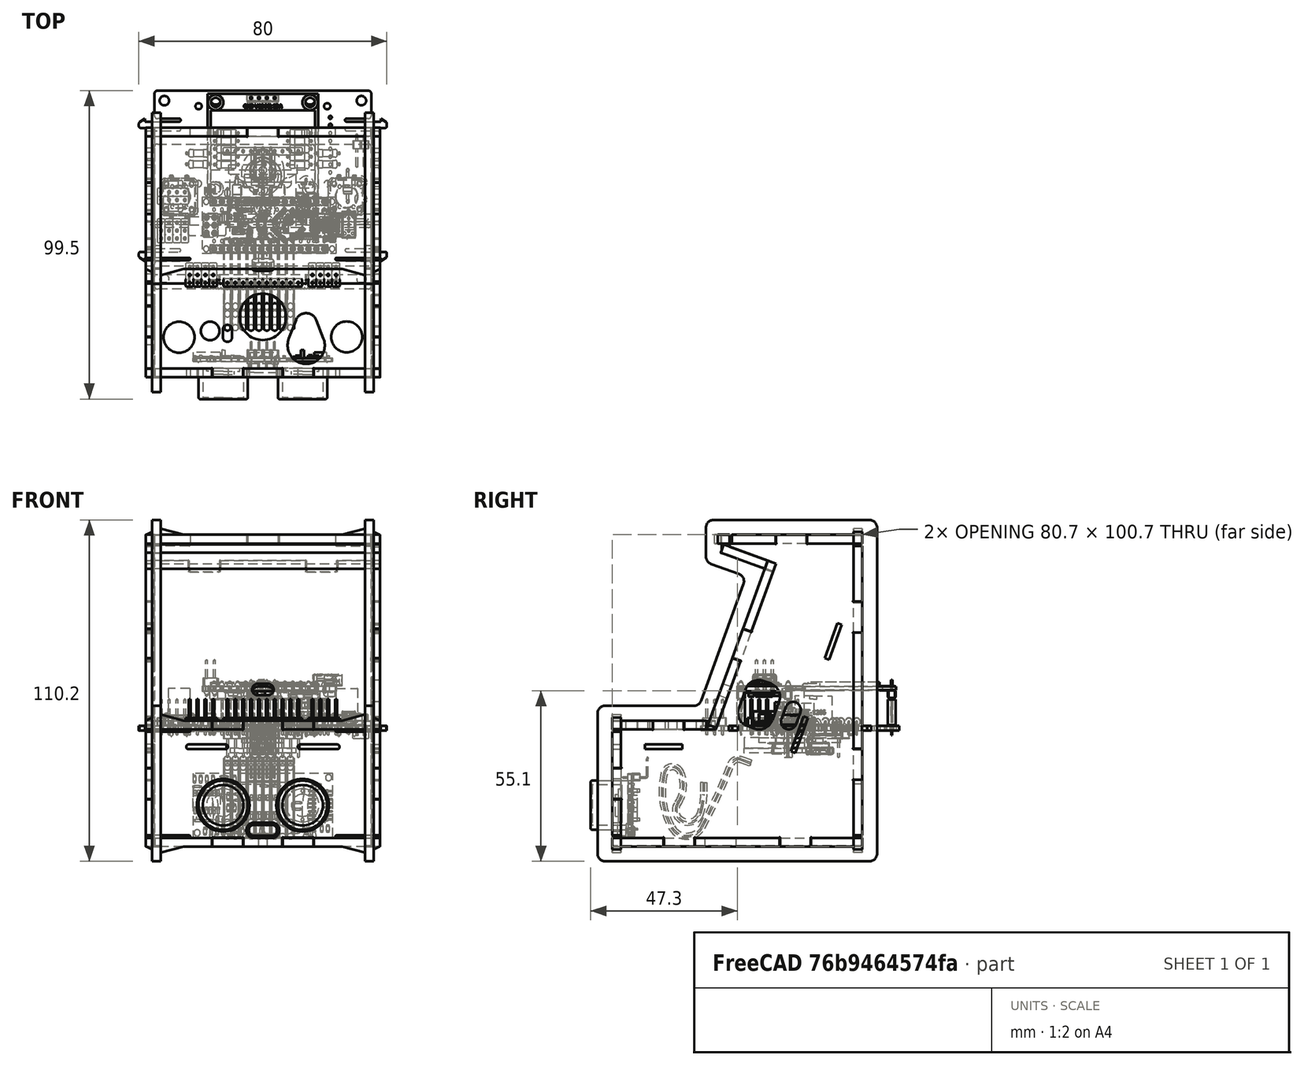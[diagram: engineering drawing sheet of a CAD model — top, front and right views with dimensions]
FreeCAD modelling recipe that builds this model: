
FCSTD DOCUMENT  (FreeCAD 1.0R39319 (Git))
Label: TheThing_v81_multiJoin_parts_assy_LS2
License: CERN Open Hardware Licence permissive
LicenseURL: https://cern-ohl.web.cern.ch/
objects: Part::Feature×104, Sketcher::SketchObject×25, Part::Part2DObjectPython×14, PartDesign::Body×13, App::Part×12, PartDesign::Plane×11, PartDesign::AdditivePipe×9, PartDesign::FeatureBase×9, PartDesign::SubShapeBinder×8, App::DocumentObjectGroup×5, PartDesign::Pad×5, App::VRMLObject×2, TechDraw::DrawSVGTemplate×1, PartDesign::Line×1, PartDesign::PolarPattern×1, PartDesign::Groove×1, PartDesign::Chamfer×1, PartDesign::SubtractivePipe×1, TechDraw::DrawViewImage×1, TechDraw::DrawPage×1
note: 272 computed .brp shape members not serialized (recipe doc carries the construction recipe); baked Part::Feature solids carry a one-line shape summary decoded from their .brp

FEATURE [Part::Feature] Pad001_tab
  shape: bbox 2.8 x 80.6 x 100.6 mm, 98 faces (baked)
FEATURE [Part::Feature] Pad002_tab
  shape: bbox 2.8 x 80.6 x 100.6 mm, 86 faces (baked)
FEATURE [Part::Feature] Pocket_tab
  shape: bbox 75.6 x 2.8 x 104.6 mm, 110 faces (baked)
FEATURE [Part::Feature] Pocket016_tab
  shape: bbox 75.6 x 22.4 x 55.27 mm, 82 faces (baked)
FEATURE [Part::Feature] Pad018_tab
  shape: bbox 75.6 x 33.14 x 2.8 mm, 64 faces (baked)
FEATURE [Part::Feature] Pocket017_tab
  shape: bbox 75.6 x 2.8 x 44.6 mm, 118 faces (baked)
FEATURE [Part::Feature] Pocket021_tab
  shape: bbox 75.6 x 77.8 x 2.8 mm, 54 faces (baked)
FEATURE [Part::Feature] Fillet_tab
  shape: bbox 75.6 x 47.6 x 2.8 mm, 54 faces (baked)
FEATURE [Part::Feature] Pad016_tab
  shape: bbox 75.6 x 17.8 x 8.761 mm, 22 faces (baked)
FEATURE [Part::Feature] Body_right_clip_tab
  shape: bbox 2.8 x 90.2 x 110.2 mm, 46 faces (baked)
FEATURE [Part::Feature] Body_left_clip_tab
  Placement = pos=(-68.8,0,0) rot=(0,0,1;0rad)
  shape: bbox 2.8 x 90.2 x 110.2 mm, 46 faces (baked)
FEATURE [Part::Feature] Part__Feature001  label="switch_slide"
  shape: bbox 10.8 x 10.21 x 13.32 mm, 46 faces (baked)
FEATURE [Part::Feature] Part__Feature002  label="Stopper_bat"
  shape: bbox 2.8 x 15.6 x 14 mm, 30 faces (baked)
FEATURE [App::VRMLObject] TheThing_v8_main
  Placement = pos=(0,5.3,13.8) rot=(1,0,0;1.22173rad)
FEATURE [App::VRMLObject] TheThing_v8_addon
  Placement = pos=(0,-45.3,-5.2) rot=(0,0,1;0rad)
FEATURE [Part::Feature] Part__Feature004  label="User Library-9V Duracell Battery"
  shape: bbox 25.33 x 0.8457 x 15.74 mm, 1 faces, 0 solids (baked)
FEATURE [Part::Feature] Part__Feature005  label="User Library-9V Duracell Battery001"
  shape: bbox 24.78 x 2e-07 x 15.38 mm, 1 faces, 0 solids (baked)
FEATURE [Part::Feature] Part__Feature006  label="User Library-9V Duracell Battery002"
  shape: bbox 26 x 42.82 x 16.6 mm, 188 faces, 0 solids (baked)
FEATURE [Part::Feature] Part__Feature007  label="User Library-9V Duracell Battery003"
  shape: bbox 8.776 x 3 x 7.6 mm, 28 faces, 0 solids (baked)
FEATURE [Part::Feature] Part__Feature008  label="User Library-9V Duracell Battery004"
  shape: bbox 6.35 x 1.5 x 6.35 mm, 2 faces, 0 solids (baked)
FEATURE [Part::Feature] Part__Feature009  label="User Library-9V Duracell Battery005"
  shape: bbox 8 x 3.2 x 8 mm, 10 faces, 0 solids (baked)
FEATURE [App::Part] User_Library_9V_Duracell_Battery  label="9V Duracell Battery006"
  Group = -> [Part__Feature004,Part__Feature005,Part__Feature006,Part__Feature007,Part__Feature008,Part__Feature009]
  Origin = -> Origin
  Placement = pos=(0,0.6,-26) rot=(0,0,1;0rad)
FEATURE [Part::Feature] Part__Feature951  label="_68005_cp005_cp"
  shape: bbox 13.59 x 26.29 x 1.575 mm, 25 faces (baked)
FEATURE [Part::Feature] Part__Feature954  label="_68005_cp005_cp003"
  shape: bbox 7.925 x 7.925 x 3.557 mm, 30 faces (baked)
FEATURE [Part::Feature] Part__Feature955  label="_68005_cp005_cp004"
  shape: bbox 9.35 x 9.35 x 4.186 mm, 132 faces (baked)
FEATURE [App::Part] _68005_cp005_cp  label="9V_conn"
  Group = -> [Part__Feature951,Part__Feature954,Part__Feature955]
  Origin = -> Origin041
  Placement = pos=(-2.41e-14,30,-26) rot=(0.57735,-0.57735,-0.57735;4.18879rad)
FEATURE [App::DocumentObjectGroup] Group  label="Acrylic_Parts"
  Group = -> [Pad001_tab,Pad002_tab,Pocket_tab,Pocket016_tab,Pad018_tab,Pocket017_tab,Pocket021_tab,Fillet_tab,Pad016_tab,Body_right_clip_tab,Body_left_clip_tab]
FEATURE [Part::Feature] Part__Feature956  label="PinSocket_1x10_P2.54mm_Vertical"
  Placement = pos=(-11.4,-16.0152,-10.4002) rot=(-0.633687,0.633687,0.443713;2.30637rad)
  shape: bbox 25.4 x 11.37 x 5.294 mm, 270 faces (baked)
FEATURE [Part::Feature] Part__Feature957  label="PinSocket_1x10_P2.54mm_Vertical001"
  Placement = pos=(-11.4,-31.1152,-17.0002) rot=(0,0,-1;4.71239rad)
  shape: bbox 25.4 x 2.54 x 11.6 mm, 270 faces (baked)
FEATURE [PartDesign::Plane] DatumPlane
  AttachmentOffset = pos=(0,-16.7,0) rot=(1,0,0;1.5708rad)
  Length = 82.3105
  MapMode = 2
  Placement = pos=(11.43,0,-16.7) rot=(0.707107,0.707107,0;3.14159rad)
  ResizeMode = 0
  Width = 61.8694
FEATURE [Sketcher::SketchObject] Sketch001
  ArcFitTolerance = 1e-06
  FullyConstrained = true
  MakeInternals = false
  MapMode = 5
  Placement = pos=(11.43,0,-16.7) rot=(0.707107,0.707107,0;3.14159rad)
  sketch-geometry (9):
    g0: ArcOfCircle CenterX=-31.1 CenterY=0 CenterZ=0 NormalX=0 NormalY=0 NormalZ=1 AngleXU=0 Radius=1 StartAngle=1.82348 EndAngle=4.45971
    g1: LineSegment StartX=-30.85 StartY=-1.23825 StartZ=0 EndX=-30.85 EndY=-0.968246 EndZ=0
    g2: LineSegment StartX=-30.85 StartY=1.23825 StartZ=0 EndX=-31.35 EndY=1.23825 EndZ=0
    g3: LineSegment StartX=-31.35 StartY=1.23825 StartZ=0 EndX=-31.35 EndY=0.968246 EndZ=0
    g4: LineSegment StartX=-31.35 StartY=-1.23825 StartZ=0 EndX=-30.85 EndY=-1.23825 EndZ=0
    g5: GeomPoint [constr] X=-31.1 Y=0 Z=0
    g6: ArcOfCircle CenterX=-31.1 CenterY=0 CenterZ=0 NormalX=0 NormalY=0 NormalZ=1 AngleXU=0 Radius=1 StartAngle=4.96507 EndAngle=7.6013
    g7: LineSegment StartX=-31.35 StartY=-0.968246 StartZ=0 EndX=-31.35 EndY=-1.23825 EndZ=0
    g8: LineSegment StartX=-30.85 StartY=0.968246 StartZ=0 EndX=-30.85 EndY=1.23825 EndZ=0
  constraints (27):
    c: Diameter(g0) = 2
    c: Distance(g0,g-2) = 31.1
    c: PointOnObject(g0,g-1)
    c: Coincident(g8,g2)
    c: Coincident(g2,g3)
    c: Coincident(g7,g4)
    c: Coincident(g4,g1)
    c: Vertical(g1)
    c: Vertical(g3)
    c: Horizontal(g2)
    c: Horizontal(g4)
    c: Symmetric(g3,g1,g5)
    c: Coincident(g5,g0)
    c: Distance(g2,g2) = 0.5
    c: PointOnObject(g6,g8)
    c: Equal(g0,g6)
    c: PointOnObject(g0,g7)
    c: Coincident(g0,g6)
    c: Coincident(g3,g0)
    c: PointOnObject(g7,g0)
    c: Coincident(g1,g6)
    c: PointOnObject(g8,g6)
    c: Equal(g7,g3)
    c: DistanceY(g3,g3) = 0.27
    c: Vertical(g8)
    c: Vertical(g7)
    c: Equal(g4,g2)
FEATURE [Sketcher::SketchObject] Sketch002
  ArcFitTolerance = 1e-06
  ExternalGeometry = -> [Sketch001]
  FullyConstrained = false
  MakeInternals = false
  MapMode = 5
  Placement = pos=(0,0,0) rot=(0.57735,0.57735,0.57735;2.0944rad)
  sketch-geometry (11):
    g0: LineSegment StartX=-31.1 StartY=-16.7 StartZ=0 EndX=-31.1 EndY=-20.5857 EndZ=0
    g1: ArcOfCircle CenterX=-48.3989 CenterY=-20.5857 CenterZ=0 NormalX=0 NormalY=0 NormalZ=1 AngleXU=0 Radius=17.2989 StartAngle=5.99931 EndAngle=6.28319
    g2: LineSegment StartX=-31.7924 StartY=-25.4308 StartZ=0 EndX=-32.1908 EndY=-26.7964 EndZ=0
    g3: ArcOfCircle CenterX=-36.0202 CenterY=-25.6792 CenterZ=0 NormalX=0 NormalY=0 NormalZ=1 AngleXU=0 Radius=3.98901 StartAngle=2.55428 EndAngle=5.99931
    g4: ArcOfCircle CenterX=-48.0615 CenterY=-17.6636 CenterZ=0 NormalX=0 NormalY=0 NormalZ=1 AngleXU=0 Radius=10.4762 StartAngle=5.69587 EndAngle=6.70733
    g5: ArcOfCircle CenterX=-41.0617 CenterY=-14.5029 CenterZ=0 NormalX=0 NormalY=0 NormalZ=1 AngleXU=0 Radius=2.79585 StartAngle=0.424141 EndAngle=2.90432
    g6: ArcOfCircle CenterX=-20.5527 CenterY=-19.4626 CenterZ=0 NormalX=0 NormalY=0 NormalZ=1 AngleXU=0 Radius=23.896 StartAngle=2.90432 EndAngle=3.65756
    g7: ArcOfCircle CenterX=-36.4895 CenterY=-28.5021 CenterZ=0 NormalX=0 NormalY=0 NormalZ=1 AngleXU=0 Radius=5.57402 StartAngle=3.65756 EndAngle=5.79202
    g8: ArcOfCircle CenterX=-198.048 CenterY=57.9126 CenterZ=0 NormalX=0 NormalY=0 NormalZ=1 AngleXU=0 Radius=188.791 StartAngle=5.79202 EndAngle=5.91067
    g9: ArcOfCircle CenterX=-19.8146 CenterY=-11.7327 CenterZ=0 NormalX=0 NormalY=0 NormalZ=1 AngleXU=0 Radius=2.56576 StartAngle=1.21797 EndAngle=2.76908
    g10: LineSegment StartX=-18.928 StartY=-9.32503 StartZ=0 EndX=-15.8303 EndY=-10.4657 EndZ=0
  constraints (12):
    c: Vertical(g0)
    c: Tangent(g0,g1) = 1.5708
    c: Tangent(g2,g3) = 1.5708
    c: Tangent(g3,g4) = 1.5708
    c: Tangent(g4,g5) = -1.5708
    c: Tangent(g5,g6) = -1.5708
    c: Tangent(g6,g7) = -1.5708
    c: Tangent(g7,g8) = -1.5708
    c: Tangent(g8,g9) = 1.5708
    c: Tangent(g1,g2) = 1.5708
    c: Symmetric(g-3,g-3,g0)
    c: Tangent(g9,g10) = 1.5708
FEATURE [PartDesign::AdditivePipe] AdditivePipe
  AuxilleryCurvelinear = true
  AuxillerySpineTangent = false
  Binormal = (0,0,0)
  Mode = 0
  Placement = pos=(11.43,0,-16.7) rot=(0.707107,0.707107,0;3.14159rad)
  Profile = -> Sketch001
  Refine = true
  Spine = -> Sketch002
  SpineTangent = false
  Suppressed = false
  Transformation = 0
  Transition = 0
FEATURE [PartDesign::Body] Body  label="Cable_flat_10x"
  AllowCompound = false
  Group = -> [DatumPlane,Sketch001,Sketch002,AdditivePipe]
  Origin = -> Origin042
  Tip = -> AdditivePipe
FEATURE [PartDesign::FeatureBase] Clone
  BaseFeature = -> Body
  Suppressed = false
FEATURE [PartDesign::Body] Body001
  AllowCompound = false
  BaseFeature = -> Body
  Group = -> [Clone]
  Origin = -> Origin043
  Placement = pos=(-2.54,0,0) rot=(0,0,1;0rad)
  Tip = -> Clone
FEATURE [PartDesign::FeatureBase] Clone001
  BaseFeature = -> Body
  Suppressed = false
FEATURE [PartDesign::Body] Body002
  AllowCompound = false
  BaseFeature = -> Body
  Group = -> [Clone001]
  Origin = -> Origin044
  Placement = pos=(-5.08,0,0) rot=(0,0,1;0rad)
  Tip = -> Clone001
FEATURE [PartDesign::FeatureBase] Clone002
  BaseFeature = -> Body
  Suppressed = false
FEATURE [PartDesign::Body] Body003
  AllowCompound = false
  BaseFeature = -> Body
  Group = -> [Clone002]
  Origin = -> Origin045
  Placement = pos=(-7.62,0,0) rot=(0,0,1;0rad)
  Tip = -> Clone002
FEATURE [PartDesign::FeatureBase] Clone003
  BaseFeature = -> Body
  Suppressed = false
FEATURE [PartDesign::Body] Body004
  AllowCompound = false
  BaseFeature = -> Body
  Group = -> [Clone003]
  Origin = -> Origin046
  Placement = pos=(-10.16,0,0) rot=(0,0,1;0rad)
  Tip = -> Clone003
FEATURE [PartDesign::FeatureBase] Clone004
  BaseFeature = -> Body
  Suppressed = false
FEATURE [PartDesign::Body] Body005
  AllowCompound = false
  BaseFeature = -> Body
  Group = -> [Clone004]
  Origin = -> Origin047
  Placement = pos=(-12.7,0,0) rot=(0,0,1;0rad)
  Tip = -> Clone004
FEATURE [PartDesign::FeatureBase] Clone005
  BaseFeature = -> Body
  Suppressed = false
FEATURE [PartDesign::Body] Body006
  AllowCompound = false
  BaseFeature = -> Body
  Group = -> [Clone005]
  Origin = -> Origin048
  Placement = pos=(-15.24,0,0) rot=(0,0,1;0rad)
  Tip = -> Clone005
FEATURE [PartDesign::FeatureBase] Clone006
  BaseFeature = -> Body
  Suppressed = false
FEATURE [PartDesign::Body] Body007
  AllowCompound = false
  BaseFeature = -> Body
  Group = -> [Clone006]
  Origin = -> Origin049
  Placement = pos=(-17.78,0,0) rot=(0,0,1;0rad)
  Tip = -> Clone006
FEATURE [PartDesign::FeatureBase] Clone007
  BaseFeature = -> Body
  Suppressed = false
FEATURE [PartDesign::Body] Body008
  AllowCompound = false
  BaseFeature = -> Body
  Group = -> [Clone007]
  Origin = -> Origin050
  Placement = pos=(-20.32,0,0) rot=(0,0,1;0rad)
  Tip = -> Clone007
FEATURE [PartDesign::FeatureBase] Clone008
  BaseFeature = -> Body
  Suppressed = false
FEATURE [PartDesign::Body] Body009
  AllowCompound = false
  BaseFeature = -> Body
  Group = -> [Clone008]
  Origin = -> Origin051
  Placement = pos=(-22.86,0,0) rot=(0,0,1;0rad)
  Tip = -> Clone008
FEATURE [App::DocumentObjectGroup] Group003  label="Flat_Cable_10x"
  Group = -> [Body,Body001,Body002,Body003,Body004,Body005,Body006,Body007,Body008,Body009]
FEATURE [Part::Feature] Solid  label="PinSocket_1x02_P2.54mm_Vertical"
  Placement = pos=(30.3,8.89176,17.5439) rot=(-0.171088,0.171088,0.970288;1.60095rad)
  shape: bbox 5.08 x 5.294 x 11.37 mm, 62 faces (baked)
FEATURE [PartDesign::SubShapeBinder] Binder  label="Binder(PinSocket_1x02_P2.54mm_Vertical)"
  BindCopyOnChange = 0
  BindMode = 0
  ClaimChildren = false
  Context = -> Group004 [Body010.Binder.]
  Fuse = false
  MakeFace = true
  OffsetFill = false
  OffsetIntersection = false
  OffsetJoinType = 0
  OffsetOpenResult = false
  PartialLoad = false
  Relative = true
  Support = -> [Solid]
  _Version = 8
FEATURE [PartDesign::SubShapeBinder] Binder001  label="Binder001(9V_conn)"
  BindCopyOnChange = 0
  BindMode = 0
  ClaimChildren = false
  Context = -> Group004 [Body010.Binder001.]
  Fuse = false
  MakeFace = true
  OffsetFill = false
  OffsetIntersection = false
  OffsetJoinType = 0
  OffsetOpenResult = false
  PartialLoad = false
  Relative = true
  Support = -> [_68005_cp005_cp]
  _Version = 8
FEATURE [PartDesign::SubShapeBinder] Binder002  label="Binder002(Pocket_tab)"
  BindCopyOnChange = 0
  BindMode = 0
  ClaimChildren = false
  Context = -> Group004 [Body010.Binder002.]
  Fuse = false
  MakeFace = true
  OffsetFill = false
  OffsetIntersection = false
  OffsetJoinType = 0
  OffsetOpenResult = false
  PartialLoad = false
  Relative = true
  Support = -> [Pocket_tab]
  _Version = 8
FEATURE [Sketcher::SketchObject] Sketch
  ArcFitTolerance = 1e-06
  ExternalGeometry = -> [Binder001]
  FullyConstrained = true
  MakeInternals = false
  MapMode = 5
  Placement = pos=(0,2.34e-14,-19.2055) rot=(0,0,1;0rad)
  sketch-geometry (19):
    g0: ArcOfCircle CenterX=1.23825 CenterY=26.8446 CenterZ=0 NormalX=0 NormalY=0 NormalZ=1 AngleXU=0 Radius=1 StartAngle=3.39427 EndAngle=6.03051
    g1: LineSegment StartX=2.47649 StartY=26.5946 StartZ=0 EndX=2.47649 EndY=27.0946 EndZ=0
    g2: LineSegment StartX=2.47649 StartY=27.0946 StartZ=0 EndX=2.20649 EndY=27.0946 EndZ=0
    g3: LineSegment StartX=0 StartY=27.0946 StartZ=0 EndX=0 EndY=26.5946 EndZ=0
    g4: LineSegment StartX=0 StartY=26.5946 StartZ=0 EndX=0.27 EndY=26.5946 EndZ=0
    g5: GeomPoint [constr] X=1.23825 Y=26.8446 Z=0
    g6: ArcOfCircle CenterX=1.23825 CenterY=26.8446 CenterZ=0 NormalX=0 NormalY=0 NormalZ=1 AngleXU=0 Radius=1 StartAngle=0.25268 EndAngle=2.88891
    g7: LineSegment StartX=0.27 StartY=27.0946 StartZ=0 EndX=0 EndY=27.0946 EndZ=0
    g8: LineSegment StartX=2.20649 StartY=26.5946 StartZ=0 EndX=2.47649 EndY=26.5946 EndZ=0
    g9: LineSegment [constr] StartX=2.47649 StartY=26.8446 StartZ=0 EndX=6.34996 EndY=26.8446 EndZ=0
    g10: ArcOfCircle [constr] CenterX=-1.23825 CenterY=26.8446 CenterZ=0 NormalX=0 NormalY=0 NormalZ=1 AngleXU=0 Radius=1 StartAngle=3.39427 EndAngle=6.03051
    g11: LineSegment [constr] StartX=0 StartY=26.5946 StartZ=0 EndX=0 EndY=27.0946 EndZ=0
    g12: LineSegment [constr] StartX=0 StartY=27.0946 StartZ=0 EndX=-0.27 EndY=27.0946 EndZ=0
    g13: LineSegment [constr] StartX=-2.47649 StartY=27.0946 StartZ=0 EndX=-2.47649 EndY=26.5946 EndZ=0
    g14: LineSegment [constr] StartX=-2.47649 StartY=26.5946 StartZ=0 EndX=-2.20649 EndY=26.5946 EndZ=0
    g15: GeomPoint [constr] X=-1.23825 Y=26.8446 Z=0
    g16: LineSegment [constr] StartX=-2.20649 StartY=27.0946 StartZ=0 EndX=-2.47649 EndY=27.0946 EndZ=0
    g17: ArcOfCircle [constr] CenterX=-1.23825 CenterY=26.8446 CenterZ=0 NormalX=0 NormalY=0 NormalZ=1 AngleXU=0 Radius=1 StartAngle=0.25268 EndAngle=2.88891
    g18: LineSegment [constr] StartX=-0.27 StartY=26.5946 StartZ=0 EndX=0 EndY=26.5946 EndZ=0
  constraints (51):
    c: Coincident(g1,g2)
    c: Coincident(g7,g3)
    c: Coincident(g3,g4)
    c: Coincident(g8,g1)
    c: Horizontal(g2)
    c: Horizontal(g4)
    c: Vertical(g1)
    c: Vertical(g3)
    c: Symmetric(g7,g1,g5)
    c: Coincident(g5,g0)
    c: Diameter(g0) = 2
    c: DistanceY(g3,g3) = 0.5
    c: Equal(g0,g6)
    c: Coincident(g0,g6)
    c: Coincident(g2,g6)
    c: Coincident(g7,g6)
    c: Coincident(g4,g0)
    c: Coincident(g8,g0)
    c: Horizontal(g7)
    c: Horizontal(g8)
    c: Equal(g7,g2)
    c: DistanceX(g7,g7) = 0.27
    c: Horizontal(g9)
    c: Equal(g3,g1)
    c: Symmetric(g1,g1,g9)
    c: Symmetric(g-4,g-4,g9)
    c: Coincident(g11,g12)
    c: Coincident(g16,g13)
    c: Coincident(g13,g14)
    c: Coincident(g18,g11)
    c: Horizontal(g12)
    c: Horizontal(g14)
    c: Vertical(g11)
    c: Vertical(g13)
    c: Symmetric(g16,g11,g15)
    c: Coincident(g15,g10)
    c: Coincident(g16,g17)
    c: Equal(g10,g17)
    c: Coincident(g17,g12)
    c: Coincident(g10,g17)
    c: Coincident(g14,g10)
    c: Coincident(g18,g10)
    c: Horizontal(g16)
    c: Horizontal(g18)
    c: Equal(g12,g16)
    c: Equal(g13,g11)
    c: Equal(g17,g6)
    c: Equal(g12,g7)
    c: Equal(g11,g3)
    c: PointOnObject(g7,g-2)
    c: Coincident(g12,g7)
FEATURE [PartDesign::Plane] DatumPlane001
  AttachmentOffset = pos=(0,0,-0.8) rot=(0,0,1;0rad)
  Length = 67.3011
  MapMode = 5
  Placement = pos=(6.1e-15,26.832,3.28e-14) rot=(0,0.707107,0.707107;3.14159rad)
  ResizeMode = 0
  Width = 60.6448
FEATURE [Sketcher::SketchObject] Sketch003
  ArcFitTolerance = 1e-06
  ExternalGeometry = -> [Sketch]
  FullyConstrained = true
  MakeInternals = false
  MapMode = 5
  Placement = pos=(6.1e-15,26.832,3.28e-14) rot=(0,0.707107,0.707107;3.14159rad)
  sketch-geometry (3):
    g0: LineSegment StartX=-3.73e-14 StartY=-19.2055 StartZ=0 EndX=-3.73e-14 EndY=-13.2055 EndZ=0
    g1: ArcOfCircle CenterX=-5.5 CenterY=-13.2055 CenterZ=0 NormalX=0 NormalY=0 NormalZ=1 AngleXU=0 Radius=5.5 StartAngle=1.88e-14 EndAngle=3.14159
    g2: LineSegment StartX=-11 StartY=-13.2055 StartZ=0 EndX=-11 EndY=-14.0055 EndZ=0
  constraints (8):
    c: Vertical(g0)
    c: Tangent(g0,g1) = -1.5708
    c: Angle(g1) = 3.14159
    c: Tangent(g1,g2) = -1.5708
    c: DistanceY(g0,g0) = 6
    c: Radius(g1) = 5.5
    c: DistanceY(g2,g2) = 0.8
    c: Coincident(g0,g-3)
FEATURE [PartDesign::Plane] DatumPlane002
  AttachmentOffset = pos=(0,0,0) rot=(0.57735,0.57735,0.57735;2.0944rad)
  Length = 63.1173
  MapMode = 7
  Placement = pos=(11,26.832,-13.2055) rot=(0.57735,0.57735,0.57735;2.0944rad)
  ResizeMode = 0
  Width = 60.2798
FEATURE [Sketcher::SketchObject] Sketch004
  ArcFitTolerance = 1e-06
  ExternalGeometry = -> [Sketch003]
  FullyConstrained = true
  MakeInternals = false
  MapMode = 5
  Placement = pos=(11,26.832,-13.2055) rot=(0.57735,0.57735,0.57735;2.0944rad)
  sketch-geometry (3):
    g0: LineSegment StartX=0 StartY=-0.8 StartZ=0 EndX=0 EndY=-2 EndZ=0
    g1: ArcOfCircle CenterX=-2.3 CenterY=-2 CenterZ=0 NormalX=0 NormalY=0 NormalZ=1 AngleXU=0 Radius=2.3 StartAngle=4.71239 EndAngle=6.28319
    g2: LineSegment StartX=-2.3 StartY=-4.3 StartZ=0 EndX=-18.3 EndY=-4.3 EndZ=0
  constraints (8):
    c: Coincident(g-3,g0)
    c: PointOnObject(g0,g-2)
    c: Tangent(g0,g1) = 1.5708
    c: Angle(g1) = 1.5708
    c: Tangent(g1,g2) = 1.5708
    c: DistanceY(g0,g0) = 1.2
    c: Radius(g1) = 2.3
    c: DistanceX(g2,g2) = 16
FEATURE [PartDesign::Plane] DatumPlane003
  AttachmentOffset = pos=(0,0,0) rot=(-0.57735,0.57735,0.57735;2.0944rad)
  Length = 63.7802
  MapMode = 45
  Placement = pos=(11,16.532,-17.5055) rot=(0,0,1;4.71239rad)
  ResizeMode = 0
  Width = 67.599
FEATURE [Sketcher::SketchObject] Sketch005
  ArcFitTolerance = 1e-06
  ExternalGeometry = -> [Sketch004,Binder]
  FullyConstrained = false
  MakeInternals = false
  MapMode = 5
  Placement = pos=(11,16.532,-17.5055) rot=(0,0,-1;1.5708rad)
  sketch-geometry (3):
    g0: ArcOfCircle CenterX=8 CenterY=4.21059 CenterZ=0 NormalX=0 NormalY=0 NormalZ=1 AngleXU=0 Radius=4.21059 StartAngle=4.71239 EndAngle=7.61609
    g1: ArcOfCircle CenterX=12.2495 CenterY=21.7356 CenterZ=0 NormalX=0 NormalY=0 NormalZ=1 AngleXU=0 Radius=13.8222 StartAngle=3.8393 EndAngle=4.4745
    g2: ArcOfCircle CenterX=5.29691 CenterY=15.9067 CenterZ=0 NormalX=0 NormalY=0 NormalZ=1 AngleXU=0 Radius=4.74953 StartAngle=1.5708 EndAngle=3.8393
  constraints (5):
    c: Tangent(g0,g1) = 1.5708
    c: Tangent(g1,g2) = -1.5708
    c: PointOnObject(g2,g-5)
    c: Perpendicular(g2,g-5)
    c: Tangent(g0,g-3) = -1.5708
FEATURE [PartDesign::Plane] DatumPlane004
  AttachmentOffset = pos=(0,0,-2.5) rot=(0,0,1;0rad)
  Length = 63.1173
  MapMode = 5
  Placement = pos=(31.61,3.25e-14,6e-16) rot=(0.57735,0.57735,0.57735;2.0944rad)
  ResizeMode = 0
  Width = 60.2798
FEATURE [Sketcher::SketchObject] Sketch006
  ArcFitTolerance = 1e-06
  ExternalGeometry = -> [Sketch005,Binder]
  FullyConstrained = true
  MakeInternals = false
  MapMode = 5
  Placement = pos=(31.61,3.25e-14,6e-16) rot=(0.57735,0.57735,0.57735;2.0944rad)
  sketch-geometry (3):
    g0: LineSegment StartX=11.2351 StartY=-17.5055 StartZ=0 EndX=7.55999 EndY=-17.5055 EndZ=0
    g1: ArcOfCircle CenterX=7.55999 CenterY=-9.50551 CenterZ=0 NormalX=0 NormalY=0 NormalZ=1 AngleXU=0 Radius=8 StartAngle=2.79253 EndAngle=4.71239
    g2: LineSegment StartX=0.0424531 StartY=-6.76935 StartZ=0 EndX=8.96016 EndY=17.7319 EndZ=0
  constraints (7):
    c: Coincident(g0,g-3)
    c: Horizontal(g0)
    c: Tangent(g0,g1) = 1.5708
    c: Perpendicular(g2,g-4)
    c: Symmetric(g-4,g-4,g2)
    c: Tangent(g1,g2) = 1.5708
    c: Radius(g1) = 8
FEATURE [TechDraw::DrawSVGTemplate] Template
  Height = 210
  Orientation = 1
  Template = <userpath>/Documents/FreeCAD/Templates/A4_Landscape_blank.svg
  Width = 297
FEATURE [Sketcher::SketchObject] Sketch007
  ArcFitTolerance = 1e-06
  AttachmentSupport = -> [Binder001]
  ExternalGeometry = -> [Binder001]
  FullyConstrained = true
  MakeInternals = false
  MapMode = 5
  Placement = pos=(4.3e-15,2.23e-14,-19.2055) rot=(0,0,1;0rad)
  sketch-geometry (19):
    g0: ArcOfCircle [constr] CenterX=1.23825 CenterY=26.8446 CenterZ=0 NormalX=0 NormalY=0 NormalZ=1 AngleXU=0 Radius=1 StartAngle=3.39427 EndAngle=6.03051
    g1: LineSegment [constr] StartX=2.47649 StartY=26.5946 StartZ=0 EndX=2.47649 EndY=27.0946 EndZ=0
    g2: LineSegment [constr] StartX=2.47649 StartY=27.0946 StartZ=0 EndX=2.20649 EndY=27.0946 EndZ=0
    g3: LineSegment StartX=0 StartY=27.0946 StartZ=0 EndX=0 EndY=26.5946 EndZ=0
    g4: LineSegment [constr] StartX=0 StartY=26.5946 StartZ=0 EndX=0.27 EndY=26.5946 EndZ=0
    g5: GeomPoint [constr] X=1.23825 Y=26.8446 Z=0
    g6: ArcOfCircle [constr] CenterX=1.23825 CenterY=26.8446 CenterZ=0 NormalX=0 NormalY=0 NormalZ=1 AngleXU=0 Radius=1 StartAngle=0.25268 EndAngle=2.88891
    g7: LineSegment [constr] StartX=0.27 StartY=27.0946 StartZ=0 EndX=0 EndY=27.0946 EndZ=0
    g8: LineSegment [constr] StartX=2.20649 StartY=26.5946 StartZ=0 EndX=2.47649 EndY=26.5946 EndZ=0
    g9: LineSegment [constr] StartX=2.47649 StartY=26.8446 StartZ=0 EndX=-2.47649 EndY=26.8446 EndZ=0
    g10: ArcOfCircle CenterX=-1.23825 CenterY=26.8446 CenterZ=0 NormalX=0 NormalY=0 NormalZ=1 AngleXU=0 Radius=1 StartAngle=3.39427 EndAngle=6.03051
    g11: LineSegment [constr] StartX=0 StartY=26.5946 StartZ=0 EndX=0 EndY=27.0946 EndZ=0
    g12: LineSegment StartX=0 StartY=27.0946 StartZ=0 EndX=-0.27 EndY=27.0946 EndZ=0
    g13: LineSegment StartX=-2.47649 StartY=27.0946 StartZ=0 EndX=-2.47649 EndY=26.5946 EndZ=0
    g14: LineSegment StartX=-2.47649 StartY=26.5946 StartZ=0 EndX=-2.20649 EndY=26.5946 EndZ=0
    g15: GeomPoint [constr] X=-1.23825 Y=26.8446 Z=0
    g16: LineSegment StartX=-2.20649 StartY=27.0946 StartZ=0 EndX=-2.47649 EndY=27.0946 EndZ=0
    g17: ArcOfCircle CenterX=-1.23825 CenterY=26.8446 CenterZ=0 NormalX=0 NormalY=0 NormalZ=1 AngleXU=0 Radius=1 StartAngle=0.25268 EndAngle=2.88891
    g18: LineSegment StartX=-0.27 StartY=26.5946 StartZ=0 EndX=0 EndY=26.5946 EndZ=0
  constraints (51):
    c: Coincident(g1,g2)
    c: Coincident(g7,g3)
    c: Coincident(g3,g4)
    c: Coincident(g8,g1)
    c: Horizontal(g2)
    c: Horizontal(g4)
    c: Vertical(g1)
    c: Vertical(g3)
    c: Symmetric(g7,g1,g5)
    c: Coincident(g5,g0)
    c: Diameter(g0) = 2
    c: DistanceY(g3,g3) = 0.5
    c: Equal(g0,g6)
    c: Coincident(g0,g6)
    c: Coincident(g2,g6)
    c: Coincident(g7,g6)
    c: Coincident(g4,g0)
    c: Coincident(g8,g0)
    c: Horizontal(g7)
    c: Horizontal(g8)
    c: Equal(g7,g2)
    c: DistanceX(g7,g7) = 0.27
    c: Equal(g3,g1)
    c: Symmetric(g1,g1,g9)
    c: Coincident(g11,g12)
    c: Coincident(g16,g13)
    c: Coincident(g13,g14)
    c: Coincident(g18,g11)
    c: Horizontal(g12)
    c: Horizontal(g14)
    c: Vertical(g11)
    c: Vertical(g13)
    c: Symmetric(g16,g11,g15)
    c: Coincident(g15,g10)
    c: Coincident(g16,g17)
    c: Equal(g10,g17)
    c: Coincident(g17,g12)
    c: Coincident(g10,g17)
    c: Coincident(g14,g10)
    c: Coincident(g18,g10)
    c: Horizontal(g16)
    c: Horizontal(g18)
    c: Equal(g12,g16)
    c: Equal(g13,g11)
    c: Equal(g17,g6)
    c: Equal(g12,g7)
    c: Equal(g11,g3)
    c: PointOnObject(g7,g-2)
    c: Coincident(g12,g7)
    c: PointOnObject(g9,g13)
    c: Symmetric(g-3,g-3,g9)
FEATURE [PartDesign::AdditivePipe] AdditivePipe001
  AuxilleryCurvelinear = true
  AuxillerySpineTangent = false
  Binormal = (0,0,0)
  Mode = 0
  Placement = pos=(0,2.34e-14,-19.2055) rot=(0,0,1;0rad)
  Profile = -> Sketch
  Refine = true
  Spine = -> Sketch003
  SpineTangent = false
  Suppressed = false
  Transformation = 0
  Transition = 0
FEATURE [PartDesign::AdditivePipe] AdditivePipe002
  AuxilleryCurvelinear = true
  AuxillerySpineTangent = false
  BaseFeature = -> AdditivePipe001
  Binormal = (0,0,0)
  Mode = 0
  Placement = pos=(0,2.34e-14,-19.2055) rot=(0,0,1;0rad)
  Profile = -> AdditivePipe001 [Face11]
  Refine = true
  Spine = -> Sketch004
  SpineTangent = false
  Suppressed = false
  Transformation = 0
  Transition = 0
FEATURE [PartDesign::AdditivePipe] AdditivePipe003
  AuxilleryCurvelinear = true
  AuxillerySpineTangent = false
  BaseFeature = -> AdditivePipe002
  Binormal = (0,0,0)
  Mode = 0
  Placement = pos=(0,2.34e-14,-19.2055) rot=(0,0,1;0rad)
  Profile = -> AdditivePipe002 [Face27]
  Refine = true
  Spine = -> Sketch005
  SpineTangent = false
  Suppressed = false
  Transformation = 0
  Transition = 0
FEATURE [PartDesign::AdditivePipe] AdditivePipe004
  AuxilleryCurvelinear = true
  AuxillerySpineTangent = false
  BaseFeature = -> AdditivePipe003
  Binormal = (0,0,0)
  Mode = 0
  Placement = pos=(0,2.34e-14,-19.2055) rot=(0,0,1;0rad)
  Profile = -> AdditivePipe003 [Face40]
  Refine = true
  Spine = -> Sketch006
  SpineTangent = false
  Suppressed = false
  Transformation = 0
  Transition = 0
FEATURE [PartDesign::Body] Body010  label="Bat+"
  AllowCompound = false
  Group = -> [Binder,Binder001,Binder002,Sketch,DatumPlane001,Sketch003,DatumPlane002,Sketch004,DatumPlane003,Sketch005,DatumPlane004,Sketch006,Sketch007,AdditivePipe001,AdditivePipe002,AdditivePipe003,AdditivePipe004]
  Origin = -> Origin052
  Tip = -> AdditivePipe004
FEATURE [PartDesign::Plane] DatumPlane005
  AttachmentOffset = pos=(0,0,-0.8) rot=(0,0,1;0rad)
  Length = 69.9136
  MapMode = 5
  Placement = pos=(6.1e-15,26.832,3.28e-14) rot=(0,0.707107,0.707107;3.14159rad)
  ResizeMode = 0
  Width = 60.8671
FEATURE [PartDesign::Plane] DatumPlane006
  AttachmentOffset = pos=(0,0,0) rot=(0.57735,0.57735,0.57735;2.0944rad)
  Length = 63.1252
  MapMode = 7
  Placement = pos=(11,26.832,-13.2055) rot=(0.57735,0.57735,0.57735;2.0944rad)
  ResizeMode = 0
  Width = 60.2805
FEATURE [PartDesign::Plane] DatumPlane007
  AttachmentOffset = pos=(0,0,0) rot=(-0.57735,0.57735,0.57735;2.0944rad)
  Length = 64.0165
  MapMode = 45
  Placement = pos=(11,16.532,-17.5055) rot=(0,0,1;4.71239rad)
  ResizeMode = 0
  Width = 70.2184
FEATURE [PartDesign::Plane] DatumPlane008
  AttachmentOffset = pos=(0,0,-2.5) rot=(0,0,1;0rad)
  Length = 63.1252
  MapMode = 5
  Placement = pos=(31.61,3.25e-14,6e-16) rot=(0.57735,0.57735,0.57735;2.0944rad)
  ResizeMode = 0
  Width = 60.2805
FEATURE [PartDesign::Plane] DatumPlane009
  AttachmentOffset = pos=(0,0,0) rot=(1,0,0;1.5708rad)
  Length = 60
  MapMode = 7
  Placement = pos=(19.78,-50.184,8.345) rot=(0,0.707107,-0.707107;3.14159rad)
  ResizeMode = 0
  Width = 60
FEATURE [PartDesign::Plane] DatumPlane010
  Length = 60
  MapMode = 7
  Placement = pos=(13.98,-50.184,18.345) rot=(1,0,0;1.5708rad)
  ResizeMode = 0
  Width = 60
FEATURE [Sketcher::SketchObject] Sketch061
  ArcFitTolerance = 1e-06
  FullyConstrained = true
  MakeInternals = false
  MapMode = 5
  Placement = pos=(19.78,-50.184,8.345) rot=(0,0.707107,-0.707107;3.14159rad)
  sketch-geometry (3):
    g0: LineSegment StartX=0 StartY=0 StartZ=0 EndX=-4.2 EndY=2.42487 EndZ=0
    g1: LineSegment StartX=-4.2 StartY=2.42487 StartZ=0 EndX=-4.2 EndY=0 EndZ=0
    g2: LineSegment StartX=-4.2 StartY=0 StartZ=0 EndX=0 EndY=0 EndZ=0
  constraints (8):
    c: Coincident(g0,g1)
    c: Vertical(g1)
    c: Coincident(g1,g2)
    c: Angle(g0,g-1) = 0.523599
    c: Coincident(g0,g2)
    c: PointOnObject(g1,g-1)
    c: DistanceX(g1,g0) = 4.2
    c: Coincident(g0,g-1)
FEATURE [Part::Feature] Part__Feature003  label="hc-sr04"
  Placement = pos=(0,-54.3,-24.1) rot=(0,0,1;3.14159rad)
  shape: bbox 45.2 x 18.55 x 25.81 mm, 1464 faces (baked)
FEATURE [Part::Feature] Part__Feature  label="SW_CuK_OS102011MA1QN1_SPDT_Angled"
  Placement = pos=(27.7,-13.2,1.595) rot=(0,0,1;1.5708rad)
  shape: bbox 8.4 x 8.6 x 7.6 mm, 200 faces (baked)
FEATURE [Part::Feature] Part__Feature958  label="PinHeader_1x04_P2.54mm_Vertical"
  Placement = pos=(-32.8,-0.72,1.595) rot=(0,0,1;1.5708rad)
  shape: bbox 10.16 x 2.54 x 11.54 mm, 100 faces (baked)
FEATURE [Part::Feature] Part__Feature959  label="R_Axial_DIN0207_L6.3mm_D2.5mm_P7.62mm_Horizontal"
  Placement = pos=(8,8.15,1.595) rot=(0,0,1;0rad)
  shape: bbox 8.418 x 2.706 x 5.603 mm, 15 faces (baked)
FEATURE [Part::Feature] Part__Feature960  label="D_DO-41_SOD81_P10.16mm_Horizontal"
  Placement = pos=(27.4,-3.78,1.595) rot=(0,0,1;1.5708rad)
  shape: bbox 2.72 x 11.16 x 5.71 mm, 15 faces (baked)
FEATURE [Part::Feature] Part__Feature961  label="PinHeader_1x10_P2.54mm_Vertical"
  Placement = pos=(11.425,-30,1.595) rot=(0,0,-1;1.5708rad)
  shape: bbox 25.4 x 2.54 x 11.54 mm, 244 faces (baked)
FEATURE [Part::Feature] Part__Feature962  label="PinHeader_1x03_P2.54mm_Vertical"
  Placement = pos=(-18.54,-24.92,1.595) rot=(0,0,1;0rad)
  shape: bbox 2.54 x 7.62 x 11.54 mm, 76 faces (baked)
FEATURE [Part::Feature] Part__Feature963  label="R_Axial_DIN0207_L6.3mm_D2.5mm_P7.62mm_Horizontal001"
  Placement = pos=(-7.98,10.69,1.595) rot=(0,0,1;3.14159rad)
  shape: bbox 8.418 x 2.706 x 5.603 mm, 15 faces (baked)
FEATURE [Part::Feature] Part__Feature964  label="R_Axial_DIN0207_L6.3mm_D2.5mm_P7.62mm_Horizontal002"
  Placement = pos=(-32.8,-5.8,1.595) rot=(0,0,1;0rad)
  shape: bbox 8.418 x 2.706 x 5.603 mm, 15 faces (baked)
FEATURE [Part::Feature] Part__Feature965  label="PinSocket_1x15_P2.54mm_Vertical"
  Placement = pos=(19.812,-3.81,1.595) rot=(0,0,-1;1.5708rad)
  shape: bbox 38.1 x 2.54 x 11.6 mm, 400 faces (baked)
FEATURE [Part::Feature] Part__Feature966  label="arduino_nano"
  Placement = pos=(-18.288,-11.43,10.231) rot=(0,0,1;1.5708rad)
  shape: bbox 45 x 18 x 18.6 mm, 4993 faces (baked)
FEATURE [Part::Feature] Part__Feature967  label="arduino_nano001"
  Placement = pos=(-18.288,-11.43,10.231) rot=(0,0,1;1.5708rad)
  shape: bbox 11.25 x 11.25 x 1.2 mm, 1867 faces (baked)
FEATURE [App::Part] arduino_nano  label="arduino_nano002"
  Group = -> [Part__Feature966,Part__Feature967]
  Origin = -> Origin133
FEATURE [Part::Feature] Part__Feature968  label="R_Axial_DIN0207_L6.3mm_D2.5mm_P7.62mm_Horizontal003"
  Placement = pos=(8,15.77,1.595) rot=(0,0,1;0rad)
  shape: bbox 8.418 x 2.706 x 5.603 mm, 15 faces (baked)
FEATURE [Part::Feature] Part__Feature969  label="PinHeader_1x03_P2.54mm_Vertical001"
  Placement = pos=(-16,-24.92,1.595) rot=(0,0,1;0rad)
  shape: bbox 2.54 x 7.62 x 11.54 mm, 76 faces (baked)
FEATURE [Part::Feature] Part__Feature970  label="PinHeader_1x03_P2.54mm_Vertical002"
  Placement = pos=(-23.62,-24.92,1.595) rot=(0,0,1;0rad)
  shape: bbox 2.54 x 7.62 x 11.54 mm, 76 faces (baked)
FEATURE [Part::Feature] Part__Feature971  label="PinHeader_1x03_P2.54mm_Vertical003"
  Placement = pos=(16,-24.92,1.595) rot=(0,0,1;0rad)
  shape: bbox 2.54 x 7.62 x 11.54 mm, 76 faces (baked)
FEATURE [Part::Feature] Part__Feature972  label="PinHeader_1x03_P2.54mm_Vertical004"
  Placement = pos=(-25.19,-10.6,1.595) rot=(0,0,1;0rad)
  shape: bbox 2.54 x 7.62 x 11.54 mm, 76 faces (baked)
FEATURE [Part::Feature] Part__Feature973  label="Display_OLED-1_3-128X64"
  Placement = pos=(0,14.232,10.595) rot=(0,0,1;0rad)
  shape: bbox 22 x 7.55 x 2.35 mm, 18 faces (baked)
FEATURE [Part::Feature] Part__Feature974  label="Display_OLED-1_3-128X065"
  Placement = pos=(0,14.232,10.595) rot=(0,0,1;0rad)
  shape: bbox 35.65 x 33.6 x 2.6 mm, 215 faces (baked)
FEATURE [Part::Feature] Part__Feature975  label="Display_OLED-1_3-128X066"
  Placement = pos=(0,14.232,10.595) rot=(0,0,1;0rad)
  shape: bbox 10.16 x 2.55 x 11.8 mm, 156 faces (baked)
FEATURE [App::Part] Display_OLED_1_3_128X64  label="Display_OLED-1_3-128X067"
  Group = -> [Part__Feature973,Part__Feature974,Part__Feature975]
  Origin = -> Origin134
FEATURE [Part::Feature] Part__Feature976  label="PinSocket_1x04_P2.54mm_Vertical"
  Placement = pos=(-3.81,29.632,1.595) rot=(0,0,1;1.5708rad)
  shape: bbox 10.16 x 2.54 x 11.6 mm, 114 faces (baked)
FEATURE [Part::Feature] Part__Feature977  label="PinSocket_1x15_P2.54mm_Vertical001"
  Placement = pos=(19.812,-19.05,1.595) rot=(0,0,-1;1.5708rad)
  shape: bbox 38.1 x 2.54 x 11.6 mm, 400 faces (baked)
FEATURE [Part::Feature] Part__Feature978  label="R_Axial_DIN0207_L6.3mm_D2.5mm_P7.62mm_Horizontal004"
  Placement = pos=(-7.98,15.77,1.595) rot=(0,0,1;3.14159rad)
  shape: bbox 8.418 x 2.706 x 5.603 mm, 15 faces (baked)
FEATURE [Part::Feature] Part__Feature979  label="R_Axial_DIN0207_L6.3mm_D2.5mm_P7.62mm_Horizontal005"
  Placement = pos=(-7.98,18.31,1.595) rot=(0,0,1;3.14159rad)
  shape: bbox 8.418 x 2.706 x 5.603 mm, 15 faces (baked)
FEATURE [Part::Feature] Part__Feature980  label="PinHeader_1x03_P2.54mm_Vertical005"
  Placement = pos=(-32.81,-10.6,1.595) rot=(0,0,1;0rad)
  shape: bbox 2.54 x 7.62 x 11.54 mm, 76 faces (baked)
FEATURE [Part::Feature] Part__Feature981  label="R_Axial_DIN0207_L6.3mm_D2.5mm_P7.62mm_Horizontal006"
  Placement = pos=(8,13.23,1.595) rot=(0,0,1;0rad)
  shape: bbox 8.418 x 2.706 x 5.603 mm, 15 faces (baked)
FEATURE [Part::Feature] Part__Feature982  label="PinHeader_1x03_P2.54mm_Vertical006"
  Placement = pos=(-30.27,-10.6,1.595) rot=(0,0,1;0rad)
  shape: bbox 2.54 x 7.62 x 11.54 mm, 76 faces (baked)
FEATURE [Part::Feature] Part__Feature983  label="R_Axial_DIN0207_L6.3mm_D2.5mm_P7.62mm_Horizontal007"
  Placement = pos=(8,18.31,1.595) rot=(0,0,1;0rad)
  shape: bbox 8.418 x 2.706 x 5.603 mm, 15 faces (baked)
FEATURE [Part::Feature] Part__Feature984  label="R_Axial_DIN0207_L6.3mm_D2.5mm_P7.62mm_Horizontal008"
  Placement = pos=(-7.98,13.23,1.595) rot=(0,0,1;3.14159rad)
  shape: bbox 8.418 x 2.706 x 5.603 mm, 15 faces (baked)
FEATURE [Part::Feature] Part__Feature985  label="R_Axial_DIN0207_L6.3mm_D2.5mm_P7.62mm_Horizontal009"
  Placement = pos=(-7.98,8.15,1.595) rot=(0,0,1;3.14159rad)
  shape: bbox 8.418 x 2.706 x 5.603 mm, 15 faces (baked)
FEATURE [Part::Feature] Part__Feature986  label="PinHeader_1x03_P2.54mm_Vertical007"
  Placement = pos=(18.54,-24.92,1.595) rot=(0,0,1;0rad)
  shape: bbox 2.54 x 7.62 x 11.54 mm, 76 faces (baked)
FEATURE [Part::Feature] Part__Feature987  label="R_Axial_DIN0207_L6.3mm_D2.5mm_P7.62mm_Horizontal010"
  Placement = pos=(-32.8,1.82,1.595) rot=(0,0,1;0rad)
  shape: bbox 8.418 x 2.706 x 5.603 mm, 15 faces (baked)
FEATURE [Part::Feature] Part__Feature988  label="PinHeader_1x03_P2.54mm_Vertical008"
  Placement = pos=(-21.08,-24.92,1.595) rot=(0,0,1;0rad)
  shape: bbox 2.54 x 7.62 x 11.54 mm, 76 faces (baked)
FEATURE [Part::Feature] Part__Feature989  label="R_Axial_DIN0207_L6.3mm_D2.5mm_P7.62mm_Horizontal011"
  Placement = pos=(8,10.69,1.595) rot=(0,0,1;0rad)
  shape: bbox 8.418 x 2.706 x 5.603 mm, 15 faces (baked)
FEATURE [Part::Feature] Part__Feature990  label="PinHeader_1x03_P2.54mm_Vertical009"
  Placement = pos=(21.08,-24.92,1.595) rot=(0,0,1;0rad)
  shape: bbox 2.54 x 7.62 x 11.54 mm, 76 faces (baked)
FEATURE [Part::Feature] Part__Feature991  label="PinHeader_1x03_P2.54mm_Vertical010"
  Placement = pos=(-27.73,-10.6,1.595) rot=(0,0,1;0rad)
  shape: bbox 2.54 x 7.62 x 11.54 mm, 76 faces (baked)
FEATURE [Part::Feature] Part__Feature992  label="PinHeader_1x04_P2.54mm_Vertical001"
  Placement = pos=(-32.8,-3.26,1.595) rot=(0,0,1;1.5708rad)
  shape: bbox 10.16 x 2.54 x 11.54 mm, 100 faces (baked)
FEATURE [Part::Feature] Part__Feature993  label="PinHeader_1x03_P2.54mm_Vertical011"
  Placement = pos=(23.62,-24.92,1.595) rot=(0,0,1;0rad)
  shape: bbox 2.54 x 7.62 x 11.54 mm, 76 faces (baked)
FEATURE [Part::Feature] Part__Feature994  label="PinSocket_1x03_P2.54mm_Horizontal_haptic"
  Placement = pos=(2.54,13.3,-0.085) rot=(0.707107,0.707107,0;3.14159rad)
  shape: bbox 7.62 x 10.13 x 5.84 mm, 100 faces (baked)
FEATURE [Part::Feature] Part__Feature995  label="PinSocket_1x03_P2.54mm_Horizontal_haptic001"
  Placement = pos=(2.54,13.3,-0.085) rot=(0.707107,0.707107,0;3.14159rad)
  shape: bbox 21.2 x 23.2 x 1.65 mm, 147 faces (baked)
FEATURE [Part::Feature] Part__Feature996  label="PinSocket_1x03_P2.54mm_Horizontal_haptic002"
  Placement = pos=(2.54,13.3,-0.085) rot=(0.707107,0.707107,0;3.14159rad)
  shape: bbox 2.4 x 2.4 x 2.4 mm, 10 faces (baked)
FEATURE [Part::Feature] Part__Feature997  label="PinSocket_1x03_P2.54mm_Horizontal_haptic003"
  Placement = pos=(2.54,13.3,-0.085) rot=(0.707107,0.707107,0;3.14159rad)
  shape: bbox 0.6 x 7.5 x 6.4 mm, 10 faces (baked)
FEATURE [Part::Feature] Part__Feature998  label="PinSocket_1x03_P2.54mm_Horizontal_haptic004"
  Placement = pos=(2.54,13.3,-0.085) rot=(0.707107,0.707107,0;3.14159rad)
  shape: bbox 2.4 x 2.4 x 2.4 mm, 10 faces (baked)
FEATURE [Part::Feature] Part__Feature999  label="PinSocket_1x03_P2.54mm_Horizontal_haptic005"
  Placement = pos=(2.54,13.3,-0.085) rot=(0.707107,0.707107,0;3.14159rad)
  shape: bbox 0.6 x 7.5 x 6.4 mm, 10 faces (baked)
FEATURE [Part::Feature] Part__Feature1000  label="PinSocket_1x03_P2.54mm_Horizontal_haptic006"
  Placement = pos=(2.54,13.3,-0.085) rot=(0.707107,0.707107,0;3.14159rad)
  shape: bbox 2.4 x 2.4 x 2.4 mm, 10 faces (baked)
FEATURE [Part::Feature] Part__Feature1001  label="PinSocket_1x03_P2.54mm_Horizontal_haptic007"
  Placement = pos=(2.54,13.3,-0.085) rot=(0.707107,0.707107,0;3.14159rad)
  shape: bbox 0.6 x 7.5 x 6.4 mm, 10 faces (baked)
FEATURE [Part::Feature] Part__Feature1002  label="PinSocket_1x03_P2.54mm_Horizontal_haptic008"
  Placement = pos=(2.54,13.3,-0.085) rot=(0.707107,0.707107,0;3.14159rad)
  shape: bbox 10 x 10 x 3.4 mm, 4 faces (baked)
FEATURE [App::Part] PinSocket_1x03_P2_54mm_Horizontal_haptic  label="PinSocket_1x03_P2.54mm_Horizontal_haptic009"
  Group = -> [Part__Feature994,Part__Feature995,Part__Feature996,Part__Feature997,Part__Feature998,Part__Feature999,Part__Feature1000,Part__Feature1001,Part__Feature1002]
  Origin = -> Origin135
FEATURE [Part::Feature] Part__Feature1003  label="PinHeader_1x02_P2.54mm_Horizontal"
  Placement = pos=(30.3,17.4,-0.085) rot=(0.707107,-0.707107,0;3.14159rad)
  shape: bbox 5.08 x 10.36 x 5.54 mm, 58 faces (baked)
FEATURE [Part::Feature] Part__Feature1004  label="TheThing_main_PCB"
  shape: bbox 80 x 64 x 1.51 mm, 290 faces (baked)
FEATURE [App::Part] TheThing_main_1  label="TheThing_main 1"
  Group = -> [Part__Feature,Part__Feature958,Part__Feature959,Part__Feature960,Part__Feature961,Part__Feature962,Part__Feature963,Part__Feature964,Part__Feature965,arduino_nano,Part__Feature968,Part__Feature969,Part__Feature970,Part__Feature971,Part__Feature972,Display_OLED_1_3_128X64,Part__Feature976,Part__Feature977,Part__Feature978,Part__Feature979,Part__Feature980,Part__Feature981,Part__Feature982,+14 more]
  Origin = -> Origin136
  Placement = pos=(0,5.8,13.8) rot=(1,0,0;1.22173rad)
FEATURE [Part::Feature] Part__Feature1005  label="R_Axial_DIN0207_L6.3mm_D2.5mm_P7.62mm_Horizontal012"
  Placement = pos=(-24.6,11.8,1.595) rot=(0,0,1;0rad)
  shape: bbox 8.418 x 2.706 x 5.603 mm, 15 faces (baked)
FEATURE [Part::Feature] Part__Feature1006  label="SW_TS14-1212-120-BK-160-SCR-D"
  Placement = pos=(29.54,4.1,1.595) rot=(0,0,-1;1.5708rad)
  shape: bbox 1 x 1 x 4.5 mm, 24 faces (baked)
FEATURE [Part::Feature] Part__Feature1007  label="SW_TS14-1212-120-BK-160-SCR-D001"
  Placement = pos=(29.54,4.1,1.595) rot=(0,0,-1;1.5708rad)
  shape: bbox 10.4 x 10.4 x 0.2 mm, 20 faces (baked)
FEATURE [Part::Feature] Part__Feature1008  label="SW_TS14-1212-120-BK-160-SCR-D002"
  Placement = pos=(29.54,4.1,1.595) rot=(0,0,-1;1.5708rad)
  shape: bbox 12 x 12 x 12 mm, 59 faces (baked)
FEATURE [Part::Feature] Part__Feature1009  label="SW_TS14-1212-120-BK-160-SCR-D003"
  Placement = pos=(29.54,4.1,1.595) rot=(0,0,-1;1.5708rad)
  shape: bbox 1 x 1 x 4.5 mm, 24 faces (baked)
FEATURE [Part::Feature] Part__Feature1010  label="SW_TS14-1212-120-BK-160-SCR-D004"
  Placement = pos=(29.54,4.1,1.595) rot=(0,0,-1;1.5708rad)
  shape: bbox 1 x 1 x 4.5 mm, 24 faces (baked)
FEATURE [Part::Feature] Part__Feature1011  label="SW_TS14-1212-120-BK-160-SCR-D005"
  Placement = pos=(29.54,4.1,1.595) rot=(0,0,-1;1.5708rad)
  shape: bbox 1 x 1 x 4.5 mm, 24 faces (baked)
FEATURE [App::Part] SW_TS14_1212_120_BK_160_SCR_D  label="SW_TS14-1212-120-BK-160-SCR-D006"
  Group = -> [Part__Feature1006,Part__Feature1007,Part__Feature1008,Part__Feature1009,Part__Feature1010,Part__Feature1011]
  Origin = -> Origin137
FEATURE [Part::Feature] Part__Feature1012  label="R_Axial_DIN0207_L6.3mm_D2.5mm_P7.62mm_Horizontal013"
  Placement = pos=(17,11.8,1.595) rot=(0,0,1;0rad)
  shape: bbox 8.418 x 2.706 x 5.603 mm, 15 faces (baked)
FEATURE [Part::Feature] Part__Feature1013  label="R_LDR_4.2x3.5mm_P2.54mm_Vertical"
  Placement = pos=(-17.018,-1.508,1.595) rot=(0,0,1;1.5708rad)
  shape: bbox 3.5 x 4.2 x 7 mm, 14 faces (baked)
FEATURE [Part::Feature] Part__Feature1014  label="R_LDR_4.2x3.5mm_P2.54mm_Vertical001"
  Placement = pos=(-17.018,-1.508,1.595) rot=(0,0,1;1.5708rad)
  shape: bbox 3.15 x 2.1 x 0.05 mm, 42 faces (baked)
FEATURE [App::Part] R_LDR_4_2x3_5mm_P2_54mm_Vertical  label="R_LDR_4.2x3.5mm_P2.54mm_Vertical002"
  Group = -> [Part__Feature1013,Part__Feature1014]
  Origin = -> Origin138
FEATURE [Part::Feature] Part__Feature1015  label="Trimpot_THT"
  Placement = pos=(14.22,-6.094,4.795) rot=(0,0,1;3.14159rad)
  shape: bbox 6.42 x 5.646 x 1.8 mm, 24 faces (baked)
FEATURE [Part::Feature] Part__Feature1016  label="Trimpot_THT001"
  Placement = pos=(14.22,-6.094,4.795) rot=(0,0,1;3.14159rad)
  shape: bbox 6.48 x 7.2 x 9.25 mm, 92 faces (baked)
FEATURE [App::Part] Trimpot_THT  label="Trimpot_THT002"
  Group = -> [Part__Feature1015,Part__Feature1016]
  Origin = -> Origin139
FEATURE [Part::Feature] Part__Feature1017  label="C_Disc_D3.0mm_W2.0mm_P2.50mm"
  Placement = pos=(-11.43,-2.25,1.595) rot=(0,0,1;1.5708rad)
  shape: bbox 2 x 3 x 5.1 mm, 12 faces (baked)
FEATURE [Part::Feature] Part__Feature1018  label="TO-92"
  Placement = pos=(12.68,2.03,1.595) rot=(0,0,1;0rad)
  shape: bbox 4.83 x 3.745 x 9.8 mm, 23 faces (baked)
FEATURE [Part::Feature] Part__Feature1019  label="D_DO-41_SOD81_P10.16mm_Horizontal001"
  Placement = pos=(-8.382,-6.08,1.595) rot=(0,0,1;1.5708rad)
  shape: bbox 2.72 x 11.16 x 5.71 mm, 15 faces (baked)
FEATURE [Part::Feature] Part__Feature1020  label="R_Axial_DIN0207_L6.3mm_D2.5mm_P7.62mm_Horizontal014"
  Placement = pos=(-17,8.3,1.595) rot=(0,0,1;3.14159rad)
  shape: bbox 8.418 x 2.706 x 5.603 mm, 15 faces (baked)
FEATURE [Part::Feature] Part__Feature1021  label="SW_TS14-1212-120-BK-160-SCR-D007"
  Placement = pos=(-29.54,-8.5,1.595) rot=(0,0,1;1.5708rad)
  shape: bbox 1 x 1 x 4.5 mm, 24 faces (baked)
FEATURE [Part::Feature] Part__Feature1022  label="SW_TS14-1212-120-BK-160-SCR-D008"
  Placement = pos=(-29.54,-8.5,1.595) rot=(0,0,1;1.5708rad)
  shape: bbox 10.4 x 10.4 x 0.2 mm, 20 faces (baked)
FEATURE [Part::Feature] Part__Feature1023  label="SW_TS14-1212-120-BK-160-SCR-D009"
  Placement = pos=(-29.54,-8.5,1.595) rot=(0,0,1;1.5708rad)
  shape: bbox 12 x 12 x 12 mm, 59 faces (baked)
FEATURE [Part::Feature] Part__Feature1024  label="SW_TS14-1212-120-BK-160-SCR-D010"
  Placement = pos=(-29.54,-8.5,1.595) rot=(0,0,1;1.5708rad)
  shape: bbox 1 x 1 x 4.5 mm, 24 faces (baked)
FEATURE [Part::Feature] Part__Feature1025  label="SW_TS14-1212-120-BK-160-SCR-D011"
  Placement = pos=(-29.54,-8.5,1.595) rot=(0,0,1;1.5708rad)
  shape: bbox 1 x 1 x 4.5 mm, 24 faces (baked)
FEATURE [Part::Feature] Part__Feature1026  label="SW_TS14-1212-120-BK-160-SCR-D012"
  Placement = pos=(-29.54,-8.5,1.595) rot=(0,0,1;1.5708rad)
  shape: bbox 1 x 1 x 4.5 mm, 24 faces (baked)
FEATURE [App::Part] SW_TS14_1212_120_BK_160_SCR_D001  label="SW_TS14-1212-120-BK-160-SCR-D013"
  Group = -> [Part__Feature1021,Part__Feature1022,Part__Feature1023,Part__Feature1024,Part__Feature1025,Part__Feature1026]
  Origin = -> Origin140
FEATURE [Part::Feature] Part__Feature1027  label="Buzzer_D12_P6.5_WT-1205"
  Placement = pos=(-0.01,4.334,1.595) rot=(0,0,1;1.5708rad)
  shape: bbox 0.6 x 0.6 x 3.8 mm, 4 faces (baked)
FEATURE [Part::Feature] Part__Feature1028  label="Buzzer_D12_P6.5_WT-1206"
  Placement = pos=(-0.01,4.334,1.595) rot=(0,0,1;1.5708rad)
  shape: bbox 0.6 x 0.6 x 3.8 mm, 4 faces (baked)
FEATURE [Part::Feature] Part__Feature1029  label="Buzzer_D12_P6.5_WT-1207"
  Placement = pos=(-0.01,4.334,1.595) rot=(0,0,1;1.5708rad)
  shape: bbox 0.01 x 1.746 x 1.746 mm, 14 faces (baked)
FEATURE [Part::Feature] Part__Feature1030  label="Buzzer_D12_P6.5_WT-1208"
  Placement = pos=(-0.01,4.334,1.595) rot=(0,0,1;1.5708rad)
  shape: bbox 12.99 x 12.99 x 9.5 mm, 112 faces (baked)
FEATURE [App::Part] Buzzer_D12_P6_5_WT_1205  label="Buzzer_D12_P6.5_WT-1209"
  Group = -> [Part__Feature1027,Part__Feature1028,Part__Feature1029,Part__Feature1030]
  Origin = -> Origin141
FEATURE [Part::Feature] Part__Feature1031  label="R_Axial_DIN0207_L6.3mm_D2.5mm_P7.62mm_Horizontal015"
  Placement = pos=(17,8.3,1.595) rot=(0,0,1;0rad)
  shape: bbox 8.418 x 2.706 x 5.603 mm, 15 faces (baked)
FEATURE [Part::Feature] Part__Feature1032  label="PinSocket_1x04_P2.54mm_Vertical001"
  Placement = pos=(3.81,-3.794,-0.085) rot=(0.707107,0.707107,0;3.14159rad)
  shape: bbox 10.16 x 2.54 x 11.6 mm, 114 faces (baked)
FEATURE [Part::Feature] Part__Feature1033  label="PinHeader_1x10_P2.54mm_Vertical001"
  Placement = pos=(11.42,12.462,-0.085) rot=(0.707107,0.707107,0;3.14159rad)
  shape: bbox 25.4 x 2.54 x 11.54 mm, 244 faces (baked)
FEATURE [Part::Feature] Part__Feature1034  label="TheThing_addon_PCB"
  shape: bbox 75.2 x 29.6 x 1.51 mm, 128 faces (baked)
FEATURE [App::Part] TheThing_addon_1  label="TheThing_addon 1"
  Group = -> [Part__Feature1005,SW_TS14_1212_120_BK_160_SCR_D,Part__Feature1012,R_LDR_4_2x3_5mm_P2_54mm_Vertical,Trimpot_THT,Part__Feature1017,Part__Feature1018,Part__Feature1019,Part__Feature1020,SW_TS14_1212_120_BK_160_SCR_D001,Buzzer_D12_P6_5_WT_1205,Part__Feature1031,Part__Feature1032,Part__Feature1033,Part__Feature1034]
  Origin = -> Origin142
  Placement = pos=(0,-45.3,-6) rot=(0,0,1;0rad)
FEATURE [App::DocumentObjectGroup] Group001  label="Electronic_Parts"
  Group = -> [TheThing_v8_main,TheThing_v8_addon,Part__Feature003,User_Library_9V_Duracell_Battery,_68005_cp005_cp,TheThing_main_1,TheThing_addon_1]
FEATURE [PartDesign::Line] DatumLine
  AttacherType = Attacher::AttachEngineLine
  Length = 20
  MapMode = 19
  Placement = pos=(13.98,-50.184,18.345) rot=(0,0,1;2.0944rad)
  ResizeMode = 0
FEATURE [PartDesign::SubShapeBinder] Binder058  label="Binder058(Trimpot_THT002)"
  BindCopyOnChange = 0
  BindMode = 0
  ClaimChildren = false
  Context = -> Group002 [Body021.Binder058.]
  Fuse = false
  MakeFace = true
  OffsetFill = false
  OffsetIntersection = false
  OffsetJoinType = 0
  OffsetOpenResult = false
  PartialLoad = false
  Relative = true
  Support = -> [TheThing_addon_1[Trimpot_THT.]]
  _Version = 8
FEATURE [Sketcher::SketchObject] Sketch055
  ArcFitTolerance = 1e-06
  AttachmentSupport = -> [Binder058]
  ExternalGeometry = -> [Binder058]
  FullyConstrained = true
  MakeInternals = false
  MapMode = 5
  Placement = pos=(0,0,3.145) rot=(0,0,1;0rad)
  sketch-geometry (4):
    g0: ArcOfCircle CenterX=13.98 CenterY=-50.184 CenterZ=0 NormalX=0 NormalY=0 NormalZ=1 AngleXU=0 Radius=3.275 StartAngle=2.2312 EndAngle=7.19358
    g1: LineSegment StartX=11.971 StartY=-47.5976 StartZ=0 EndX=15.989 EndY=-47.5976 EndZ=0
    g2: Circle CenterX=13.98 CenterY=-50.184 CenterZ=0 NormalX=0 NormalY=0 NormalZ=1 AngleXU=0 Radius=5.8
    g3: Circle [constr] CenterX=13.98 CenterY=-50.184 CenterZ=0 NormalX=0 NormalY=0 NormalZ=1 AngleXU=0 Radius=5.1
  constraints (10):
    c: Coincident(g1,g0)
    c: Coincident(g1,g0)
    c: Horizontal(g1)
    c: Diameter(g0) = 6.55
    c: Diameter(g2) = 11.6
    c: Coincident(g2,g0)
    c: Diameter(g3) = 10.2
    c: Coincident(g3,g0)
    c: Coincident(g0,g-3)
    c: Distance(g0,g-4) = 0.15
FEATURE [PartDesign::Pad] Pad036
  Direction = (0,0,1)
  Length = 1.75
  Length2 = 0.2
  Profile = -> Sketch055
  ReferenceAxis = -> Sketch055 [N_Axis]
  Refine = true
  Reversed = true
  Suppressed = false
  Type = 0
FEATURE [Sketcher::SketchObject] Sketch056
  ArcFitTolerance = 1e-06
  ExternalGeometry = -> [Pad036]
  FullyConstrained = true
  MakeInternals = false
  MapMode = 5
  Placement = pos=(0,0,1.395) rot=(1,0,0;3.14159rad)
  sketch-geometry (2):
    g0: Circle CenterX=13.98 CenterY=50.184 CenterZ=0 NormalX=0 NormalY=0 NormalZ=1 AngleXU=0 Radius=5.8
    g1: Circle CenterX=13.98 CenterY=50.184 CenterZ=0 NormalX=0 NormalY=0 NormalZ=1 AngleXU=0 Radius=5.1
  constraints (4):
    c: Coincident(g0,g-3)
    c: Equal(g0,g-3)
    c: Diameter(g1) = 10.2
    c: Coincident(g1,g0)
FEATURE [PartDesign::Pad] Pad037
  BaseFeature = -> Pad036
  Direction = (0,-1e-16,-1)
  Length = 6
  Length2 = 10
  Profile = -> Sketch056
  ReferenceAxis = -> Sketch056 [N_Axis]
  Refine = true
  Suppressed = false
  Type = 0
FEATURE [Sketcher::SketchObject] Sketch057
  ArcFitTolerance = 1e-06
  AttachmentSupport = -> [Pad037]
  ExternalGeometry = -> [Pad037]
  FullyConstrained = false
  MakeInternals = false
  MapMode = 5
  Placement = pos=(0,0,3.145) rot=(0,0,1;0rad)
  sketch-geometry (1):
    g0: Circle CenterX=13.98 CenterY=-50.184 CenterZ=0 NormalX=0 NormalY=0 NormalZ=1 AngleXU=0 Radius=7.5
  constraints (1):
    c: Diameter(g0) = 15
FEATURE [PartDesign::Pad] Pad038
  BaseFeature = -> Pad037
  Direction = (0,0,1)
  Length = 5
  Length2 = 10
  Profile = -> Sketch057
  ReferenceAxis = -> Sketch057 [N_Axis]
  Refine = true
  Suppressed = false
  Type = 0
FEATURE [Sketcher::SketchObject] Sketch060
  ArcFitTolerance = 1e-06
  AttachmentSupport = -> [Pad038]
  ExternalGeometry = -> [Pad038]
  FullyConstrained = true
  MakeInternals = false
  MapMode = 5
  Placement = pos=(0,0,8.145) rot=(0,0,1;0rad)
  sketch-geometry (1):
    g0: Circle CenterX=13.98 CenterY=-50.184 CenterZ=0 NormalX=0 NormalY=0 NormalZ=1 AngleXU=0 Radius=5.1
  constraints (2):
    c: Coincident(g0,g-3)
    c: Equal(g-3,g0)
FEATURE [PartDesign::Pad] Pad039
  BaseFeature = -> Pad038
  Direction = (0,0,1)
  Length = 10
  Length2 = 10
  Profile = -> Sketch060
  ReferenceAxis = -> Sketch060 [N_Axis]
  Refine = true
  Suppressed = false
  Type = 0
FEATURE [Sketcher::SketchObject] Sketch059
  ArcFitTolerance = 1e-06
  AttachmentSupport = -> [Pad039]
  ExternalGeometry = -> [Pad039]
  FullyConstrained = true
  MakeInternals = false
  MapMode = 5
  Placement = pos=(0,0,8.145) rot=(0,0,1;0rad)
  sketch-geometry (6):
    g0: LineSegment [constr] StartX=13.98 StartY=-50.184 StartZ=0 EndX=13.98 EndY=-57.6737 EndZ=0
    g1: LineSegment StartX=13.5875 StartY=-57.6737 StartZ=0 EndX=14.3725 EndY=-57.6737 EndZ=0
    g2: LineSegment StartX=14.3725 StartY=-57.6737 StartZ=0 EndX=13.98 EndY=-58.3536 EndZ=0
    g3: LineSegment StartX=13.98 StartY=-58.3536 StartZ=0 EndX=13.5875 EndY=-57.6737 EndZ=0
    g4: LineSegment [constr] StartX=13.5875 StartY=-57.6737 StartZ=0 EndX=13.98 EndY=-50.184 EndZ=0
    g5: LineSegment [constr] StartX=13.98 StartY=-50.184 StartZ=0 EndX=14.3725 EndY=-57.6737 EndZ=0
  constraints (15):
    c: Coincident(g1,g2)
    c: Coincident(g2,g3)
    c: Coincident(g3,g1)
    c: Symmetric(g1,g1,g0)
    c: Coincident(g4,g1)
    c: Coincident(g4,g0)
    c: Coincident(g5,g0)
    c: Coincident(g5,g1)
    c: PointOnObject(g0,g1)
    c: Vertical(g0)
    c: PointOnObject(g1,g-3)
    c: Equal(g3,g1)
    c: Equal(g2,g1)
    c: Angle(g4,g5) = 0.10472
    c: Coincident(g0,g-3)
FEATURE [PartDesign::Pad] Pad040
  AlongSketchNormal = false
  BaseFeature = -> Pad039
  Direction = (0,0,1)
  Length = 10
  Length2 = 10
  Profile = -> Sketch059
  ReferenceAxis = -> Sketch059 [N_Axis]
  Refine = true
  Reversed = true
  Suppressed = false
  Type = 3
  UpToFace = -> Pad039 [Face8]
FEATURE [PartDesign::PolarPattern] PolarPattern001
  Angle = 360
  Axis = -> Pad040 [Edge22]
  BaseFeature = -> Pad040
  Mode = 0
  Occurrences = 60
  Offset = 120
  Originals = -> [Pad040]
  Refine = true
  Suppressed = false
  TransformMode = 0
FEATURE [PartDesign::Groove] Groove
  Angle = 360
  Angle2 = 60
  Axis = (0,0,1)
  Base = (13.98,-50.184,18.345)
  BaseFeature = -> PolarPattern001
  Profile = -> Sketch061
  ReferenceAxis = -> DatumLine
  Refine = true
  Reversed = true
  Suppressed = false
  Type = 0
FEATURE [PartDesign::Chamfer] Chamfer004
  Angle = 45
  Base = -> Groove [Edge368]
  BaseFeature = -> Groove
  ChamferType = 0
  FlipDirection = false
  Refine = true
  Size = 0.5
  Size2 = 1
  SupportTransform = false
  Suppressed = false
  UseAllEdges = false
FEATURE [Sketcher::SketchObject] Sketch062
  ArcFitTolerance = 1e-06
  ExternalGeometry = -> [Chamfer004]
  FullyConstrained = true
  MakeInternals = false
  MapMode = 5
  Placement = pos=(0,0,18.345) rot=(0,0,1;0rad)
  sketch-geometry (1):
    g0: LineSegment StartX=13.98 StartY=-50.184 StartZ=0 EndX=13.98 EndY=-43.784 EndZ=0
  constraints (3):
    c: Vertical(g0)
    c: DistanceY(g0,g0) = 6.4
    c: Coincident(g0,g-3)
FEATURE [Sketcher::SketchObject] Sketch063
  ArcFitTolerance = 1e-06
  AttachmentSupport = -> [DatumPlane010]
  ExternalGeometry = -> [Chamfer004]
  FullyConstrained = true
  MakeInternals = false
  MapMode = 5
  Placement = pos=(13.98,-50.184,18.345) rot=(1,0,0;1.5708rad)
  sketch-geometry (4):
    g0: LineSegment StartX=0 StartY=-0.7 StartZ=0 EndX=0.5 EndY=0.166025 EndZ=0
    g1: LineSegment StartX=0.5 StartY=0.166025 StartZ=0 EndX=-0.5 EndY=0.166025 EndZ=0
    g2: LineSegment StartX=-0.5 StartY=0.166025 StartZ=0 EndX=0 EndY=-0.7 EndZ=0
    g3: Circle [constr] CenterX=-4e-16 CenterY=-0.12265 CenterZ=0 NormalX=0 NormalY=0 NormalZ=1 AngleXU=0 Radius=0.57735
  constraints (12):
    c: Coincident(g0,g1)
    c: Coincident(g1,g2)
    c: Coincident(g2,g0)
    c: Equal(g0,g1)
    c: Equal(g0,g2)
    c: PointOnObject(g0,g3)
    c: PointOnObject(g1,g3)
    c: PointOnObject(g2,g3)
    c: PointOnObject(g0,g-2)
    c: Horizontal(g1)
    c: DistanceX(g1,g1) = 1
    c: PointOnObject(g0,g-3)
FEATURE [PartDesign::SubtractivePipe] SubtractivePipe
  AuxilleryCurvelinear = true
  AuxillerySpineTangent = false
  BaseFeature = -> Chamfer004
  Binormal = (0,0,0)
  Mode = 0
  Profile = -> Sketch063
  Refine = true
  Spine = -> Sketch062 [Edge1]
  SpineTangent = false
  Suppressed = false
  Transformation = 0
  Transition = 0
FEATURE [PartDesign::SubShapeBinder] Binder059  label="Binder059(TO-92)"
  BindCopyOnChange = 0
  BindMode = 0
  ClaimChildren = false
  Context = -> Group002 [Body021.Binder059.]
  Fuse = false
  MakeFace = true
  OffsetFill = false
  OffsetIntersection = false
  OffsetJoinType = 0
  OffsetOpenResult = false
  PartialLoad = false
  Relative = true
  Support = -> [TheThing_addon_1[Part__Feature1018.]]
  _Version = 8
FEATURE [PartDesign::SubShapeBinder] Binder060  label="Binder060(TheThing_addon_PCB)"
  BindCopyOnChange = 0
  BindMode = 0
  ClaimChildren = false
  Context = -> Group002 [Body021.Binder060.]
  Fuse = false
  MakeFace = true
  OffsetFill = false
  OffsetIntersection = false
  OffsetJoinType = 0
  OffsetOpenResult = false
  PartialLoad = false
  Relative = true
  Support = -> [TheThing_addon_1[Part__Feature1034.]]
  _Version = 8
FEATURE [PartDesign::Body] Body021  label="trimpot_knob_v3"
  AllowCompound = false
  Group = -> [Sketch055,Pad036,Sketch056,Pad037,Sketch057,Pad038,Sketch059,Sketch060,Pad039,Pad040,PolarPattern001,DatumPlane009,Sketch061,Groove,Chamfer004,Sketch062,DatumPlane010,Sketch063,SubtractivePipe,DatumLine,Binder058,Binder059,Binder060]
  Origin = -> Origin132
  Tip = -> SubtractivePipe
FEATURE [App::DocumentObjectGroup] Group002  label="3DP_parts"
  Group = -> [Part__Feature001,Part__Feature002,Body021]
FEATURE [PartDesign::SubShapeBinder] Binder061  label="Binder061(PinSocket_1x02_P2.54mm_Vertical)"
  BindCopyOnChange = 0
  BindMode = 0
  ClaimChildren = false
  Context = -> Group004 [Body011.Binder061.]
  Fuse = false
  MakeFace = true
  OffsetFill = false
  OffsetIntersection = false
  OffsetJoinType = 0
  OffsetOpenResult = false
  PartialLoad = false
  Relative = true
  Support = -> [Solid]
  _Version = 8
FEATURE [Sketcher::SketchObject] Sketch011
  ArcFitTolerance = 1e-06
  AttachmentSupport = -> [DatumPlane007]
  ExternalGeometry = -> [Binder061]
  FullyConstrained = true
  MakeInternals = false
  MapMode = 5
  Placement = pos=(11,16.532,-17.5055) rot=(0,0,-1;1.5708rad)
  sketch-geometry (4):
    g0: ArcOfCircle CenterX=8 CenterY=4.23 CenterZ=0 NormalX=0 NormalY=0 NormalZ=1 AngleXU=0 Radius=4.23 StartAngle=4.71239 EndAngle=7.61553
    g1: ArcOfCircle CenterX=12.254 CenterY=21.7304 CenterZ=0 NormalX=0 NormalY=0 NormalZ=1 AngleXU=0 Radius=13.78 StartAngle=3.84079 EndAngle=4.47393
    g2: ArcOfCircle CenterX=5.29691 CenterY=15.88 CenterZ=0 NormalX=0 NormalY=0 NormalZ=1 AngleXU=0 Radius=4.69 StartAngle=1.5708 EndAngle=3.84079
    g3: LineSegment [constr] StartX=5.29691 StartY=21.24 StartZ=0 EndX=5.29691 EndY=19.9 EndZ=0
  constraints (11):
    c: Tangent(g0,g1) = 1.5708
    c: Tangent(g1,g2) = -1.5708
    c: Coincident(g3,g-3)
    c: Perpendicular(g2,g3)
    c: Coincident(g3,g-4)
    c: Tangent(g0,g-1) = -1.5708
    c: Radius(g0) = 4.23
    c: Radius(g1) = 13.78
    c: Radius(g2) = 4.69
    c: DistanceX(g-1,g0) = 8
    c: Symmetric(g-4,g-3,g2)
FEATURE [Sketcher::SketchObject] Sketch012
  ArcFitTolerance = 1e-06
  AttachmentSupport = -> [DatumPlane008]
  ExternalGeometry = -> [Binder061,Sketch011]
  FullyConstrained = true
  MakeInternals = false
  MapMode = 5
  Placement = pos=(31.61,3.25e-14,6e-16) rot=(0.57735,0.57735,0.57735;2.0944rad)
  sketch-geometry (3):
    g0: LineSegment StartX=15.9251 StartY=-17.5055 StartZ=0 EndX=7.55999 EndY=-17.5055 EndZ=0
    g1: ArcOfCircle CenterX=7.55999 CenterY=-9.50551 CenterZ=0 NormalX=0 NormalY=0 NormalZ=1 AngleXU=0 Radius=8 StartAngle=2.79253 EndAngle=4.71239
    g2: LineSegment StartX=0.0424531 StartY=-6.76935 StartZ=0 EndX=8.96016 EndY=17.7319 EndZ=0
  constraints (7):
    c: Horizontal(g0)
    c: Tangent(g0,g1) = 1.5708
    c: Tangent(g1,g2) = 1.5708
    c: Symmetric(g-3,g-3,g2)
    c: Perpendicular(g2,g-3)
    c: Radius(g1) = 8
    c: Coincident(g-4,g0)
FEATURE [PartDesign::SubShapeBinder] Binder062  label="Binder062(9V_conn)"
  BindCopyOnChange = 0
  BindMode = 0
  ClaimChildren = false
  Context = -> Group004 [Body011.Binder062.]
  Fuse = false
  MakeFace = true
  OffsetFill = false
  OffsetIntersection = false
  OffsetJoinType = 0
  OffsetOpenResult = false
  PartialLoad = false
  Relative = true
  Support = -> [_68005_cp005_cp]
  _Version = 8
FEATURE [Sketcher::SketchObject] Sketch008
  ArcFitTolerance = 1e-06
  AttachmentSupport = -> [Binder062]
  ExternalGeometry = -> [Binder062]
  FullyConstrained = true
  MakeInternals = false
  MapMode = 5
  Placement = pos=(4.3e-15,2.23e-14,-19.2055) rot=(0,0,1;0rad)
  sketch-geometry (19):
    g0: ArcOfCircle CenterX=1.23825 CenterY=26.8446 CenterZ=0 NormalX=0 NormalY=0 NormalZ=1 AngleXU=0 Radius=1 StartAngle=3.39427 EndAngle=6.03051
    g1: LineSegment StartX=2.47649 StartY=26.5946 StartZ=0 EndX=2.47649 EndY=27.0946 EndZ=0
    g2: LineSegment StartX=2.47649 StartY=27.0946 StartZ=0 EndX=2.20649 EndY=27.0946 EndZ=0
    g3: LineSegment StartX=0 StartY=27.0946 StartZ=0 EndX=0 EndY=26.5946 EndZ=0
    g4: LineSegment StartX=0 StartY=26.5946 StartZ=0 EndX=0.27 EndY=26.5946 EndZ=0
    g5: GeomPoint [constr] X=1.23825 Y=26.8446 Z=0
    g6: ArcOfCircle CenterX=1.23825 CenterY=26.8446 CenterZ=0 NormalX=0 NormalY=0 NormalZ=1 AngleXU=0 Radius=1 StartAngle=0.25268 EndAngle=2.88891
    g7: LineSegment StartX=0.27 StartY=27.0946 StartZ=0 EndX=0 EndY=27.0946 EndZ=0
    g8: LineSegment StartX=2.20649 StartY=26.5946 StartZ=0 EndX=2.47649 EndY=26.5946 EndZ=0
    g9: LineSegment [constr] StartX=2.47649 StartY=26.8446 StartZ=0 EndX=-2.47649 EndY=26.8446 EndZ=0
    g10: ArcOfCircle [constr] CenterX=-1.23825 CenterY=26.8446 CenterZ=0 NormalX=0 NormalY=0 NormalZ=1 AngleXU=0 Radius=1 StartAngle=3.39427 EndAngle=6.03051
    g11: LineSegment [constr] StartX=0 StartY=26.5946 StartZ=0 EndX=0 EndY=27.0946 EndZ=0
    g12: LineSegment [constr] StartX=0 StartY=27.0946 StartZ=0 EndX=-0.27 EndY=27.0946 EndZ=0
    g13: LineSegment [constr] StartX=-2.47649 StartY=27.0946 StartZ=0 EndX=-2.47649 EndY=26.5946 EndZ=0
    g14: LineSegment [constr] StartX=-2.47649 StartY=26.5946 StartZ=0 EndX=-2.20649 EndY=26.5946 EndZ=0
    g15: GeomPoint [constr] X=-1.23825 Y=26.8446 Z=0
    g16: LineSegment [constr] StartX=-2.20649 StartY=27.0946 StartZ=0 EndX=-2.47649 EndY=27.0946 EndZ=0
    g17: ArcOfCircle [constr] CenterX=-1.23825 CenterY=26.8446 CenterZ=0 NormalX=0 NormalY=0 NormalZ=1 AngleXU=0 Radius=1 StartAngle=0.25268 EndAngle=2.88891
    g18: LineSegment [constr] StartX=-0.27 StartY=26.5946 StartZ=0 EndX=0 EndY=26.5946 EndZ=0
  constraints (50):
    c: Coincident(g1,g2)
    c: Coincident(g7,g3)
    c: Coincident(g3,g4)
    c: Coincident(g8,g1)
    c: Horizontal(g2)
    c: Horizontal(g4)
    c: Vertical(g1)
    c: Vertical(g3)
    c: Symmetric(g7,g1,g5)
    c: Coincident(g5,g0)
    c: Diameter(g0) = 2
    c: DistanceY(g3,g3) = 0.5
    c: Equal(g0,g6)
    c: Coincident(g0,g6)
    c: Coincident(g2,g6)
    c: Coincident(g7,g6)
    c: Coincident(g4,g0)
    c: Coincident(g8,g0)
    c: Horizontal(g7)
    c: Horizontal(g8)
    c: Equal(g7,g2)
    c: DistanceX(g7,g7) = 0.27
    c: Symmetric(g1,g1,g9)
    c: Coincident(g11,g12)
    c: Coincident(g16,g13)
    c: Coincident(g13,g14)
    c: Coincident(g18,g11)
    c: Horizontal(g12)
    c: Horizontal(g14)
    c: Vertical(g11)
    c: Vertical(g13)
    c: Symmetric(g16,g11,g15)
    c: Coincident(g15,g10)
    c: Coincident(g16,g17)
    c: Equal(g10,g17)
    c: Coincident(g17,g12)
    c: Coincident(g10,g17)
    c: Coincident(g14,g10)
    c: Coincident(g18,g10)
    c: Horizontal(g16)
    c: Horizontal(g18)
    c: Equal(g12,g16)
    c: Equal(g13,g11)
    c: Equal(g17,g6)
    c: Equal(g12,g7)
    c: Equal(g11,g3)
    c: PointOnObject(g7,g-2)
    c: Coincident(g12,g7)
    c: Symmetric(g13,g13,g9)
    c: Symmetric(g-3,g-3,g9)
FEATURE [Sketcher::SketchObject] Sketch009
  ArcFitTolerance = 1e-06
  ExternalGeometry = -> [Sketch008]
  FullyConstrained = true
  MakeInternals = false
  MapMode = 5
  Placement = pos=(6.1e-15,26.832,3.28e-14) rot=(0,0.707107,0.707107;3.14159rad)
  sketch-geometry (3):
    g0: LineSegment StartX=-3.73e-14 StartY=-19.2055 StartZ=0 EndX=-3.73e-14 EndY=-13.2055 EndZ=0
    g1: ArcOfCircle CenterX=-5.5 CenterY=-13.2055 CenterZ=0 NormalX=0 NormalY=0 NormalZ=1 AngleXU=0 Radius=5.5 StartAngle=1.88e-14 EndAngle=3.14159
    g2: LineSegment StartX=-11 StartY=-13.2055 StartZ=0 EndX=-11 EndY=-14.0055 EndZ=0
  constraints (8):
    c: Vertical(g0)
    c: Tangent(g0,g1) = -1.5708
    c: Angle(g1) = 3.14159
    c: Tangent(g1,g2) = -1.5708
    c: DistanceY(g0,g0) = 6
    c: Radius(g1) = 5.5
    c: DistanceY(g2,g2) = 0.8
    c: Coincident(g0,g-3)
FEATURE [Sketcher::SketchObject] Sketch010
  ArcFitTolerance = 1e-06
  ExternalGeometry = -> [Sketch009]
  FullyConstrained = true
  MakeInternals = false
  MapMode = 5
  Placement = pos=(11,26.832,-13.2055) rot=(0.57735,0.57735,0.57735;2.0944rad)
  sketch-geometry (3):
    g0: LineSegment StartX=0 StartY=-0.8 StartZ=0 EndX=0 EndY=-2 EndZ=0
    g1: ArcOfCircle CenterX=-2.3 CenterY=-2 CenterZ=0 NormalX=0 NormalY=0 NormalZ=1 AngleXU=0 Radius=2.3 StartAngle=4.71239 EndAngle=6.28319
    g2: LineSegment StartX=-2.3 StartY=-4.3 StartZ=0 EndX=-18.3 EndY=-4.3 EndZ=0
  constraints (8):
    c: Coincident(g-3,g0)
    c: PointOnObject(g0,g-2)
    c: Tangent(g0,g1) = 1.5708
    c: Angle(g1) = 1.5708
    c: Tangent(g1,g2) = 1.5708
    c: DistanceY(g0,g0) = 1.2
    c: Radius(g1) = 2.3
    c: DistanceX(g2,g2) = 16
FEATURE [Sketcher::SketchObject] Sketch013
  ArcFitTolerance = 1e-06
  ExternalGeometry = -> [Binder062]
  FullyConstrained = true
  MakeInternals = false
  MapMode = 5
  Placement = pos=(0,2.34e-14,-19.2055) rot=(0,0,1;0rad)
  sketch-geometry (19):
    g0: ArcOfCircle [constr] CenterX=1.23825 CenterY=26.8446 CenterZ=0 NormalX=0 NormalY=0 NormalZ=1 AngleXU=0 Radius=1 StartAngle=3.39427 EndAngle=6.03051
    g1: LineSegment [constr] StartX=2.47649 StartY=26.5946 StartZ=0 EndX=2.47649 EndY=27.0946 EndZ=0
    g2: LineSegment [constr] StartX=2.47649 StartY=27.0946 StartZ=0 EndX=2.20649 EndY=27.0946 EndZ=0
    g3: LineSegment StartX=0 StartY=27.0946 StartZ=0 EndX=0 EndY=26.5946 EndZ=0
    g4: LineSegment [constr] StartX=0 StartY=26.5946 StartZ=0 EndX=0.27 EndY=26.5946 EndZ=0
    g5: GeomPoint [constr] X=1.23825 Y=26.8446 Z=0
    g6: ArcOfCircle [constr] CenterX=1.23825 CenterY=26.8446 CenterZ=0 NormalX=0 NormalY=0 NormalZ=1 AngleXU=0 Radius=1 StartAngle=0.25268 EndAngle=2.88891
    g7: LineSegment [constr] StartX=0.27 StartY=27.0946 StartZ=0 EndX=0 EndY=27.0946 EndZ=0
    g8: LineSegment [constr] StartX=2.20649 StartY=26.5946 StartZ=0 EndX=2.47649 EndY=26.5946 EndZ=0
    g9: LineSegment [constr] StartX=2.47649 StartY=26.8446 StartZ=0 EndX=-2.47649 EndY=26.8446 EndZ=0
    g10: ArcOfCircle CenterX=-1.23825 CenterY=26.8446 CenterZ=0 NormalX=0 NormalY=0 NormalZ=1 AngleXU=0 Radius=1 StartAngle=3.39427 EndAngle=6.03051
    g11: LineSegment [constr] StartX=0 StartY=26.5946 StartZ=0 EndX=0 EndY=27.0946 EndZ=0
    g12: LineSegment StartX=0 StartY=27.0946 StartZ=0 EndX=-0.27 EndY=27.0946 EndZ=0
    g13: LineSegment StartX=-2.47649 StartY=27.0946 StartZ=0 EndX=-2.47649 EndY=26.5946 EndZ=0
    g14: LineSegment StartX=-2.47649 StartY=26.5946 StartZ=0 EndX=-2.20649 EndY=26.5946 EndZ=0
    g15: GeomPoint [constr] X=-1.23825 Y=26.8446 Z=0
    g16: LineSegment StartX=-2.20649 StartY=27.0946 StartZ=0 EndX=-2.47649 EndY=27.0946 EndZ=0
    g17: ArcOfCircle CenterX=-1.23825 CenterY=26.8446 CenterZ=0 NormalX=0 NormalY=0 NormalZ=1 AngleXU=0 Radius=1 StartAngle=0.25268 EndAngle=2.88891
    g18: LineSegment StartX=-0.27 StartY=26.5946 StartZ=0 EndX=0 EndY=26.5946 EndZ=0
  constraints (51):
    c: Coincident(g1,g2)
    c: Coincident(g7,g3)
    c: Coincident(g3,g4)
    c: Coincident(g8,g1)
    c: Horizontal(g2)
    c: Horizontal(g4)
    c: Vertical(g1)
    c: Vertical(g3)
    c: Symmetric(g7,g1,g5)
    c: Coincident(g5,g0)
    c: Diameter(g0) = 2
    c: DistanceY(g3,g3) = 0.5
    c: Equal(g0,g6)
    c: Coincident(g0,g6)
    c: Coincident(g2,g6)
    c: Coincident(g7,g6)
    c: Coincident(g4,g0)
    c: Coincident(g8,g0)
    c: Horizontal(g7)
    c: Horizontal(g8)
    c: Equal(g7,g2)
    c: DistanceX(g7,g7) = 0.27
    c: Equal(g3,g1)
    c: Symmetric(g1,g1,g9)
    c: Coincident(g11,g12)
    c: Coincident(g16,g13)
    c: Coincident(g13,g14)
    c: Coincident(g18,g11)
    c: Horizontal(g12)
    c: Horizontal(g14)
    c: Vertical(g11)
    c: Vertical(g13)
    c: Symmetric(g16,g11,g15)
    c: Coincident(g15,g10)
    c: Coincident(g16,g17)
    c: Equal(g10,g17)
    c: Coincident(g17,g12)
    c: Coincident(g10,g17)
    c: Coincident(g14,g10)
    c: Coincident(g18,g10)
    c: Horizontal(g16)
    c: Horizontal(g18)
    c: Equal(g12,g16)
    c: Equal(g13,g11)
    c: Equal(g17,g6)
    c: Equal(g12,g7)
    c: Equal(g11,g3)
    c: PointOnObject(g7,g-2)
    c: Coincident(g12,g7)
    c: PointOnObject(g9,g13)
    c: Symmetric(g-3,g-3,g9)
FEATURE [PartDesign::AdditivePipe] AdditivePipe005
  AuxilleryCurvelinear = true
  AuxillerySpineTangent = false
  Binormal = (0,0,0)
  Mode = 0
  Placement = pos=(0,2.34e-14,-19.2055) rot=(0,0,1;0rad)
  Profile = -> Sketch013
  Refine = true
  Spine = -> Sketch009
  SpineTangent = false
  Suppressed = false
  Transformation = 0
  Transition = 0
FEATURE [PartDesign::AdditivePipe] AdditivePipe006
  AuxilleryCurvelinear = true
  AuxillerySpineTangent = false
  BaseFeature = -> AdditivePipe005
  Binormal = (0,0,0)
  Mode = 0
  Placement = pos=(0,2.34e-14,-19.2055) rot=(0,0,1;0rad)
  Profile = -> AdditivePipe005 [Face11]
  Refine = true
  Spine = -> Sketch010
  SpineTangent = false
  Suppressed = false
  Transformation = 0
  Transition = 0
FEATURE [PartDesign::AdditivePipe] AdditivePipe007
  AuxilleryCurvelinear = true
  AuxillerySpineTangent = false
  BaseFeature = -> AdditivePipe006
  Binormal = (0,0,0)
  Mode = 0
  Placement = pos=(0,2.34e-14,-19.2055) rot=(0,0,1;0rad)
  Profile = -> AdditivePipe006 [Face26]
  Refine = true
  Spine = -> Sketch011
  SpineTangent = false
  Suppressed = false
  Transformation = 0
  Transition = 0
FEATURE [PartDesign::AdditivePipe] Pipe
  AuxilleryCurvelinear = true
  AuxillerySpineTangent = false
  BaseFeature = -> AdditivePipe007
  Binormal = (0,0,0)
  Mode = 0
  Profile = -> AdditivePipe007 [Face42]
  Refine = true
  Spine = -> Sketch012 [Edge1,Edge2,Edge3]
  SpineTangent = false
  Suppressed = false
  Transformation = 0
  Transition = 1
FEATURE [PartDesign::Body] Body011  label="Bat-"
  AllowCompound = false
  Group = -> [Sketch008,DatumPlane005,Sketch009,DatumPlane006,Sketch010,DatumPlane007,Sketch011,DatumPlane008,Sketch012,Sketch013,AdditivePipe005,AdditivePipe006,AdditivePipe007,Binder061,Binder062,Pipe]
  Origin = -> Origin054
  Tip = -> Pipe
FEATURE [App::DocumentObjectGroup] Group004  label="Cables"
  Group = -> [Part__Feature956,Part__Feature957,Group003,Solid,Body010,Body011]
FEATURE [Part::Part2DObjectPython] Shape2DView  # Draft 2D object (typed FeaturePython)
  AutoUpdate = true
  Base = -> Group
  Clip = false
  FuseArch = false
  HiddenLines = false
  InPlace = true
  OnlySolids = false
  Projection = (0.632255,-0.610857,0.476557)
  ProjectionMode = 0
  SegmentLength = 0.05
  Tessellation = false
  VisibleOnly = false
FEATURE [Part::Part2DObjectPython] Shape2DView001  # Draft 2D object (typed FeaturePython)
  AutoUpdate = true
  Base = -> User_Library_9V_Duracell_Battery
  Clip = false
  FuseArch = false
  HiddenLines = false
  InPlace = true
  OnlySolids = false
  Projection = (0.632255,-0.610857,0.476557)
  ProjectionMode = 0
  SegmentLength = 0.05
  Tessellation = false
  VisibleOnly = false
FEATURE [Part::Part2DObjectPython] Shape2DView002  # Draft 2D object (typed FeaturePython)
  AutoUpdate = true
  Base = -> _68005_cp005_cp
  Clip = false
  FuseArch = false
  HiddenLines = false
  InPlace = true
  OnlySolids = false
  Projection = (0.632255,-0.610857,0.476557)
  ProjectionMode = 0
  SegmentLength = 0.05
  Tessellation = false
  VisibleOnly = false
FEATURE [Part::Part2DObjectPython] Shape2DView003  # Draft 2D object (typed FeaturePython)
  AutoUpdate = true
  Base = -> TheThing_main_1
  Clip = false
  FuseArch = false
  HiddenLines = false
  InPlace = true
  OnlySolids = false
  Projection = (0.632255,-0.610857,0.476557)
  ProjectionMode = 0
  SegmentLength = 0.05
  Tessellation = false
  VisibleOnly = false
FEATURE [Part::Part2DObjectPython] Shape2DView004  # Draft 2D object (typed FeaturePython)
  AutoUpdate = true
  Base = -> TheThing_addon_1
  Clip = false
  FuseArch = false
  HiddenLines = false
  InPlace = true
  OnlySolids = false
  Projection = (0.632255,-0.610857,0.476557)
  ProjectionMode = 0
  SegmentLength = 0.05
  Tessellation = false
  VisibleOnly = false
FEATURE [Part::Part2DObjectPython] Shape2DView005  # Draft 2D object (typed FeaturePython)
  AutoUpdate = true
  Base = -> Part__Feature001
  Clip = false
  FuseArch = false
  HiddenLines = false
  InPlace = true
  OnlySolids = false
  Projection = (0.632255,-0.610857,0.476557)
  ProjectionMode = 0
  SegmentLength = 0.05
  Tessellation = false
  VisibleOnly = false
FEATURE [Part::Part2DObjectPython] Shape2DView006  # Draft 2D object (typed FeaturePython)
  AutoUpdate = true
  Base = -> Part__Feature002
  Clip = false
  FuseArch = false
  HiddenLines = false
  InPlace = true
  OnlySolids = false
  Projection = (0.632255,-0.610857,0.476557)
  ProjectionMode = 0
  SegmentLength = 0.05
  Tessellation = false
  VisibleOnly = false
FEATURE [Part::Part2DObjectPython] Shape2DView007  # Draft 2D object (typed FeaturePython)
  AutoUpdate = true
  Base = -> Body021
  Clip = false
  FuseArch = false
  HiddenLines = false
  InPlace = true
  OnlySolids = false
  Projection = (0.632255,-0.610857,0.476557)
  ProjectionMode = 0
  SegmentLength = 0.05
  Tessellation = false
  VisibleOnly = false
FEATURE [Part::Part2DObjectPython] Shape2DView008  # Draft 2D object (typed FeaturePython)
  AutoUpdate = true
  Base = -> Part__Feature956
  Clip = false
  FuseArch = false
  HiddenLines = false
  InPlace = true
  OnlySolids = false
  Projection = (0.632255,-0.610857,0.476557)
  ProjectionMode = 0
  SegmentLength = 0.05
  Tessellation = false
  VisibleOnly = false
FEATURE [Part::Part2DObjectPython] Shape2DView009  # Draft 2D object (typed FeaturePython)
  AutoUpdate = true
  Base = -> Part__Feature957
  Clip = false
  FuseArch = false
  HiddenLines = false
  InPlace = true
  OnlySolids = false
  Projection = (0.632255,-0.610857,0.476557)
  ProjectionMode = 0
  SegmentLength = 0.05
  Tessellation = false
  VisibleOnly = false
FEATURE [Part::Part2DObjectPython] Shape2DView010  # Draft 2D object (typed FeaturePython)
  AutoUpdate = true
  Base = -> Group003
  Clip = false
  FuseArch = false
  HiddenLines = false
  InPlace = true
  OnlySolids = false
  Projection = (0.632255,-0.610857,0.476557)
  ProjectionMode = 0
  SegmentLength = 0.05
  Tessellation = false
  VisibleOnly = false
FEATURE [Part::Part2DObjectPython] Shape2DView011  # Draft 2D object (typed FeaturePython)
  AutoUpdate = true
  Base = -> Solid
  Clip = false
  FuseArch = false
  HiddenLines = false
  InPlace = true
  OnlySolids = false
  Projection = (0.632255,-0.610857,0.476557)
  ProjectionMode = 0
  SegmentLength = 0.05
  Tessellation = false
  VisibleOnly = false
FEATURE [Part::Part2DObjectPython] Shape2DView012  # Draft 2D object (typed FeaturePython)
  AutoUpdate = true
  Base = -> Body010
  Clip = false
  FuseArch = false
  HiddenLines = false
  InPlace = true
  OnlySolids = false
  Projection = (0.632255,-0.610857,0.476557)
  ProjectionMode = 0
  SegmentLength = 0.05
  Tessellation = false
  VisibleOnly = false
FEATURE [Part::Part2DObjectPython] Shape2DView013  # Draft 2D object (typed FeaturePython)
  AutoUpdate = true
  Base = -> Body011
  Clip = false
  FuseArch = false
  HiddenLines = false
  InPlace = true
  OnlySolids = false
  Projection = (0.632255,-0.610857,0.476557)
  ProjectionMode = 0
  SegmentLength = 0.05
  Tessellation = false
  VisibleOnly = false
FEATURE [Sketcher::SketchObject] Sketch064
  ArcFitTolerance = 1e-06
  FullyConstrained = false
  MakeInternals = false
  sketch-geometry (825):
    g0: LineSegment StartX=9.93947 StartY=32.6286 StartZ=0 EndX=20.5389 EndY=37.5089 EndZ=0
    g1: LineSegment StartX=9.77387 StartY=32.7103 StartZ=0 EndX=9.93947 EndY=32.6286 EndZ=0
    g2: ArcOfEllipse CenterX=16.4744 CenterY=-5.9685 CenterZ=0 NormalX=0 NormalY=0 NormalZ=1 MajorRadius=4.5 MinorRadius=2.84515 AngleXU=-2.02903 StartAngle=1.88425 EndAngle=2.75513
    g3: LineSegment StartX=19.5155 StartY=-5.92137 StartZ=0 EndX=17.9167 EndY=-12.0273 EndZ=0
    g4: ArcOfEllipse CenterX=14.8756 CenterY=-12.0744 CenterZ=0 NormalX=0 NormalY=0 NormalZ=1 MajorRadius=4.5 MinorRadius=2.84515 AngleXU=-2.02903 StartAngle=0.313451 EndAngle=1.88425
    g5: LineSegment StartX=13.7687 StartY=-16.3016 StartZ=0 EndX=12.326 EndY=-16.324 EndZ=0
    g6: ArcOfEllipse CenterX=22.7382 CenterY=-6.79202 CenterZ=0 NormalX=0 NormalY=0 NormalZ=1 MajorRadius=2.5 MinorRadius=1.58064 AngleXU=-2.02903 StartAngle=1.88425 EndAngle=2.38531
    g7: LineSegment StartX=24.4277 StartY=-6.76584 StartZ=0 EndX=23.4192 EndY=-10.6173 EndZ=0
    g8: ArcOfEllipse CenterX=21.7297 CenterY=-10.6435 CenterZ=0 NormalX=0 NormalY=0 NormalZ=1 MajorRadius=2.5 MinorRadius=1.58064 AngleXU=-2.02903 StartAngle=0.756279 EndAngle=1.88425
    g9: ArcOfEllipse CenterX=20.6731 CenterY=37.5707 CenterZ=0 NormalX=0 NormalY=0 NormalZ=1 MajorRadius=0.186667 MinorRadius=0.118021 AngleXU=-2.02903 StartAngle=5.37491 EndAngle=6.28319
    g10: ArcOfEllipse CenterX=20.6731 CenterY=37.5707 CenterZ=0 NormalX=0 NormalY=0 NormalZ=1 MajorRadius=0.186667 MinorRadius=0.118021 AngleXU=-2.02903 StartAngle=0 EndAngle=2.23331
    g11: ArcOfEllipse CenterX=20.6731 CenterY=37.5707 CenterZ=0 NormalX=0 NormalY=0 NormalZ=1 MajorRadius=0.186667 MinorRadius=0.118021 AngleXU=-2.02903 StartAngle=2.23331 EndAngle=3.14159
    g12: ArcOfEllipse CenterX=20.6731 CenterY=37.5707 CenterZ=0 NormalX=0 NormalY=0 NormalZ=1 MajorRadius=0.186667 MinorRadius=0.118021 AngleXU=-2.02903 StartAngle=3.14159 EndAngle=3.80411
    g13: LineSegment StartX=20.8074 StartY=37.6325 StartZ=0 EndX=27.8385 EndY=40.8698 EndZ=0
    g14: ArcOfEllipse CenterX=27.9727 CenterY=40.9316 CenterZ=0 NormalX=0 NormalY=0 NormalZ=1 MajorRadius=0.186667 MinorRadius=0.118021 AngleXU=-2.02903 StartAngle=5.37491 EndAngle=6.28319
    g15: ArcOfEllipse CenterX=27.9727 CenterY=40.9316 CenterZ=0 NormalX=0 NormalY=0 NormalZ=1 MajorRadius=0.186667 MinorRadius=0.118021 AngleXU=-2.02903 StartAngle=0 EndAngle=2.23331
    g16: LineSegment StartX=28.1069 StartY=40.9934 StartZ=0 EndX=38.7063 EndY=45.8737 EndZ=0
    g17: LineSegment StartX=38.7063 StartY=45.8737 StartZ=0 EndX=38.7063 EndY=29.6198 EndZ=0
    g18: ArcOfEllipse CenterX=38.7063 CenterY=29.4557 CenterZ=0 NormalX=0 NormalY=0 NormalZ=1 MajorRadius=0.186667 MinorRadius=0.118021 AngleXU=-2.02903 StartAngle=3.80411 EndAngle=6.28319
    g19: ArcOfEllipse CenterX=38.7063 CenterY=29.4557 CenterZ=0 NormalX=0 NormalY=0 NormalZ=1 MajorRadius=0.186667 MinorRadius=0.118021 AngleXU=-2.02903 StartAngle=0 EndAngle=0.662517
    g20: LineSegment StartX=38.7063 StartY=29.2916 StartZ=0 EndX=38.7063 EndY=20.6965 EndZ=0
    g21: ArcOfEllipse CenterX=38.7063 CenterY=20.5324 CenterZ=0 NormalX=0 NormalY=0 NormalZ=1 MajorRadius=0.186667 MinorRadius=0.118021 AngleXU=-2.02903 StartAngle=3.80411 EndAngle=6.28319
    g22: ArcOfEllipse CenterX=38.7063 CenterY=20.5324 CenterZ=0 NormalX=0 NormalY=0 NormalZ=1 MajorRadius=0.186667 MinorRadius=0.118021 AngleXU=-2.02903 StartAngle=0 EndAngle=0.662517
    g23: LineSegment StartX=38.7063 StartY=20.3683 StartZ=0 EndX=38.7063 EndY=-12.1395 EndZ=0
    g24: ArcOfEllipse CenterX=38.7063 CenterY=-12.3036 CenterZ=0 NormalX=0 NormalY=0 NormalZ=1 MajorRadius=0.186667 MinorRadius=0.118021 AngleXU=-2.02903 StartAngle=3.80411 EndAngle=6.28319
    g25: ArcOfEllipse CenterX=38.7063 CenterY=-12.3036 CenterZ=0 NormalX=0 NormalY=0 NormalZ=1 MajorRadius=0.186667 MinorRadius=0.118021 AngleXU=-2.02903 StartAngle=0 EndAngle=0.662517
    g26: LineSegment StartX=38.7063 StartY=-12.4677 StartZ=0 EndX=38.7063 EndY=-21.0628 EndZ=0
    g27: ArcOfEllipse CenterX=38.7063 CenterY=-21.2269 CenterZ=0 NormalX=0 NormalY=0 NormalZ=1 MajorRadius=0.186667 MinorRadius=0.118021 AngleXU=-2.02903 StartAngle=3.80411 EndAngle=6.28319
    g28: ArcOfEllipse CenterX=38.7063 CenterY=-21.2269 CenterZ=0 NormalX=0 NormalY=0 NormalZ=1 MajorRadius=0.186667 MinorRadius=0.118021 AngleXU=-2.02903 StartAngle=0 EndAngle=0.662517
    g29: LineSegment StartX=38.7063 StartY=-21.391 StartZ=0 EndX=38.7063 EndY=-37.6449 EndZ=0
    g30: LineSegment StartX=38.7063 StartY=-37.6449 StartZ=0 EndX=29.0059 EndY=-42.1113 EndZ=0
    g31: ArcOfEllipse CenterX=28.8717 CenterY=-42.1731 CenterZ=0 NormalX=0 NormalY=0 NormalZ=1 MajorRadius=0.186667 MinorRadius=0.118021 AngleXU=-2.02903 StartAngle=2.23331 EndAngle=3.14159
    g32: ArcOfEllipse CenterX=28.8717 CenterY=-42.1731 CenterZ=0 NormalX=0 NormalY=0 NormalZ=1 MajorRadius=0.186667 MinorRadius=0.118021 AngleXU=-2.02903 StartAngle=3.14159 EndAngle=5.37491
    g33: LineSegment StartX=28.7374 StartY=-42.2349 StartZ=0 EndX=21.7063 EndY=-45.4722 EndZ=0
    g34: ArcOfEllipse CenterX=21.5721 CenterY=-45.534 CenterZ=0 NormalX=0 NormalY=0 NormalZ=1 MajorRadius=0.186667 MinorRadius=0.118021 AngleXU=-2.02903 StartAngle=2.23331 EndAngle=3.14159
    g35: ArcOfEllipse CenterX=21.5721 CenterY=-45.534 CenterZ=0 NormalX=0 NormalY=0 NormalZ=1 MajorRadius=0.186667 MinorRadius=0.118021 AngleXU=-2.02903 StartAngle=3.14159 EndAngle=5.37491
    g36: LineSegment StartX=21.4378 StartY=-45.5958 StartZ=0 EndX=2.03697 EndY=-54.5286 EndZ=0
    g37: ArcOfEllipse CenterX=1.90272 CenterY=-54.5904 CenterZ=0 NormalX=0 NormalY=0 NormalZ=1 MajorRadius=0.186667 MinorRadius=0.118021 AngleXU=-2.02903 StartAngle=2.23331 EndAngle=3.14159
    g38: ArcOfEllipse CenterX=1.90272 CenterY=-54.5904 CenterZ=0 NormalX=0 NormalY=0 NormalZ=1 MajorRadius=0.186667 MinorRadius=0.118021 AngleXU=-2.02903 StartAngle=3.14159 EndAngle=5.37491
    g39: LineSegment StartX=1.76848 StartY=-54.6522 StartZ=0 EndX=-5.26262 EndY=-57.8895 EndZ=0
    g40: ArcOfEllipse CenterX=-5.39687 CenterY=-57.9513 CenterZ=0 NormalX=0 NormalY=0 NormalZ=1 MajorRadius=0.186667 MinorRadius=0.118021 AngleXU=-2.02903 StartAngle=2.23331 EndAngle=3.14159
    g41: ArcOfEllipse CenterX=-5.39687 CenterY=-57.9513 CenterZ=0 NormalX=0 NormalY=0 NormalZ=1 MajorRadius=0.186667 MinorRadius=0.118021 AngleXU=-2.02903 StartAngle=3.14159 EndAngle=5.37491
    g42: LineSegment StartX=-5.53111 StartY=-58.0131 StartZ=0 EndX=-15.2315 EndY=-62.4795 EndZ=0
    g43: LineSegment StartX=-15.2315 StartY=-62.4795 StartZ=0 EndX=-15.2315 EndY=-51.7202 EndZ=0
    g44: ArcOfEllipse CenterX=-15.2315 CenterY=-51.5561 CenterZ=0 NormalX=0 NormalY=0 NormalZ=1 MajorRadius=0.186667 MinorRadius=0.118021 AngleXU=-2.02903 StartAngle=0.662517 EndAngle=3.14159
    g45: ArcOfEllipse CenterX=-15.2315 CenterY=-51.5561 CenterZ=0 NormalX=0 NormalY=0 NormalZ=1 MajorRadius=0.186667 MinorRadius=0.118021 AngleXU=-2.02903 StartAngle=3.14159 EndAngle=3.80411
    g46: LineSegment StartX=-15.2315 StartY=-51.392 StartZ=0 EndX=-15.2315 EndY=-42.7969 EndZ=0
    g47: ArcOfEllipse CenterX=-15.2315 CenterY=-42.6328 CenterZ=0 NormalX=0 NormalY=0 NormalZ=1 MajorRadius=0.186667 MinorRadius=0.118021 AngleXU=-2.02903 StartAngle=0.662517 EndAngle=3.14159
    g48: ArcOfEllipse CenterX=-15.2315 CenterY=-42.6328 CenterZ=0 NormalX=0 NormalY=0 NormalZ=1 MajorRadius=0.186667 MinorRadius=0.118021 AngleXU=-2.02903 StartAngle=3.14159 EndAngle=3.80411
    g49: LineSegment StartX=-15.2315 StartY=-42.4687 StartZ=0 EndX=-15.2315 EndY=-31.7095 EndZ=0
    g50: LineSegment StartX=-15.2315 StartY=-31.7095 StartZ=0 EndX=-8.04108 EndY=-28.3988 EndZ=0
    g51: ArcOfEllipse CenterX=-7.90684 CenterY=-28.337 CenterZ=0 NormalX=0 NormalY=0 NormalZ=1 MajorRadius=0.186667 MinorRadius=0.118021 AngleXU=-2.02903 StartAngle=5.37491 EndAngle=6.28319
    g52: ArcOfEllipse CenterX=-7.90684 CenterY=-28.337 CenterZ=0 NormalX=0 NormalY=0 NormalZ=1 MajorRadius=0.186667 MinorRadius=0.118021 AngleXU=-2.02903 StartAngle=0 EndAngle=2.23331
    g53: LineSegment StartX=-7.77259 StartY=-28.2751 StartZ=0 EndX=-0.741492 EndY=-25.0378 EndZ=0
    g54: ArcOfEllipse CenterX=-0.607246 CenterY=-24.976 CenterZ=0 NormalX=0 NormalY=0 NormalZ=1 MajorRadius=0.186667 MinorRadius=0.118021 AngleXU=-2.02903 StartAngle=5.37491 EndAngle=6.28319
    g55: ArcOfEllipse CenterX=-0.607246 CenterY=-24.976 CenterZ=0 NormalX=0 NormalY=0 NormalZ=1 MajorRadius=0.186667 MinorRadius=0.118021 AngleXU=-2.02903 StartAngle=0 EndAngle=2.23331
    g56: LineSegment StartX=-0.473001 StartY=-24.9142 StartZ=0 EndX=6.71746 EndY=-21.6035 EndZ=0
    g57: LineSegment StartX=6.71746 StartY=-21.6035 StartZ=0 EndX=12.428 EndY=0.205474 EndZ=0
    g58: ArcOfEllipse CenterX=12.4739 CenterY=0.380825 CenterZ=0 NormalX=0 NormalY=0 NormalZ=1 MajorRadius=0.186667 MinorRadius=0.118021 AngleXU=-2.02903 StartAngle=0.313451 EndAngle=3.14159
    g59: ArcOfEllipse CenterX=12.4739 CenterY=0.380825 CenterZ=0 NormalX=0 NormalY=0 NormalZ=1 MajorRadius=0.186667 MinorRadius=0.118021 AngleXU=-2.02903 StartAngle=3.14159 EndAngle=3.45504
    g60: LineSegment StartX=12.5199 StartY=0.556175 StartZ=0 EndX=14.9246 EndY=9.74015 EndZ=0
    g61: ArcOfEllipse CenterX=14.9706 CenterY=9.9155 CenterZ=0 NormalX=0 NormalY=0 NormalZ=1 MajorRadius=0.186667 MinorRadius=0.118021 AngleXU=-2.02903 StartAngle=0.313451 EndAngle=3.14159
    g62: ArcOfEllipse CenterX=14.9706 CenterY=9.9155 CenterZ=0 NormalX=0 NormalY=0 NormalZ=1 MajorRadius=0.186667 MinorRadius=0.118021 AngleXU=-2.02903 StartAngle=3.14159 EndAngle=3.45504
    g63: LineSegment StartX=15.0165 StartY=10.0908 StartZ=0 EndX=20.727 EndY=31.8998 EndZ=0
    g64: LineSegment StartX=20.727 StartY=31.8998 StartZ=0 EndX=9.93947 EndY=31.7327 EndZ=0
    g65: LineSegment StartX=9.93947 StartY=31.7327 StartZ=0 EndX=9.93947 EndY=32.6286 EndZ=0
    g66: LineSegment StartX=-9.69392 StartY=-33.4588 StartZ=0 EndX=-9.69392 EndY=-34.7863 EndZ=0
    g67: LineSegment StartX=-9.69392 StartY=-33.4588 StartZ=0 EndX=-1.06386 EndY=-29.4853 EndZ=0
    g68: LineSegment StartX=-9.69392 StartY=-34.7863 StartZ=0 EndX=-1.06386 EndY=-30.8128 EndZ=0
    g69: LineSegment StartX=-1.06386 StartY=-29.4853 StartZ=0 EndX=-1.06386 EndY=-30.8128 EndZ=0
    g70: LineSegment StartX=27.0995 StartY=-8.50945 StartZ=0 EndX=28.12 EndY=-8.49363 EndZ=0
    g71: LineSegment StartX=27.0995 StartY=-8.50945 StartZ=0 EndX=24.1479 EndY=-19.782 EndZ=0
    g72: LineSegment StartX=28.12 StartY=-8.49363 StartZ=0 EndX=25.1683 EndY=-19.7662 EndZ=0
    g73: LineSegment StartX=24.1479 StartY=-19.782 StartZ=0 EndX=25.1683 EndY=-19.7662 EndZ=0
    g74: LineSegment StartX=17.8373 StartY=-2.72712 StartZ=0 EndX=19.5268 EndY=-2.70094 EndZ=0
    g75: ArcOfEllipse CenterX=16.7304 CenterY=-6.95432 CenterZ=0 NormalX=0 NormalY=0 NormalZ=1 MajorRadius=4.5 MinorRadius=2.84515 AngleXU=-2.02903 StartAngle=3.45504 EndAngle=5.02584
    g76: ArcOfEllipse CenterX=18.4199 CenterY=-6.92813 CenterZ=0 NormalX=0 NormalY=0 NormalZ=1 MajorRadius=4.5 MinorRadius=2.84515 AngleXU=-2.02903 StartAngle=1.88425 EndAngle=3.14159
    g77: ArcOfEllipse CenterX=18.4199 CenterY=-6.92813 CenterZ=0 NormalX=0 NormalY=0 NormalZ=1 MajorRadius=4.5 MinorRadius=2.84515 AngleXU=-2.02903 StartAngle=3.14159 EndAngle=3.45504
    g78: LineSegment StartX=12.0905 StartY=-13.1074 StartZ=0 EndX=13.6893 EndY=-7.00145 EndZ=0
    g79: LineSegment StartX=21.461 StartY=-6.881 StartZ=0 EndX=19.8622 EndY=-12.987 EndZ=0
    g80: ArcOfEllipse CenterX=15.1316 CenterY=-13.0603 CenterZ=0 NormalX=0 NormalY=0 NormalZ=1 MajorRadius=4.5 MinorRadius=2.84515 AngleXU=-2.02903 StartAngle=5.02584 EndAngle=6.28319
    g81: ArcOfEllipse CenterX=15.1316 CenterY=-13.0603 CenterZ=0 NormalX=0 NormalY=0 NormalZ=1 MajorRadius=4.5 MinorRadius=2.84515 AngleXU=-2.02903 StartAngle=0 EndAngle=0.313451
    g82: ArcOfEllipse CenterX=16.8211 CenterY=-13.0341 CenterZ=0 NormalX=0 NormalY=0 NormalZ=1 MajorRadius=4.5 MinorRadius=2.84515 AngleXU=-2.02903 StartAngle=0.313451 EndAngle=1.88425
    g83: LineSegment StartX=15.7142 StartY=-17.2613 StartZ=0 EndX=14.0247 EndY=-17.2875 EndZ=0
    g84: ArcOfEllipse CenterX=24.6837 CenterY=-7.75166 CenterZ=0 NormalX=0 NormalY=0 NormalZ=1 MajorRadius=2.5 MinorRadius=1.58064 AngleXU=-2.02903 StartAngle=1.88425 EndAngle=3.14159
    g85: ArcOfEllipse CenterX=24.6837 CenterY=-7.75166 CenterZ=0 NormalX=0 NormalY=0 NormalZ=1 MajorRadius=2.5 MinorRadius=1.58064 AngleXU=-2.02903 StartAngle=3.14159 EndAngle=5.02584
    g86: LineSegment StartX=26.3732 StartY=-7.72547 StartZ=0 EndX=25.3647 EndY=-11.5769 EndZ=0
    g87: LineSegment StartX=22.9942 StartY=-7.77784 StartZ=0 EndX=21.9857 EndY=-11.6293 EndZ=0
    g88: ArcOfEllipse CenterX=23.6752 CenterY=-11.6031 CenterZ=0 NormalX=0 NormalY=0 NormalZ=1 MajorRadius=2.5 MinorRadius=1.58064 AngleXU=-2.02903 StartAngle=5.02584 EndAngle=6.28319
    g89: ArcOfEllipse CenterX=23.6752 CenterY=-11.6031 CenterZ=0 NormalX=0 NormalY=0 NormalZ=1 MajorRadius=2.5 MinorRadius=1.58064 AngleXU=-2.02903 StartAngle=0 EndAngle=1.88425
    g90: LineSegment StartX=34.9706 StartY=21.5506 StartZ=0 EndX=35.9911 EndY=21.5664 EndZ=0
    g91: LineSegment StartX=34.9706 StartY=21.5506 StartZ=0 EndX=32.0189 EndY=10.2781 EndZ=0
    g92: LineSegment StartX=35.9911 StartY=21.5664 StartZ=0 EndX=33.0394 EndY=10.2939 EndZ=0
    g93: LineSegment StartX=32.0189 StartY=10.2781 StartZ=0 EndX=33.0394 EndY=10.2939 EndZ=0
    g94: LineSegment StartX=9 StartY=32.196 StartZ=0 EndX=9.93947 EndY=31.7327 EndZ=0
    g95: ArcOfEllipse CenterX=27.9727 CenterY=40.9316 CenterZ=0 NormalX=0 NormalY=0 NormalZ=1 MajorRadius=0.186667 MinorRadius=0.118021 AngleXU=-2.02903 StartAngle=3.80411 EndAngle=5.37491
    g96: ArcOfEllipse CenterX=38.7063 CenterY=29.4557 CenterZ=0 NormalX=0 NormalY=0 NormalZ=1 MajorRadius=0.186667 MinorRadius=0.118021 AngleXU=-2.02903 StartAngle=0.662517 EndAngle=2.23331
    g97: ArcOfEllipse CenterX=38.7063 CenterY=20.5324 CenterZ=0 NormalX=0 NormalY=0 NormalZ=1 MajorRadius=0.186667 MinorRadius=0.118021 AngleXU=-2.02903 StartAngle=2.23331 EndAngle=3.14159
    g98: ArcOfEllipse CenterX=38.7063 CenterY=20.5324 CenterZ=0 NormalX=0 NormalY=0 NormalZ=1 MajorRadius=0.186667 MinorRadius=0.118021 AngleXU=-2.02903 StartAngle=3.14159 EndAngle=3.80411
    g99: LineSegment StartX=38.5761 StartY=20.4325 StartZ=0 EndX=38.7063 EndY=20.3683 EndZ=0
    g100: ArcOfEllipse CenterX=38.7063 CenterY=-12.3036 CenterZ=0 NormalX=0 NormalY=0 NormalZ=1 MajorRadius=0.186667 MinorRadius=0.118021 AngleXU=-2.02903 StartAngle=0.662517 EndAngle=2.23331
    g101: ArcOfEllipse CenterX=38.7063 CenterY=-21.2269 CenterZ=0 NormalX=0 NormalY=0 NormalZ=1 MajorRadius=0.186667 MinorRadius=0.118021 AngleXU=-2.02903 StartAngle=2.23331 EndAngle=3.14159
    g102: ArcOfEllipse CenterX=38.7063 CenterY=-21.2269 CenterZ=0 NormalX=0 NormalY=0 NormalZ=1 MajorRadius=0.186667 MinorRadius=0.118021 AngleXU=-2.02903 StartAngle=3.14159 EndAngle=3.80411
    g103: LineSegment StartX=38.5761 StartY=-21.3268 StartZ=0 EndX=38.7063 EndY=-21.391 EndZ=0
    g104: LineSegment StartX=28.839 StartY=-42.029 StartZ=0 EndX=29.0059 EndY=-42.1113 EndZ=0
    g105: ArcOfEllipse CenterX=28.8717 CenterY=-42.1731 CenterZ=0 NormalX=0 NormalY=0 NormalZ=1 MajorRadius=0.186667 MinorRadius=0.118021 AngleXU=-2.02903 StartAngle=5.37491 EndAngle=6.28319
    g106: ArcOfEllipse CenterX=28.8717 CenterY=-42.1731 CenterZ=0 NormalX=0 NormalY=0 NormalZ=1 MajorRadius=0.186667 MinorRadius=0.118021 AngleXU=-2.02903 StartAngle=9e-16 EndAngle=0.662517
    g107: ArcOfEllipse CenterX=21.5721 CenterY=-45.534 CenterZ=0 NormalX=0 NormalY=0 NormalZ=1 MajorRadius=0.186667 MinorRadius=0.118021 AngleXU=-2.02903 StartAngle=0.662517 EndAngle=2.23331
    g108: LineSegment StartX=1.87006 StartY=-54.4462 StartZ=0 EndX=2.03697 EndY=-54.5286 EndZ=0
    g109: ArcOfEllipse CenterX=1.90272 CenterY=-54.5904 CenterZ=0 NormalX=0 NormalY=0 NormalZ=1 MajorRadius=0.186667 MinorRadius=0.118021 AngleXU=-2.02903 StartAngle=5.37491 EndAngle=6.28319
    g110: ArcOfEllipse CenterX=1.90272 CenterY=-54.5904 CenterZ=0 NormalX=0 NormalY=0 NormalZ=1 MajorRadius=0.186667 MinorRadius=0.118021 AngleXU=-2.02903 StartAngle=9e-16 EndAngle=0.662517
    g111: ArcOfEllipse CenterX=-5.39687 CenterY=-57.9513 CenterZ=0 NormalX=0 NormalY=0 NormalZ=1 MajorRadius=0.186667 MinorRadius=0.118021 AngleXU=-2.02903 StartAngle=0.662517 EndAngle=2.23331
    g112: LineSegment StartX=-16.1539 StartY=-62.0245 StartZ=0 EndX=-15.2315 EndY=-62.4795 EndZ=0
    g113: ArcOfEllipse CenterX=-15.2315 CenterY=-51.5561 CenterZ=0 NormalX=0 NormalY=0 NormalZ=1 MajorRadius=0.186667 MinorRadius=0.118021 AngleXU=-2.02903 StartAngle=3.80411 EndAngle=5.37491
    g114: ArcOfEllipse CenterX=-15.2315 CenterY=-42.6328 CenterZ=0 NormalX=0 NormalY=0 NormalZ=1 MajorRadius=0.186667 MinorRadius=0.118021 AngleXU=-2.02903 StartAngle=5.37491 EndAngle=6.28319
    g115: ArcOfEllipse CenterX=-15.2315 CenterY=-42.6328 CenterZ=0 NormalX=0 NormalY=0 NormalZ=1 MajorRadius=0.186667 MinorRadius=0.118021 AngleXU=-2.02903 StartAngle=0 EndAngle=0.662517
    g116: LineSegment StartX=-15.4165 StartY=-31.6183 StartZ=0 EndX=-15.2315 EndY=-31.7095 EndZ=0
    g117: ArcOfEllipse CenterX=-7.90684 CenterY=-28.337 CenterZ=0 NormalX=0 NormalY=0 NormalZ=1 MajorRadius=0.186667 MinorRadius=0.118021 AngleXU=-2.02903 StartAngle=2.23331 EndAngle=3.14159
    g118: ArcOfEllipse CenterX=-7.90684 CenterY=-28.337 CenterZ=0 NormalX=0 NormalY=0 NormalZ=1 MajorRadius=0.186667 MinorRadius=0.118021 AngleXU=-2.02903 StartAngle=3.14159 EndAngle=3.80411
    g119: ArcOfEllipse CenterX=-0.607246 CenterY=-24.976 CenterZ=0 NormalX=0 NormalY=0 NormalZ=1 MajorRadius=0.186667 MinorRadius=0.118021 AngleXU=-2.02903 StartAngle=3.80411 EndAngle=5.37491
    g120: LineSegment StartX=5.68657 StartY=-21.095 StartZ=0 EndX=6.71746 EndY=-21.6035 EndZ=0
    g121: ArcOfEllipse CenterX=12.4739 CenterY=0.380825 CenterZ=0 NormalX=0 NormalY=0 NormalZ=1 MajorRadius=0.186667 MinorRadius=0.118021 AngleXU=-2.02903 StartAngle=3.45504 EndAngle=5.02584
    g122: ArcOfEllipse CenterX=14.9706 CenterY=9.9155 CenterZ=0 NormalX=0 NormalY=0 NormalZ=1 MajorRadius=0.186667 MinorRadius=0.118021 AngleXU=-2.02903 StartAngle=5.02584 EndAngle=6.28319
    g123: ArcOfEllipse CenterX=14.9706 CenterY=9.9155 CenterZ=0 NormalX=0 NormalY=0 NormalZ=1 MajorRadius=0.186667 MinorRadius=0.118021 AngleXU=-2.02903 StartAngle=0 EndAngle=0.313451
    g124: LineSegment StartX=-2.45584 StartY=-30.1262 StartZ=0 EndX=-1.06386 EndY=-30.8128 EndZ=0
    g125: LineSegment StartX=24.2683 StartY=-19.3222 StartZ=0 EndX=25.1683 EndY=-19.7662 EndZ=0
    g126: LineSegment StartX=32.1393 StartY=10.7379 StartZ=0 EndX=33.0394 EndY=10.2939 EndZ=0
    g127: LineSegment StartX=18.7276 StartY=40.9919 StartZ=0 EndX=20.6731 EndY=40.0323 EndZ=0
    g128: LineSegment StartX=20.6731 StartY=37.7348 StartZ=0 EndX=20.6731 EndY=40.0323 EndZ=0
    g129: LineSegment StartX=27.9727 StartY=43.3932 StartZ=0 EndX=20.6731 EndY=40.0323 EndZ=0
    g130: LineSegment StartX=27.9727 StartY=41.0957 StartZ=0 EndX=27.9727 EndY=43.3932 EndZ=0
    g131: LineSegment StartX=38.8406 StartY=29.5175 StartZ=0 EndX=40.72 EndY=30.3829 EndZ=0
    g132: LineSegment StartX=40.72 StartY=21.4596 StartZ=0 EndX=40.72 EndY=30.3829 EndZ=0
    g133: LineSegment StartX=38.8406 StartY=20.5942 StartZ=0 EndX=40.72 EndY=21.4596 EndZ=0
    g134: LineSegment StartX=38.8406 StartY=-12.2418 StartZ=0 EndX=40.72 EndY=-11.3765 EndZ=0
    g135: LineSegment StartX=40.72 StartY=-20.2998 StartZ=0 EndX=40.72 EndY=-11.3765 EndZ=0
    g136: LineSegment StartX=38.8406 StartY=-21.1651 StartZ=0 EndX=40.72 EndY=-20.2998 EndZ=0
    g137: LineSegment StartX=28.8717 StartY=-42.3372 StartZ=0 EndX=28.8717 EndY=-44.6347 EndZ=0
    g138: LineSegment StartX=21.5721 StartY=-47.9956 StartZ=0 EndX=28.8717 EndY=-44.6347 EndZ=0
    g139: LineSegment StartX=21.5721 StartY=-45.6981 StartZ=0 EndX=21.5721 EndY=-47.9956 EndZ=0
    g140: LineSegment StartX=1.90272 StartY=-54.7545 StartZ=0 EndX=1.90272 EndY=-57.052 EndZ=0
    g141: LineSegment StartX=-5.39687 StartY=-60.4129 StartZ=0 EndX=1.90272 EndY=-57.052 EndZ=0
    g142: LineSegment StartX=-5.39687 StartY=-58.1154 StartZ=0 EndX=-5.39687 EndY=-60.4129 EndZ=0
    g143: LineSegment StartX=-15.3658 StartY=-51.6179 StartZ=0 EndX=-17.2452 EndY=-52.4833 EndZ=0
    g144: LineSegment StartX=-17.2452 StartY=-43.56 StartZ=0 EndX=-17.2452 EndY=-52.4833 EndZ=0
    g145: LineSegment StartX=-15.3658 StartY=-42.6946 StartZ=0 EndX=-17.2452 EndY=-43.56 EndZ=0
    g146: LineSegment StartX=-7.90684 StartY=-28.1729 StartZ=0 EndX=-7.90684 EndY=-25.8754 EndZ=0
    g147: LineSegment StartX=-0.607246 StartY=-22.5144 StartZ=0 EndX=-7.90684 EndY=-25.8754 EndZ=0
    g148: LineSegment StartX=-0.607246 StartY=-24.8119 StartZ=0 EndX=-0.607246 EndY=-22.5144 EndZ=0
    g149: LineSegment StartX=12.3478 StartY=0.37887 StartZ=0 EndX=10.5817 EndY=0.351499 EndZ=0
    g150: LineSegment StartX=13.0783 StartY=9.88617 StartZ=0 EndX=10.5817 EndY=0.351499 EndZ=0
    g151: LineSegment StartX=14.8444 StartY=9.91354 StartZ=0 EndX=13.0783 EndY=9.88617 EndZ=0
    g152: LineSegment StartX=26.0272 StartY=44.3529 StartZ=0 EndX=27.9727 EndY=43.3932 EndZ=0
    g153: LineSegment StartX=-19.1908 StartY=-51.5236 StartZ=0 EndX=-17.2452 EndY=-52.4833 EndZ=0
    g154: LineSegment StartX=-19.1908 StartY=-42.6003 StartZ=0 EndX=-17.2452 EndY=-43.56 EndZ=0
    g155: LineSegment StartX=-9.85237 StartY=-24.9157 StartZ=0 EndX=-7.90684 EndY=-25.8754 EndZ=0
    g156: LineSegment StartX=-2.55278 StartY=-21.5548 StartZ=0 EndX=-0.607246 EndY=-22.5144 EndZ=0
    g157: LineSegment StartX=8.63617 StartY=1.31113 StartZ=0 EndX=10.5817 EndY=0.351499 EndZ=0
    g158: LineSegment StartX=11.1328 StartY=10.8458 StartZ=0 EndX=13.0783 EndY=9.88617 EndZ=0
    g159: LineSegment StartX=-21.4227 StartY=-17.0893 StartZ=0 EndX=-21.5779 EndY=-17.1608 EndZ=0
    g160: ArcOfEllipse CenterX=-21.7121 CenterY=-17.2226 CenterZ=0 NormalX=0 NormalY=0 NormalZ=1 MajorRadius=0.186667 MinorRadius=0.118021 AngleXU=-2.02903 StartAngle=2.23331 EndAngle=2.71977
    g161: ArcOfEllipse CenterX=-21.7121 CenterY=-17.2226 CenterZ=0 NormalX=0 NormalY=0 NormalZ=1 MajorRadius=0.186667 MinorRadius=0.118021 AngleXU=-2.02903 StartAngle=4.21821 EndAngle=5.37491
    g162: LineSegment StartX=-21.8464 StartY=-17.2844 StartZ=0 EndX=-28.8775 EndY=-20.5217 EndZ=0
    g163: ArcOfEllipse CenterX=-29.0117 CenterY=-20.5835 CenterZ=0 NormalX=0 NormalY=0 NormalZ=1 MajorRadius=0.186667 MinorRadius=0.118021 AngleXU=-2.02903 StartAngle=2.23331 EndAngle=3.14159
    g164: ArcOfEllipse CenterX=-29.0117 CenterY=-20.5835 CenterZ=0 NormalX=0 NormalY=0 NormalZ=1 MajorRadius=0.186667 MinorRadius=0.118021 AngleXU=-2.02903 StartAngle=3.14159 EndAngle=5.37491
    g165: LineSegment StartX=-29.146 StartY=-20.6453 StartZ=0 EndX=-29.7966 EndY=-20.9449 EndZ=0
    g166: LineSegment StartX=-50.6623 StartY=-30.5521 StartZ=0 EndX=-55.8464 EndY=-32.939 EndZ=0
    g167: ArcOfEllipse CenterX=-55.9807 CenterY=-33.0008 CenterZ=0 NormalX=0 NormalY=0 NormalZ=1 MajorRadius=0.186667 MinorRadius=0.118021 AngleXU=-2.02903 StartAngle=2.23331 EndAngle=3.14159
    g168: ArcOfEllipse CenterX=-55.9807 CenterY=-33.0008 CenterZ=0 NormalX=0 NormalY=0 NormalZ=1 MajorRadius=0.186667 MinorRadius=0.118021 AngleXU=-2.02903 StartAngle=3.14159 EndAngle=5.37491
    g169: LineSegment StartX=-56.1149 StartY=-33.0626 StartZ=0 EndX=-56.2949 EndY=-33.1455 EndZ=0
    g170: LineSegment StartX=-51.6477 StartY=-4.53477 StartZ=0 EndX=-51.6477 EndY=-5.86228 EndZ=0
    g171: LineSegment StartX=-51.6477 StartY=-4.53477 StartZ=0 EndX=-54.6407 EndY=-5.91286 EndZ=0
    g172: LineSegment StartX=-51.6477 StartY=-5.86228 StartZ=0 EndX=-51.9339 EndY=-5.99408 EndZ=0
    g173: LineSegment StartX=-21.7115 StartY=-17.0949 StartZ=0 EndX=-21.5779 EndY=-17.1608 EndZ=0
    g174: ArcOfEllipse CenterX=-21.7121 CenterY=-17.2226 CenterZ=0 NormalX=0 NormalY=0 NormalZ=1 MajorRadius=0.186667 MinorRadius=0.118021 AngleXU=-2.02903 StartAngle=5.37491 EndAngle=5.99296
    g175: ArcOfEllipse CenterX=-29.0117 CenterY=-20.5835 CenterZ=0 NormalX=0 NormalY=0 NormalZ=1 MajorRadius=0.186667 MinorRadius=0.118021 AngleXU=-2.02903 StartAngle=1.77522 EndAngle=2.23331
    g176: ArcOfEllipse CenterX=-55.9807 CenterY=-33.0008 CenterZ=0 NormalX=0 NormalY=0 NormalZ=1 MajorRadius=0.186667 MinorRadius=0.118021 AngleXU=-2.02903 StartAngle=1.77522 EndAngle=2.23331
    g177: LineSegment StartX=-51.6477 StartY=-5.86228 StartZ=0 EndX=-53.0396 EndY=-5.17568 EndZ=0
    g178: ArcOfEllipse CenterX=40.4421 CenterY=-38.8249 CenterZ=0 NormalX=0 NormalY=0 NormalZ=1 MajorRadius=0.4 MinorRadius=0.244343 AngleXU=2.00229 StartAngle=2.95935 EndAngle=3.14159
    g179: ArcOfEllipse CenterX=40.4421 CenterY=-38.8249 CenterZ=0 NormalX=0 NormalY=0 NormalZ=1 MajorRadius=0.4 MinorRadius=0.244343 AngleXU=2.00229 StartAngle=3.14159 EndAngle=4.0665
    g180: LineSegment StartX=40.72 StartY=-38.962 StartZ=0 EndX=40.72 EndY=-37.0694 EndZ=0
    g181: ArcOfEllipse CenterX=40.4421 CenterY=-36.9323 CenterZ=0 NormalX=0 NormalY=0 NormalZ=1 MajorRadius=0.4 MinorRadius=0.244343 AngleXU=2.00229 StartAngle=4.0665 EndAngle=5.63729
    g182: LineSegment StartX=40.4421 StartY=-36.5807 StartZ=0 EndX=39.7976 EndY=-36.2628 EndZ=0
    g183: ArcOfEllipse CenterX=40.4421 CenterY=-35.5257 CenterZ=0 NormalX=0 NormalY=0 NormalZ=1 MajorRadius=0.4 MinorRadius=0.244343 AngleXU=2.00229 StartAngle=3.14159 EndAngle=4.0665
    g184: LineSegment StartX=40.72 StartY=-35.6628 StartZ=0 EndX=40.72 EndY=-20.2118 EndZ=0
    g185: LineSegment StartX=40.72 StartY=-11.4644 StartZ=0 EndX=40.72 EndY=21.5475 EndZ=0
    g186: LineSegment StartX=40.72 StartY=30.2949 StartZ=0 EndX=40.72 EndY=45.7459 EndZ=0
    g187: ArcOfEllipse CenterX=40.4421 CenterY=45.883 CenterZ=0 NormalX=0 NormalY=0 NormalZ=1 MajorRadius=0.4 MinorRadius=0.244343 AngleXU=2.00229 StartAngle=4.0665 EndAngle=5.63729
    g188: LineSegment StartX=39.7976 StartY=46.5525 StartZ=0 EndX=40.4421 EndY=46.2346 EndZ=0
    g189: ArcOfEllipse CenterX=40.4421 CenterY=47.2896 CenterZ=0 NormalX=0 NormalY=0 NormalZ=1 MajorRadius=0.4 MinorRadius=0.244343 AngleXU=2.00229 StartAngle=3.14159 EndAngle=4.0665
    g190: LineSegment StartX=40.72 StartY=47.1525 StartZ=0 EndX=40.72 EndY=49.0451 EndZ=0
    g191: ArcOfEllipse CenterX=40.4421 CenterY=49.1822 CenterZ=0 NormalX=0 NormalY=0 NormalZ=1 MajorRadius=0.4 MinorRadius=0.244343 AngleXU=2.00229 StartAngle=4.0665 EndAngle=5.17365
    g192: LineSegment StartX=40.5664 StartY=49.4354 StartZ=0 EndX=39.3304 EndY=50.8271 EndZ=0
    g193: LineSegment StartX=32.2339 StartY=53.4602 StartZ=0 EndX=33.38 EndY=53.2835 EndZ=0
    g194: ArcOfEllipse CenterX=32.1619 CenterY=53.8354 CenterZ=0 NormalX=0 NormalY=0 NormalZ=1 MajorRadius=0.4 MinorRadius=0.244343 AngleXU=-1.1393 StartAngle=5.63729 EndAngle=5.89909
    g195: LineSegment StartX=17.9121 StartY=60.5125 StartZ=0 EndX=32.1619 EndY=53.4837 EndZ=0
    g196: LineSegment StartX=-3.25123 StartY=70.9513 StartZ=0 EndX=10.9986 EndY=63.9226 EndZ=0
    g197: ArcOfEllipse CenterX=-3.25123 CenterY=71.303 CenterZ=0 NormalX=0 NormalY=0 NormalZ=1 MajorRadius=0.4 MinorRadius=0.244343 AngleXU=-1.1393 StartAngle=5.37549 EndAngle=5.63729
    g198: LineSegment StartX=-8.47412 StartY=75.2858 StartZ=0 EndX=-3.32316 EndY=70.9988 EndZ=0
    g199: ArcOfEllipse CenterX=38.4284 CenterY=-39.7521 CenterZ=0 NormalX=0 NormalY=0 NormalZ=1 MajorRadius=0.4 MinorRadius=0.244343 AngleXU=2.00229 StartAngle=3.14159 EndAngle=4.0665
    g200: LineSegment StartX=38.7063 StartY=-39.8892 StartZ=0 EndX=38.7063 EndY=-37.9966 EndZ=0
    g201: ArcOfEllipse CenterX=38.4284 CenterY=-36.4529 CenterZ=0 NormalX=0 NormalY=0 NormalZ=1 MajorRadius=0.4 MinorRadius=0.244343 AngleXU=2.00229 StartAngle=3.14159 EndAngle=4.0665
    g202: LineSegment StartX=38.7063 StartY=-36.5899 StartZ=0 EndX=38.7063 EndY=-21.139 EndZ=0
    g203: LineSegment StartX=38.6453 StartY=-21.1089 StartZ=0 EndX=38.7063 EndY=-21.139 EndZ=0
    g204: LineSegment StartX=38.5755 StartY=-12.327 StartZ=0 EndX=38.7063 EndY=-12.3915 EndZ=0
    g205: LineSegment StartX=38.7063 StartY=-12.3915 StartZ=0 EndX=38.7063 EndY=20.6203 EndZ=0
    g206: LineSegment StartX=38.6453 StartY=20.6504 StartZ=0 EndX=38.7063 EndY=20.6203 EndZ=0
    g207: LineSegment StartX=38.5755 StartY=29.4323 StartZ=0 EndX=38.7063 EndY=29.3678 EndZ=0
    g208: LineSegment StartX=38.7063 StartY=29.3678 StartZ=0 EndX=38.7063 EndY=44.8187 EndZ=0
    g209: ArcOfEllipse CenterX=38.4284 CenterY=44.9558 CenterZ=0 NormalX=0 NormalY=0 NormalZ=1 MajorRadius=0.4 MinorRadius=0.244343 AngleXU=2.00229 StartAngle=4.0665 EndAngle=5.63729
    g210: ArcOfEllipse CenterX=38.4284 CenterY=46.3624 CenterZ=0 NormalX=0 NormalY=0 NormalZ=1 MajorRadius=0.4 MinorRadius=0.244343 AngleXU=2.00229 StartAngle=3.14159 EndAngle=4.0665
    g211: LineSegment StartX=38.7063 StartY=46.2254 StartZ=0 EndX=38.7063 EndY=48.118 EndZ=0
    g212: ArcOfEllipse CenterX=38.4284 CenterY=48.2551 CenterZ=0 NormalX=0 NormalY=0 NormalZ=1 MajorRadius=0.4 MinorRadius=0.244343 AngleXU=2.00229 StartAngle=4.73274 EndAngle=5.17365
    g213: LineSegment StartX=38.5527 StartY=48.5083 StartZ=0 EndX=37.3167 EndY=49.8999 EndZ=0
    g214: LineSegment StartX=37.3167 StartY=49.8999 StartZ=0 EndX=37.3167 EndY=49.0208 EndZ=0
    g215: LineSegment StartX=30.2202 StartY=52.5331 StartZ=0 EndX=31.3663 EndY=52.3563 EndZ=0
    g216: ArcOfEllipse CenterX=30.1482 CenterY=52.9082 CenterZ=0 NormalX=0 NormalY=0 NormalZ=1 MajorRadius=0.4 MinorRadius=0.244343 AngleXU=-1.1393 StartAngle=5.63729 EndAngle=5.89909
    g217: LineSegment StartX=15.8985 StartY=59.5853 StartZ=0 EndX=30.1482 EndY=52.5566 EndZ=0
    g218: LineSegment StartX=15.8985 StartY=59.5853 StartZ=0 EndX=15.8985 EndY=59.4685 EndZ=0
    g219: LineSegment StartX=8.98488 StartY=62.9954 StartZ=0 EndX=8.98488 EndY=62.9471 EndZ=0
    g220: LineSegment StartX=-5.26491 StartY=70.0241 StartZ=0 EndX=8.98488 EndY=62.9954 EndZ=0
    g221: ArcOfEllipse CenterX=-5.26491 CenterY=70.3758 CenterZ=0 NormalX=0 NormalY=0 NormalZ=1 MajorRadius=0.4 MinorRadius=0.244343 AngleXU=-1.1393 StartAngle=5.37549 EndAngle=5.63729
    g222: LineSegment StartX=-10.4878 StartY=74.3586 StartZ=0 EndX=-5.33684 EndY=70.0716 EndZ=0
    g223: LineSegment StartX=-10.4878 StartY=72.6003 StartZ=0 EndX=-10.4878 EndY=74.3586 EndZ=0
    g224: LineSegment StartX=12.9921 StartY=-9.66424 StartZ=0 EndX=17.9011 EndY=-12.0856 EndZ=0
    g225: LineSegment StartX=38.7063 StartY=-21.139 StartZ=0 EndX=40.72 EndY=-20.2118 EndZ=0
    g226: LineSegment StartX=38.7063 StartY=-12.3915 StartZ=0 EndX=40.72 EndY=-11.4644 EndZ=0
    g227: LineSegment StartX=38.7063 StartY=20.6203 StartZ=0 EndX=40.72 EndY=21.5475 EndZ=0
    g228: LineSegment StartX=38.7063 StartY=29.3678 StartZ=0 EndX=40.72 EndY=30.2949 EndZ=0
    g229: LineSegment StartX=39.3304 StartY=50.8271 StartZ=0 EndX=37.3167 EndY=49.8999 EndZ=0
    g230: LineSegment StartX=15.8985 StartY=59.5853 StartZ=0 EndX=17.9121 EndY=60.5125 EndZ=0
    g231: LineSegment StartX=8.98488 StartY=62.9954 StartZ=0 EndX=10.9986 EndY=63.9226 EndZ=0
    g232: LineSegment StartX=-8.47412 StartY=75.2858 StartZ=0 EndX=-10.4878 EndY=74.3586 EndZ=0
    g233: BSplineCurve PolesCount=15 KnotsCount=15 Degree=1 IsPeriodic=0
    g234: BSplineCurve PolesCount=15 KnotsCount=15 Degree=1 IsPeriodic=0
    g235: LineSegment StartX=-30.8011 StartY=-1.90715 StartZ=0 EndX=-37.3439 EndY=1.32008 EndZ=0
    g236: BSplineCurve PolesCount=15 KnotsCount=15 Degree=1 IsPeriodic=0
    g237: BSplineCurve PolesCount=15 KnotsCount=15 Degree=1 IsPeriodic=0
    g238: BSplineCurve PolesCount=15 KnotsCount=15 Degree=1 IsPeriodic=0
    g239: BSplineCurve PolesCount=15 KnotsCount=15 Degree=1 IsPeriodic=0
    g240: LineSegment StartX=-4.53647 StartY=-14.8622 StartZ=0 EndX=-11.0792 EndY=-11.635 EndZ=0
    g241: BSplineCurve PolesCount=15 KnotsCount=15 Degree=1 IsPeriodic=0
    g242: BSplineCurve PolesCount=15 KnotsCount=15 Degree=1 IsPeriodic=0
    g243: LineSegment StartX=4.9631 StartY=-21.1062 StartZ=0 EndX=4.57454 EndY=-20.9146 EndZ=0
    g244: LineSegment StartX=10.6063 StartY=0.445437 StartZ=0 EndX=4.9631 EndY=-21.1062 EndZ=0
    g245: LineSegment StartX=8.80576 StartY=1.33356 StartZ=0 EndX=10.6063 EndY=0.445437 EndZ=0
    g246: LineSegment StartX=11.2532 StartY=10.6804 StartZ=0 EndX=13.0537 EndY=9.79224 EndZ=0
    g247: LineSegment StartX=18.8348 StartY=31.8705 StartZ=0 EndX=13.0537 EndY=9.79224 EndZ=0
    g248: LineSegment StartX=-18.8727 StartY=5.6191 StartZ=0 EndX=-16.7882 EndY=4.59092 EndZ=0
    g249: ArcOfEllipse CenterX=-19.3647 CenterY=3.74035 CenterZ=0 NormalX=0 NormalY=0 NormalZ=1 MajorRadius=2 MinorRadius=1.47402 AngleXU=1.58629 StartAngle=5.92193 EndAngle=6.28319
    g250: ArcOfEllipse CenterX=-19.3647 CenterY=3.74035 CenterZ=0 NormalX=0 NormalY=0 NormalZ=1 MajorRadius=2 MinorRadius=1.47402 AngleXU=1.58629 StartAngle=7e-16 EndAngle=2.78033
    g251: ArcOfEllipse CenterX=-17.2802 CenterY=2.71217 CenterZ=0 NormalX=0 NormalY=0 NormalZ=1 MajorRadius=2 MinorRadius=1.47402 AngleXU=1.58629 StartAngle=2.78033 EndAngle=3.14159
    g252: ArcOfEllipse CenterX=-17.2802 CenterY=2.71217 CenterZ=0 NormalX=0 NormalY=0 NormalZ=1 MajorRadius=2 MinorRadius=1.47402 AngleXU=1.58629 StartAngle=3.14159 EndAngle=5.92193
    g253: LineSegment StartX=-19.8566 StartY=1.86159 StartZ=0 EndX=-17.7721 EndY=0.833414 EndZ=0
    g254: LineSegment StartX=12.4985 StartY=0.474762 StartZ=0 EndX=6.85534 EndY=-21.0769 EndZ=0
    g255: LineSegment StartX=12.425 StartY=0.511059 StartZ=0 EndX=12.4985 EndY=0.474762 EndZ=0
    g256: LineSegment StartX=20.727 StartY=31.8998 StartZ=0 EndX=14.946 EndY=9.82156 EndZ=0
    g257: ArcOfEllipse CenterX=-17.4724 CenterY=3.76967 CenterZ=0 NormalX=0 NormalY=0 NormalZ=1 MajorRadius=2 MinorRadius=1.47402 AngleXU=1.58629 StartAngle=0.631705 EndAngle=2.78033
    g258: LineSegment StartX=-16.3848 StartY=1.11181 StartZ=0 EndX=-17.9644 EndY=1.89092 EndZ=0
    g259: LineSegment StartX=-30.8011 StartY=-1.90715 StartZ=0 EndX=-30.6924 EndY=-1.85709 EndZ=0
    g260: LineSegment StartX=-4.53647 StartY=-14.8622 StartZ=0 EndX=-4.42775 EndY=-14.8122 EndZ=0
    g261: LineSegment StartX=4.9631 StartY=-21.1062 StartZ=0 EndX=6.85534 EndY=-21.0769 EndZ=0
    g262: LineSegment StartX=12.4985 StartY=0.474762 StartZ=0 EndX=10.6063 EndY=0.445437 EndZ=0
    g263: LineSegment StartX=14.946 StartY=9.82156 StartZ=0 EndX=13.0537 EndY=9.79224 EndZ=0
    g264: LineSegment StartX=18.8348 StartY=31.8705 StartZ=0 EndX=20.727 EndY=31.8998 EndZ=0
    g265: LineSegment StartX=-67.7609 StartY=-3.33773 StartZ=0 EndX=-67.7168 EndY=-3.35947 EndZ=0
    g266: LineSegment StartX=-66.3712 StartY=-4.02319 StartZ=0 EndX=-66.2694 EndY=-4.07342 EndZ=0
    g267: LineSegment StartX=-59.2873 StartY=-7.51734 StartZ=0 EndX=-53.0316 EndY=-10.603 EndZ=0
    g268: LineSegment StartX=-0.679163 StartY=-25.0091 StartZ=0 EndX=4.57454 EndY=-22.5902 EndZ=0
    g269: LineSegment StartX=-0.73439 StartY=-24.9819 StartZ=0 EndX=-0.679163 EndY=-25.0091 EndZ=0
    g270: LineSegment StartX=-15.2315 StartY=-31.7095 StartZ=0 EndX=-7.83492 EndY=-28.3038 EndZ=0
    g271: LineSegment StartX=-15.4165 StartY=-31.6183 StartZ=0 EndX=-15.2315 EndY=-31.7095 EndZ=0
    g272: ArcOfEllipse CenterX=-52.9849 CenterY=-6.12613 CenterZ=0 NormalX=0 NormalY=0 NormalZ=1 MajorRadius=5 MinorRadius=2.38279 AngleXU=0 StartAngle=2.33898 EndAngle=2.59879
    g273: ArcOfEllipse CenterX=-52.9849 CenterY=-6.12613 CenterZ=0 NormalX=0 NormalY=0 NormalZ=1 MajorRadius=5 MinorRadius=2.38279 AngleXU=0 StartAngle=0.542803 EndAngle=2.33898
    g274: ArcOfEllipse CenterX=-44.5743 CenterY=-8.89471 CenterZ=0 NormalX=0 NormalY=0 NormalZ=1 MajorRadius=3 MinorRadius=1.42967 AngleXU=0 StartAngle=1.03703 EndAngle=2.10456
    g275: ArcOfEllipse CenterX=-26.3772 CenterY=-21.057 CenterZ=0 NormalX=0 NormalY=0 NormalZ=1 MajorRadius=6 MinorRadius=2.85934 AngleXU=0 StartAngle=1.97336 EndAngle=2.6966
    g276: ArcOfEllipse CenterX=-21.4256 CenterY=-18.7573 CenterZ=0 NormalX=0 NormalY=0 NormalZ=1 MajorRadius=3.5 MinorRadius=1.66795 AngleXU=0 StartAngle=0.745065 EndAngle=1.97336
    g277: LineSegment StartX=-22.7969 StartY=-17.2227 StartZ=0 EndX=-28.7278 EndY=-18.4262 EndZ=0
    g278: ArcOfEllipse CenterX=-15.3364 CenterY=-24.6277 CenterZ=0 NormalX=0 NormalY=0 NormalZ=1 MajorRadius=5 MinorRadius=2.38279 AngleXU=0 StartAngle=2.33898 EndAngle=2.59879
    g279: ArcOfEllipse CenterX=-15.3364 CenterY=-24.6277 CenterZ=0 NormalX=0 NormalY=0 NormalZ=1 MajorRadius=5 MinorRadius=2.38279 AngleXU=0 StartAngle=1.73769 EndAngle=2.33898
    g280: ArcOfEllipse CenterX=-29.472 CenterY=-13.2082 CenterZ=0 NormalX=0 NormalY=0 NormalZ=1 MajorRadius=7.5 MinorRadius=3.57418 AngleXU=0 StartAngle=2.33898 EndAngle=2.79004
    g281: ArcOfEllipse CenterX=-29.472 CenterY=-13.2082 CenterZ=0 NormalX=0 NormalY=0 NormalZ=1 MajorRadius=7.5 MinorRadius=3.57418 AngleXU=0 StartAngle=0.351556 EndAngle=2.33898
    g282: ArcOfEllipse CenterX=-52.9019 CenterY=-10.6669 CenterZ=0 NormalX=0 NormalY=0 NormalZ=1 MajorRadius=0.186667 MinorRadius=0.0889574 AngleXU=-3.14159 StartAngle=0.768187 EndAngle=2.33898
    g283: ArcOfEllipse CenterX=-52.9019 CenterY=-10.6669 CenterZ=0 NormalX=0 NormalY=0 NormalZ=1 MajorRadius=0.186667 MinorRadius=0.0889574 AngleXU=-3.14159 StartAngle=3.14159 EndAngle=5.48058
    g284: ArcOfEllipse CenterX=-52.9019 CenterY=-10.6669 CenterZ=0 NormalX=0 NormalY=0 NormalZ=1 MajorRadius=0.186667 MinorRadius=0.0889574 AngleXU=-3.14159 StartAngle=2.33898 EndAngle=3.14159
    g285: LineSegment StartX=-38.4784 StartY=1.10734 StartZ=0 EndX=-47.9548 EndY=5.78156 EndZ=0
    g286: ArcOfEllipse CenterX=-38.3487 CenterY=1.04337 CenterZ=0 NormalX=0 NormalY=0 NormalZ=1 MajorRadius=0.186667 MinorRadius=0.0889574 AngleXU=-3.14159 StartAngle=0 EndAngle=2.33898
    g287: ArcOfEllipse CenterX=-38.3487 CenterY=1.04337 CenterZ=0 NormalX=0 NormalY=0 NormalZ=1 MajorRadius=0.186667 MinorRadius=0.0889574 AngleXU=-3.14159 StartAngle=5.48058 EndAngle=6.28319
    g288: LineSegment StartX=-31.4259 StartY=-2.37133 StartZ=0 EndX=-38.219 EndY=0.97939 EndZ=0
    g289: ArcOfEllipse CenterX=-31.2962 CenterY=-2.43531 CenterZ=0 NormalX=0 NormalY=0 NormalZ=1 MajorRadius=0.186667 MinorRadius=0.0889574 AngleXU=-3.14159 StartAngle=0 EndAngle=2.33898
    g290: ArcOfEllipse CenterX=-31.2962 CenterY=-2.43531 CenterZ=0 NormalX=0 NormalY=0 NormalZ=1 MajorRadius=0.186667 MinorRadius=0.0889574 AngleXU=-3.14159 StartAngle=5.48058 EndAngle=6.28319
    g291: LineSegment StartX=-12.2138 StartY=-11.8477 StartZ=0 EndX=-31.1665 EndY=-2.49928 EndZ=0
    g292: ArcOfEllipse CenterX=-12.0841 CenterY=-11.9117 CenterZ=0 NormalX=0 NormalY=0 NormalZ=1 MajorRadius=0.186667 MinorRadius=0.0889574 AngleXU=-3.14159 StartAngle=0 EndAngle=2.33898
    g293: ArcOfEllipse CenterX=-12.0841 CenterY=-11.9117 CenterZ=0 NormalX=0 NormalY=0 NormalZ=1 MajorRadius=0.186667 MinorRadius=0.0889574 AngleXU=-3.14159 StartAngle=5.48058 EndAngle=6.28319
    g294: LineSegment StartX=-5.16122 StartY=-15.3264 StartZ=0 EndX=-11.9544 EndY=-11.9757 EndZ=0
    g295: ArcOfEllipse CenterX=-5.03152 CenterY=-15.3904 CenterZ=0 NormalX=0 NormalY=0 NormalZ=1 MajorRadius=0.186667 MinorRadius=0.0889574 AngleXU=-3.14159 StartAngle=0 EndAngle=2.33898
    g296: ArcOfEllipse CenterX=-5.03152 CenterY=-15.3904 CenterZ=0 NormalX=0 NormalY=0 NormalZ=1 MajorRadius=0.186667 MinorRadius=0.0889574 AngleXU=-3.14159 StartAngle=5.48058 EndAngle=6.28319
    g297: LineSegment StartX=-3.1855 StartY=-16.3009 StartZ=0 EndX=-4.90181 EndY=-15.4543 EndZ=0
    g298: LineSegment StartX=-0.679163 StartY=-22.5475 StartZ=0 EndX=4.57454 EndY=-20.1286 EndZ=0
    g299: LineSegment StartX=-2.47971 StartY=-21.6594 StartZ=0 EndX=-0.679163 EndY=-22.5475 EndZ=0
    g300: LineSegment StartX=-9.63547 StartY=-24.9541 StartZ=0 EndX=-7.83492 EndY=-25.8422 EndZ=0
    g301: LineSegment StartX=-15.2315 StartY=-29.2479 StartZ=0 EndX=-7.83492 EndY=-25.8422 EndZ=0
    g302: LineSegment StartX=-29.9608 StartY=-21.9826 StartZ=0 EndX=-23.7303 EndY=-25.0559 EndZ=0
    g303: ArcOfEllipse CenterX=-30.0905 CenterY=-21.9187 CenterZ=0 NormalX=0 NormalY=0 NormalZ=1 MajorRadius=0.186667 MinorRadius=0.0889574 AngleXU=-3.14159 StartAngle=3.14159 EndAngle=5.48058
    g304: ArcOfEllipse CenterX=-30.0905 CenterY=-21.9187 CenterZ=0 NormalX=0 NormalY=0 NormalZ=1 MajorRadius=0.186667 MinorRadius=0.0889574 AngleXU=-3.14159 StartAngle=2.33898 EndAngle=3.14159
    g305: LineSegment StartX=-37.0134 StartY=-18.504 StartZ=0 EndX=-30.2202 EndY=-21.8547 EndZ=0
    g306: ArcOfEllipse CenterX=-37.1431 CenterY=-18.44 CenterZ=0 NormalX=0 NormalY=0 NormalZ=1 MajorRadius=0.186667 MinorRadius=0.0889574 AngleXU=-3.14159 StartAngle=3.14159 EndAngle=5.48058
    g307: ArcOfEllipse CenterX=-37.1431 CenterY=-18.44 CenterZ=0 NormalX=0 NormalY=0 NormalZ=1 MajorRadius=0.186667 MinorRadius=0.0889574 AngleXU=-3.14159 StartAngle=2.33898 EndAngle=3.14159
    g308: LineSegment StartX=-45.7196 StartY=-14.2096 StartZ=0 EndX=-37.2728 EndY=-18.376 EndZ=0
    g309: ArcOfEllipse CenterX=-45.8493 CenterY=-14.1456 CenterZ=0 NormalX=0 NormalY=0 NormalZ=1 MajorRadius=0.186667 MinorRadius=0.0889574 AngleXU=-3.14159 StartAngle=3.14159 EndAngle=5.48058
    g310: ArcOfEllipse CenterX=-45.8493 CenterY=-14.1456 CenterZ=0 NormalX=0 NormalY=0 NormalZ=1 MajorRadius=0.186667 MinorRadius=0.0889574 AngleXU=-3.14159 StartAngle=2.33898 EndAngle=3.14159
    g311: LineSegment StartX=-52.7722 StartY=-10.7309 StartZ=0 EndX=-45.979 EndY=-14.0816 EndZ=0
    g312: ArcOfEllipse CenterX=-52.9849 CenterY=-3.66453 CenterZ=0 NormalX=0 NormalY=0 NormalZ=1 MajorRadius=5 MinorRadius=2.38279 AngleXU=0 StartAngle=2.33898 EndAngle=3.14159
    g313: ArcOfEllipse CenterX=-52.9849 CenterY=-3.66453 CenterZ=0 NormalX=0 NormalY=0 NormalZ=1 MajorRadius=5 MinorRadius=2.38279 AngleXU=0 StartAngle=3.14159 EndAngle=6.28319
    g314: ArcOfEllipse CenterX=-52.9849 CenterY=-3.66453 CenterZ=0 NormalX=0 NormalY=0 NormalZ=1 MajorRadius=5 MinorRadius=2.38279 AngleXU=0 StartAngle=0 EndAngle=2.33898
    g315: ArcOfEllipse CenterX=-44.5743 CenterY=-6.43311 CenterZ=0 NormalX=0 NormalY=0 NormalZ=1 MajorRadius=3 MinorRadius=1.42967 AngleXU=0 StartAngle=2.33898 EndAngle=3.14159
    g316: ArcOfEllipse CenterX=-44.5743 CenterY=-6.43311 CenterZ=0 NormalX=0 NormalY=0 NormalZ=1 MajorRadius=3 MinorRadius=1.42967 AngleXU=0 StartAngle=3.14159 EndAngle=6.28319
    g317: ArcOfEllipse CenterX=-44.5743 CenterY=-6.43311 CenterZ=0 NormalX=0 NormalY=0 NormalZ=1 MajorRadius=3 MinorRadius=1.42967 AngleXU=0 StartAngle=0 EndAngle=2.33898
    g318: ArcOfEllipse CenterX=-42.1385 CenterY=-9.01449 CenterZ=0 NormalX=0 NormalY=0 NormalZ=1 MajorRadius=1.5 MinorRadius=0.714836 AngleXU=0 StartAngle=2.33898 EndAngle=3.14159
    g319: ArcOfEllipse CenterX=-42.1385 CenterY=-9.01449 CenterZ=0 NormalX=0 NormalY=0 NormalZ=1 MajorRadius=1.5 MinorRadius=0.714836 AngleXU=0 StartAngle=3.14159 EndAngle=5.48058
    g320: LineSegment StartX=-43.1808 StartY=-8.5004 StartZ=0 EndX=-41.3829 EndY=-7.67258 EndZ=0
    g321: LineSegment StartX=-41.0963 StartY=-9.52858 StartZ=0 EndX=-39.2984 EndY=-8.70076 EndZ=0
    g322: ArcOfEllipse CenterX=-40.3406 CenterY=-8.18667 CenterZ=0 NormalX=0 NormalY=0 NormalZ=1 MajorRadius=1.5 MinorRadius=0.714836 AngleXU=0 StartAngle=5.48058 EndAngle=6.28319
    g323: ArcOfEllipse CenterX=-40.3406 CenterY=-8.18667 CenterZ=0 NormalX=0 NormalY=0 NormalZ=1 MajorRadius=1.5 MinorRadius=0.714836 AngleXU=0 StartAngle=0 EndAngle=2.33898
    g324: LineSegment StartX=-20.9191 StartY=-19.7829 StartZ=0 EndX=-18.2418 EndY=-16.9884 EndZ=0
    g325: ArcOfEllipse CenterX=-26.3772 CenterY=-18.5954 CenterZ=0 NormalX=0 NormalY=0 NormalZ=1 MajorRadius=6 MinorRadius=2.85934 AngleXU=0 StartAngle=1.97336 EndAngle=3.14159
    g326: ArcOfEllipse CenterX=-26.3772 CenterY=-18.5954 CenterZ=0 NormalX=0 NormalY=0 NormalZ=1 MajorRadius=6 MinorRadius=2.85934 AngleXU=0 StartAngle=3.14159 EndAngle=5.85488
    g327: ArcOfEllipse CenterX=-21.4256 CenterY=-16.2957 CenterZ=0 NormalX=0 NormalY=0 NormalZ=1 MajorRadius=3.5 MinorRadius=1.66795 AngleXU=0 StartAngle=5.85488 EndAngle=6.28319
    g328: ArcOfEllipse CenterX=-21.4256 CenterY=-16.2957 CenterZ=0 NormalX=0 NormalY=0 NormalZ=1 MajorRadius=3.5 MinorRadius=1.66795 AngleXU=0 StartAngle=0 EndAngle=1.97336
    g329: LineSegment StartX=-22.7969 StartY=-14.761 StartZ=0 EndX=-28.7278 EndY=-15.9646 EndZ=0
    g330: ArcOfEllipse CenterX=-15.3364 CenterY=-22.1661 CenterZ=0 NormalX=0 NormalY=0 NormalZ=1 MajorRadius=5 MinorRadius=2.38279 AngleXU=0 StartAngle=2.33898 EndAngle=3.14159
    g331: ArcOfEllipse CenterX=-15.3364 CenterY=-22.1661 CenterZ=0 NormalX=0 NormalY=0 NormalZ=1 MajorRadius=5 MinorRadius=2.38279 AngleXU=0 StartAngle=3.14159 EndAngle=3.82804
    g332: ArcOfEllipse CenterX=-15.3364 CenterY=-22.1661 CenterZ=0 NormalX=0 NormalY=0 NormalZ=1 MajorRadius=5 MinorRadius=2.38279 AngleXU=0 StartAngle=0.849923 EndAngle=2.33898
    g333: ArcOfEllipse CenterX=-29.472 CenterY=-10.7466 CenterZ=0 NormalX=0 NormalY=0 NormalZ=1 MajorRadius=7.5 MinorRadius=3.57418 AngleXU=0 StartAngle=2.33898 EndAngle=3.14159
    g334: ArcOfEllipse CenterX=-29.472 CenterY=-10.7466 CenterZ=0 NormalX=0 NormalY=0 NormalZ=1 MajorRadius=7.5 MinorRadius=3.57418 AngleXU=0 StartAngle=3.14159 EndAngle=6.28319
    g335: ArcOfEllipse CenterX=-29.472 CenterY=-10.7466 CenterZ=0 NormalX=0 NormalY=0 NormalZ=1 MajorRadius=7.5 MinorRadius=3.57418 AngleXU=0 StartAngle=0 EndAngle=2.33898
    g336: LineSegment StartX=-38.4784 StartY=1.10734 StartZ=0 EndX=-38.4784 EndY=0.97939 EndZ=0
    g337: ArcOfEllipse CenterX=-38.3487 CenterY=1.04337 CenterZ=0 NormalX=0 NormalY=0 NormalZ=1 MajorRadius=0.186667 MinorRadius=0.0889574 AngleXU=-3.14159 StartAngle=3.14159 EndAngle=3.90978
    g338: ArcOfEllipse CenterX=-38.3487 CenterY=1.04337 CenterZ=0 NormalX=0 NormalY=0 NormalZ=1 MajorRadius=0.186667 MinorRadius=0.0889574 AngleXU=-3.14159 StartAngle=2.33898 EndAngle=3.14159
    g339: LineSegment StartX=-38.2145 StartY=1.10518 StartZ=0 EndX=-38.2145 EndY=0.981556 EndZ=0
    g340: LineSegment StartX=-31.1619 StartY=-2.3735 StartZ=0 EndX=-31.1619 EndY=-2.50153 EndZ=0
    g341: ArcOfEllipse CenterX=-31.2962 CenterY=-2.43531 CenterZ=0 NormalX=0 NormalY=0 NormalZ=1 MajorRadius=0.186667 MinorRadius=0.0889574 AngleXU=-3.14159 StartAngle=3.90978 EndAngle=5.48058
    g342: LineSegment StartX=-12.2138 StartY=-11.8477 StartZ=0 EndX=-12.2138 EndY=-11.9757 EndZ=0
    g343: ArcOfEllipse CenterX=-12.0841 CenterY=-11.9117 CenterZ=0 NormalX=0 NormalY=0 NormalZ=1 MajorRadius=0.186667 MinorRadius=0.0889574 AngleXU=-3.14159 StartAngle=3.14159 EndAngle=3.90978
    g344: ArcOfEllipse CenterX=-12.0841 CenterY=-11.9117 CenterZ=0 NormalX=0 NormalY=0 NormalZ=1 MajorRadius=0.186667 MinorRadius=0.0889574 AngleXU=-3.14159 StartAngle=2.33898 EndAngle=3.14159
    g345: LineSegment StartX=-11.9498 StartY=-11.8499 StartZ=0 EndX=-11.9498 EndY=-11.9735 EndZ=0
    g346: LineSegment StartX=-4.89727 StartY=-15.3286 StartZ=0 EndX=-4.89727 EndY=-15.4566 EndZ=0
    g347: ArcOfEllipse CenterX=-5.03152 CenterY=-15.3904 CenterZ=0 NormalX=0 NormalY=0 NormalZ=1 MajorRadius=0.186667 MinorRadius=0.0889574 AngleXU=-3.14159 StartAngle=3.90978 EndAngle=5.48058
    g348: LineSegment StartX=4.57454 StartY=-22.5902 StartZ=0 EndX=4.57454 EndY=-20.1286 EndZ=0
    g349: LineSegment StartX=-0.679163 StartY=-25.0091 StartZ=0 EndX=-0.679163 EndY=-22.5475 EndZ=0
    g350: LineSegment StartX=-7.83492 StartY=-28.3038 StartZ=0 EndX=-7.83492 EndY=-25.8422 EndZ=0
    g351: LineSegment StartX=-15.2315 StartY=-31.7095 StartZ=0 EndX=-15.2315 EndY=-29.2479 EndZ=0
    g352: ArcOfEllipse CenterX=-30.0905 CenterY=-21.9187 CenterZ=0 NormalX=0 NormalY=0 NormalZ=1 MajorRadius=0.186667 MinorRadius=0.0889574 AngleXU=-3.14159 StartAngle=0 EndAngle=0.768187
    g353: ArcOfEllipse CenterX=-30.0905 CenterY=-21.9187 CenterZ=0 NormalX=0 NormalY=0 NormalZ=1 MajorRadius=0.186667 MinorRadius=0.0889574 AngleXU=-3.14159 StartAngle=5.48058 EndAngle=6.28319
    g354: LineSegment StartX=-32.1042 StartY=-25.3074 StartZ=0 EndX=-39.1568 EndY=-21.8287 EndZ=0
    g355: ArcOfEllipse CenterX=-37.1431 CenterY=-18.44 CenterZ=0 NormalX=0 NormalY=0 NormalZ=1 MajorRadius=0.186667 MinorRadius=0.0889574 AngleXU=-3.14159 StartAngle=0.768187 EndAngle=2.33898
    g356: ArcOfEllipse CenterX=-45.8493 CenterY=-14.1456 CenterZ=0 NormalX=0 NormalY=0 NormalZ=1 MajorRadius=0.186667 MinorRadius=0.0889574 AngleXU=-3.14159 StartAngle=0 EndAngle=0.768187
    g357: ArcOfEllipse CenterX=-45.8493 CenterY=-14.1456 CenterZ=0 NormalX=0 NormalY=0 NormalZ=1 MajorRadius=0.186667 MinorRadius=0.0889574 AngleXU=-3.14159 StartAngle=5.48058 EndAngle=6.28319
    g358: LineSegment StartX=-47.863 StartY=-17.5344 StartZ=0 EndX=-54.9156 EndY=-14.0557 EndZ=0
    g359: LineSegment StartX=-53.0361 StartY=-10.7288 StartZ=0 EndX=-54.9156 EndY=-11.5941 EndZ=0
    g360: LineSegment StartX=-54.9156 StartY=-11.5941 StartZ=0 EndX=-54.9156 EndY=-14.0557 EndZ=0
    g361: LineSegment StartX=-47.863 StartY=-15.0728 StartZ=0 EndX=-54.9156 EndY=-11.5941 EndZ=0
    g362: LineSegment StartX=-45.9836 StartY=-14.2074 StartZ=0 EndX=-47.863 EndY=-15.0728 EndZ=0
    g363: LineSegment StartX=-31.1619 StartY=-2.3735 StartZ=0 EndX=-29.2825 EndY=-1.50815 EndZ=0
    g364: LineSegment StartX=-38.2145 StartY=1.10518 StartZ=0 EndX=-37.6106 EndY=1.38324 EndZ=0
    g365: LineSegment StartX=-4.89727 StartY=-15.3286 StartZ=0 EndX=-3.01784 EndY=-14.4632 EndZ=0
    g366: LineSegment StartX=-11.9498 StartY=-11.8499 StartZ=0 EndX=-11.3459 EndY=-11.5718 EndZ=0
    g367: LineSegment StartX=-37.2773 StartY=-18.5018 StartZ=0 EndX=-39.1568 EndY=-19.3671 EndZ=0
    g368: LineSegment StartX=-32.1042 StartY=-22.8458 StartZ=0 EndX=-39.1568 EndY=-19.3671 EndZ=0
    g369: LineSegment StartX=-30.2248 StartY=-21.9805 StartZ=0 EndX=-32.1042 EndY=-22.8458 EndZ=0
    g370: LineSegment StartX=-32.1042 StartY=-22.8458 StartZ=0 EndX=-32.1042 EndY=-25.3074 EndZ=0
    g371: LineSegment StartX=-39.1568 StartY=-19.3671 StartZ=0 EndX=-39.1568 EndY=-21.8287 EndZ=0
    g372: LineSegment StartX=-47.863 StartY=-15.0728 StartZ=0 EndX=-47.863 EndY=-17.5344 EndZ=0
    g373: LineSegment StartX=-66.4394 StartY=-43.3615 StartZ=0 EndX=-66.4394 EndY=-41.6032 EndZ=0
    g374: LineSegment StartX=-61.2884 StartY=-44.1559 StartZ=0 EndX=-66.4394 EndY=-43.3615 EndZ=0
    g375: ArcOfEllipse CenterX=-61.2165 CenterY=-44.5311 CenterZ=0 NormalX=0 NormalY=0 NormalZ=1 MajorRadius=0.4 MinorRadius=0.244343 AngleXU=2.00229 StartAngle=5.63729 EndAngle=5.89909
    g376: LineSegment StartX=-54.8461 StartY=-47.3216 StartZ=0 EndX=-61.2165 EndY=-44.1794 EndZ=0
    g377: LineSegment StartX=-54.8461 StartY=-47.3216 StartZ=0 EndX=-54.8461 EndY=-45.0434 EndZ=0
    g378: ArcOfEllipse CenterX=-54.7765 CenterY=-44.9252 CenterZ=0 NormalX=0 NormalY=0 NormalZ=1 MajorRadius=0.200333 MinorRadius=0.122375 AngleXU=2.00229 StartAngle=5.63729 EndAngle=6.28319
    g379: ArcOfEllipse CenterX=-54.7765 CenterY=-44.9252 CenterZ=0 NormalX=0 NormalY=0 NormalZ=1 MajorRadius=0.200333 MinorRadius=0.122375 AngleXU=2.00229 StartAngle=0 EndAngle=1.9721
    g380: ArcOfEllipse CenterX=-54.7765 CenterY=-44.9252 CenterZ=0 NormalX=0 NormalY=0 NormalZ=1 MajorRadius=0.200333 MinorRadius=0.122375 AngleXU=2.00229 StartAngle=4.5901 EndAngle=5.63729
    g381: LineSegment StartX=-54.6559 StartY=-44.8966 StartZ=0 EndX=-48.1226 EndY=-48.1192 EndZ=0
    g382: ArcOfEllipse CenterX=-48.0021 CenterY=-48.2667 CenterZ=0 NormalX=0 NormalY=0 NormalZ=1 MajorRadius=0.200333 MinorRadius=0.122375 AngleXU=2.00229 StartAngle=5.63729 EndAngle=6.28319
    g383: ArcOfEllipse CenterX=-48.0021 CenterY=-48.2667 CenterZ=0 NormalX=0 NormalY=0 NormalZ=1 MajorRadius=0.200333 MinorRadius=0.122375 AngleXU=2.00229 StartAngle=0 EndAngle=0.401306
    g384: ArcOfEllipse CenterX=-48.0021 CenterY=-48.2667 CenterZ=0 NormalX=0 NormalY=0 NormalZ=1 MajorRadius=0.200333 MinorRadius=0.122375 AngleXU=2.00229 StartAngle=3.0193 EndAngle=3.14159
    g385: ArcOfEllipse CenterX=-48.0021 CenterY=-48.2667 CenterZ=0 NormalX=0 NormalY=0 NormalZ=1 MajorRadius=0.200333 MinorRadius=0.122375 AngleXU=2.00229 StartAngle=3.14159 EndAngle=5.63729
    g386: LineSegment StartX=-47.9325 StartY=-50.7317 StartZ=0 EndX=-47.9325 EndY=-48.4536 EndZ=0
    g387: LineSegment StartX=-39.0873 StartY=-55.0946 StartZ=0 EndX=-47.9325 EndY=-50.7317 EndZ=0
    g388: LineSegment StartX=-39.0873 StartY=-55.0946 StartZ=0 EndX=-39.0873 EndY=-52.8165 EndZ=0
    g389: ArcOfEllipse CenterX=-39.0177 CenterY=-52.6983 CenterZ=0 NormalX=0 NormalY=0 NormalZ=1 MajorRadius=0.200333 MinorRadius=0.122375 AngleXU=2.00229 StartAngle=5.63729 EndAngle=6.28319
    g390: ArcOfEllipse CenterX=-39.0177 CenterY=-52.6983 CenterZ=0 NormalX=0 NormalY=0 NormalZ=1 MajorRadius=0.200333 MinorRadius=0.122375 AngleXU=2.00229 StartAngle=0 EndAngle=1.9721
    g391: ArcOfEllipse CenterX=-39.0177 CenterY=-52.6983 CenterZ=0 NormalX=0 NormalY=0 NormalZ=1 MajorRadius=0.200333 MinorRadius=0.122375 AngleXU=2.00229 StartAngle=4.5901 EndAngle=5.63729
    g392: LineSegment StartX=-38.8971 StartY=-52.6697 StartZ=0 EndX=-32.3638 EndY=-55.8922 EndZ=0
    g393: ArcOfEllipse CenterX=-32.2433 CenterY=-56.0397 CenterZ=0 NormalX=0 NormalY=0 NormalZ=1 MajorRadius=0.200333 MinorRadius=0.122375 AngleXU=2.00229 StartAngle=5.63729 EndAngle=6.28319
    g394: ArcOfEllipse CenterX=-32.2433 CenterY=-56.0397 CenterZ=0 NormalX=0 NormalY=0 NormalZ=1 MajorRadius=0.200333 MinorRadius=0.122375 AngleXU=2.00229 StartAngle=0 EndAngle=0.401306
    g395: ArcOfEllipse CenterX=-32.2433 CenterY=-56.0397 CenterZ=0 NormalX=0 NormalY=0 NormalZ=1 MajorRadius=0.200333 MinorRadius=0.122375 AngleXU=2.00229 StartAngle=3.0193 EndAngle=3.14159
    g396: ArcOfEllipse CenterX=-32.2433 CenterY=-56.0397 CenterZ=0 NormalX=0 NormalY=0 NormalZ=1 MajorRadius=0.200333 MinorRadius=0.122375 AngleXU=2.00229 StartAngle=3.14159 EndAngle=5.63729
    g397: LineSegment StartX=-32.1737 StartY=-58.5048 StartZ=0 EndX=-32.1737 EndY=-56.2266 EndZ=0
    g398: LineSegment StartX=-25.8033 StartY=-61.647 StartZ=0 EndX=-32.1737 EndY=-58.5048 EndZ=0
    g399: ArcOfEllipse CenterX=-25.8033 CenterY=-61.9986 CenterZ=0 NormalX=0 NormalY=0 NormalZ=1 MajorRadius=0.4 MinorRadius=0.244343 AngleXU=2.00229 StartAngle=5.37549 EndAngle=5.63729
    ... +425 more geometry lines
FEATURE [Sketcher::SketchObject] Sketch065
  ArcFitTolerance = 1e-06
  FullyConstrained = false
  MakeInternals = false
  sketch-geometry (1192):
    g0: ArcOfEllipse CenterX=-39.6322 CenterY=-6.20139 CenterZ=0 NormalX=0 NormalY=0 NormalZ=1 MajorRadius=1.25 MinorRadius=0.790319 AngleXU=-2.02903 StartAngle=2.69057 EndAngle=3.14159
    g1: ArcOfEllipse CenterX=-39.6322 CenterY=-6.20139 CenterZ=0 NormalX=0 NormalY=0 NormalZ=1 MajorRadius=1.25 MinorRadius=0.790319 AngleXU=-2.02903 StartAngle=3.14159 EndAngle=5.67781
    g2: ArcOfEllipse CenterX=-39.6322 CenterY=-6.20139 CenterZ=0 NormalX=0 NormalY=0 NormalZ=1 MajorRadius=1.125 MinorRadius=0.711287 AngleXU=1.11256 StartAngle=-9e-16 EndAngle=2.72298
    g3: ArcOfEllipse CenterX=-37.4435 CenterY=-7.28098 CenterZ=0 NormalX=0 NormalY=0 NormalZ=1 MajorRadius=1.25 MinorRadius=0.790319 AngleXU=-2.02903 StartAngle=3.14159 EndAngle=6.28319
    g4: BSplineCurve PolesCount=87 KnotsCount=18 Degree=6 IsPeriodic=0
    g5: ArcOfEllipse CenterX=-9.68041 CenterY=-25.8653 CenterZ=0 NormalX=0 NormalY=0 NormalZ=1 MajorRadius=0.8 MinorRadius=0.381246 AngleXU=0 StartAngle=5.48058 EndAngle=6.28319
    g6: ArcOfEllipse CenterX=-15.4338 CenterY=-28.5143 CenterZ=0 NormalX=0 NormalY=0 NormalZ=1 MajorRadius=0.8 MinorRadius=0.381246 AngleXU=0 StartAngle=5.48058 EndAngle=6.28319
    g7: ArcOfEllipse CenterX=-20.9924 CenterY=-25.7725 CenterZ=0 NormalX=0 NormalY=0 NormalZ=1 MajorRadius=0.8 MinorRadius=0.381246 AngleXU=0 StartAngle=5.48058 EndAngle=6.28319
    g8: ArcOfEllipse CenterX=-15.3364 CenterY=-25.9947 CenterZ=0 NormalX=0 NormalY=0 NormalZ=1 MajorRadius=3.7 MinorRadius=1.76326 AngleXU=0 StartAngle=0.0498796 EndAngle=0.330297
    g9: ArcOfEllipse CenterX=-15.3364 CenterY=-25.8189 CenterZ=0 NormalX=0 NormalY=0 NormalZ=1 MajorRadius=3.7 MinorRadius=1.76326 AngleXU=0 StartAngle=5.48058 EndAngle=6.28319
    g10: ArcOfEllipse CenterX=-15.3364 CenterY=-25.8189 CenterZ=0 NormalX=0 NormalY=0 NormalZ=1 MajorRadius=3.7 MinorRadius=1.76326 AngleXU=0 StartAngle=0 EndAngle=0.330297
    g11: ArcOfEllipse CenterX=-15.3364 CenterY=-25.9947 CenterZ=0 NormalX=0 NormalY=0 NormalZ=1 MajorRadius=3.7 MinorRadius=1.76326 AngleXU=0 StartAngle=2.8113 EndAngle=3.09171
    g12: ArcOfEllipse CenterX=-15.3364 CenterY=-25.8189 CenterZ=0 NormalX=0 NormalY=0 NormalZ=1 MajorRadius=3.7 MinorRadius=1.76326 AngleXU=0 StartAngle=2.8113 EndAngle=3.14159
    g13: ArcOfEllipse CenterX=-15.3364 CenterY=-25.8189 CenterZ=0 NormalX=0 NormalY=0 NormalZ=1 MajorRadius=3.7 MinorRadius=1.76326 AngleXU=0 StartAngle=3.14159 EndAngle=5.48058
    g14: ArcOfEllipse CenterX=-20.9924 CenterY=-25.7725 CenterZ=0 NormalX=0 NormalY=0 NormalZ=1 MajorRadius=0.8 MinorRadius=0.381246 AngleXU=0 StartAngle=3.14159 EndAngle=5.48058
    g15: ArcOfEllipse CenterX=-15.4338 CenterY=-28.5143 CenterZ=0 NormalX=0 NormalY=0 NormalZ=1 MajorRadius=0.8 MinorRadius=0.381246 AngleXU=0 StartAngle=3.14159 EndAngle=5.48058
    g16: ArcOfEllipse CenterX=-9.68041 CenterY=-25.8653 CenterZ=0 NormalX=0 NormalY=0 NormalZ=1 MajorRadius=0.8 MinorRadius=0.381246 AngleXU=0 StartAngle=3.14159 EndAngle=5.48058
    g17: LineSegment StartX=-15.0522 StartY=-29.1338 StartZ=0 EndX=-8.39441 EndY=-26.0684 EndZ=0
    g18: LineSegment StartX=-8.39441 StartY=-26.0684 StartZ=0 EndX=-8.38051 EndY=-25.6835 EndZ=0
    g19: LineSegment StartX=-8.38051 StartY=-25.6835 StartZ=0 EndX=-11.8364 EndY=-23.9788 EndZ=0
    g20: LineSegment StartX=-18.8364 StartY=-23.9846 StartZ=0 EndX=-22.2784 EndY=-25.5694 EndZ=0
    g21: LineSegment StartX=-22.2784 StartY=-25.5694 StartZ=0 EndX=-22.2924 EndY=-25.9544 EndZ=0
    g22: LineSegment StartX=-22.2924 StartY=-25.9544 StartZ=0 EndX=-15.8599 EndY=-29.1272 EndZ=0
    g23: LineSegment StartX=-15.8599 StartY=-29.1272 StartZ=0 EndX=-15.0522 EndY=-29.1338 EndZ=0
    g24: LineSegment StartX=-12.1659 StartY=-27.9807 StartZ=0 EndX=-10.8238 EndY=-27.3627 EndZ=0
    g25: LineSegment StartX=-8.38959 StartY=-26.1108 StartZ=0 EndX=-8.38051 EndY=-25.8593 EndZ=0
    g26: LineSegment StartX=-8.39441 StartY=-26.0684 StartZ=0 EndX=-8.39441 EndY=-26.113 EndZ=0
    g27: LineSegment StartX=-15.0522 StartY=-29.1338 StartZ=0 EndX=-15.0522 EndY=-29.1412 EndZ=0
    g28: LineSegment StartX=-8.38051 StartY=-25.6835 StartZ=0 EndX=-8.38051 EndY=-25.8593 EndZ=0
    g29: LineSegment StartX=-22.2924 StartY=-25.9544 StartZ=0 EndX=-22.2924 EndY=-26.0036 EndZ=0
    g30: LineSegment StartX=-15.8599 StartY=-29.1272 StartZ=0 EndX=-15.8599 EndY=-29.1346 EndZ=0
    g31: ArcOfEllipse CenterX=-9.68041 CenterY=-25.6016 CenterZ=0 NormalX=0 NormalY=0 NormalZ=1 MajorRadius=0.8 MinorRadius=0.381246 AngleXU=-3.14159 StartAngle=0 EndAngle=2.33898
    g32: ArcOfEllipse CenterX=-9.68041 CenterY=-25.6016 CenterZ=0 NormalX=0 NormalY=0 NormalZ=1 MajorRadius=0.8 MinorRadius=0.381246 AngleXU=-3.14159 StartAngle=5.48058 EndAngle=6.28319
    g33: ArcOfEllipse CenterX=-15.4338 CenterY=-28.2506 CenterZ=0 NormalX=0 NormalY=0 NormalZ=1 MajorRadius=0.8 MinorRadius=0.381246 AngleXU=0 StartAngle=2.33898 EndAngle=3.14159
    g34: ArcOfEllipse CenterX=-15.4338 CenterY=-28.2506 CenterZ=0 NormalX=0 NormalY=0 NormalZ=1 MajorRadius=0.8 MinorRadius=0.381246 AngleXU=0 StartAngle=3.14159 EndAngle=3.90978
    g35: ArcOfEllipse CenterX=-15.4338 CenterY=-28.2506 CenterZ=0 NormalX=0 NormalY=0 NormalZ=1 MajorRadius=0.8 MinorRadius=0.381246 AngleXU=0 StartAngle=3.90978 EndAngle=5.48058
    g36: ArcOfEllipse CenterX=-20.9924 CenterY=-25.5088 CenterZ=0 NormalX=0 NormalY=0 NormalZ=1 MajorRadius=0.8 MinorRadius=0.381246 AngleXU=-3.14159 StartAngle=0.768187 EndAngle=2.33898
    g37: ArcOfEllipse CenterX=-20.9924 CenterY=-25.5088 CenterZ=0 NormalX=0 NormalY=0 NormalZ=1 MajorRadius=0.8 MinorRadius=0.381246 AngleXU=-3.14159 StartAngle=-9e-16 EndAngle=0.768187
    g38: ArcOfEllipse CenterX=-20.9924 CenterY=-25.5088 CenterZ=0 NormalX=0 NormalY=0 NormalZ=1 MajorRadius=0.8 MinorRadius=0.381246 AngleXU=-3.14159 StartAngle=5.48058 EndAngle=6.28319
    g39: ArcOfEllipse CenterX=-15.3364 CenterY=-25.9947 CenterZ=0 NormalX=0 NormalY=0 NormalZ=1 MajorRadius=3.5 MinorRadius=1.66795 AngleXU=0 StartAngle=3.14159 EndAngle=3.6708
    g40: ArcOfEllipse CenterX=-15.3364 CenterY=-25.9947 CenterZ=0 NormalX=0 NormalY=0 NormalZ=1 MajorRadius=3.5 MinorRadius=1.66795 AngleXU=0 StartAngle=5.75398 EndAngle=6.28319
    g41: ArcOfEllipse CenterX=-20.9924 CenterY=-25.5088 CenterZ=0 NormalX=0 NormalY=0 NormalZ=1 MajorRadius=0.8 MinorRadius=0.381246 AngleXU=-3.14159 StartAngle=3.14159 EndAngle=5.48058
    g42: ArcOfEllipse CenterX=-20.9924 CenterY=-25.5088 CenterZ=0 NormalX=0 NormalY=0 NormalZ=1 MajorRadius=0.8 MinorRadius=0.381246 AngleXU=-3.14159 StartAngle=2.33898 EndAngle=3.14159
    g43: ArcOfEllipse CenterX=-15.4338 CenterY=-28.2506 CenterZ=0 NormalX=0 NormalY=0 NormalZ=1 MajorRadius=0.8 MinorRadius=0.381246 AngleXU=0 StartAngle=5.48058 EndAngle=6.28319
    g44: ArcOfEllipse CenterX=-15.4338 CenterY=-28.2506 CenterZ=0 NormalX=0 NormalY=0 NormalZ=1 MajorRadius=0.8 MinorRadius=0.381246 AngleXU=0 StartAngle=0 EndAngle=2.33898
    g45: ArcOfEllipse CenterX=-9.68041 CenterY=-25.6016 CenterZ=0 NormalX=0 NormalY=0 NormalZ=1 MajorRadius=0.8 MinorRadius=0.381246 AngleXU=-3.14159 StartAngle=3.14159 EndAngle=3.90978
    g46: ArcOfEllipse CenterX=-9.68041 CenterY=-25.6016 CenterZ=0 NormalX=0 NormalY=0 NormalZ=1 MajorRadius=0.8 MinorRadius=0.381246 AngleXU=-3.14159 StartAngle=2.33898 EndAngle=3.14159
    g47: ArcOfEllipse CenterX=-9.68041 CenterY=-25.6016 CenterZ=0 NormalX=0 NormalY=0 NormalZ=1 MajorRadius=0.8 MinorRadius=0.381246 AngleXU=-3.14159 StartAngle=3.90978 EndAngle=5.48058
    g48: LineSegment StartX=-8.17911 StartY=-25.5577 StartZ=0 EndX=-11.8364 EndY=-23.7537 EndZ=0
    g49: LineSegment StartX=-8.19586 StartY=-26.0216 StartZ=0 EndX=-8.17911 EndY=-25.5577 EndZ=0
    g50: LineSegment StartX=-10.7932 StartY=-27.2175 StartZ=0 EndX=-8.19586 EndY=-26.0216 EndZ=0
    g51: ArcOfEllipse CenterX=-10.7238 CenterY=-27.2518 CenterZ=0 NormalX=0 NormalY=0 NormalZ=1 MajorRadius=0.1 MinorRadius=0.0476557 AngleXU=-3.14159 StartAngle=0 EndAngle=0.768187
    g52: ArcOfEllipse CenterX=-10.7238 CenterY=-27.2518 CenterZ=0 NormalX=0 NormalY=0 NormalZ=1 MajorRadius=0.1 MinorRadius=0.0476557 AngleXU=-3.14159 StartAngle=5.48058 EndAngle=6.28319
    g53: LineSegment StartX=-10.4483 StartY=-27.4562 StartZ=0 EndX=-10.7957 EndY=-27.2849 EndZ=0
    g54: LineSegment StartX=-10.4483 StartY=-27.4562 StartZ=0 EndX=-7.60023 EndY=-26.1449 EndZ=0
    g55: LineSegment StartX=-7.60023 StartY=-26.1449 StartZ=0 EndX=-7.57492 EndY=-25.4442 EndZ=0
    g56: LineSegment StartX=-7.57492 StartY=-25.4442 StartZ=0 EndX=-11.8364 EndY=-23.3422 EndZ=0
    g57: LineSegment StartX=-13.7565 StartY=-31.7927 StartZ=0 EndX=-8.57842 EndY=-29.4086 EndZ=0
    g58: LineSegment StartX=-22.1529 StartY=-29.2972 StartZ=0 EndX=-22.0235 EndY=-29.361 EndZ=0
    g59: LineSegment StartX=-21.113 StartY=-29.8101 StartZ=0 EndX=-18.5493 EndY=-31.0746 EndZ=0
    g60: LineSegment StartX=-17.6389 StartY=-31.5237 StartZ=0 EndX=-17.1501 EndY=-31.7648 EndZ=0
    g61: LineSegment StartX=-7.57492 StartY=-25.4442 StartZ=0 EndX=-7.57492 EndY=-28.5212 EndZ=0
    g62: LineSegment StartX=-18.8364 StartY=-23.6304 StartZ=0 EndX=-19.948 EndY=-24.1422 EndZ=0
    g63: LineSegment StartX=-20.2246 StartY=-24.0058 StartZ=0 EndX=-23.0726 EndY=-25.3171 EndZ=0
    g64: LineSegment StartX=-23.0979 StartY=-26.0178 StartZ=0 EndX=-23.0979 EndY=-29.0948 EndZ=0
    g65: LineSegment StartX=-23.0726 StartY=-25.3171 StartZ=0 EndX=-23.0979 EndY=-26.0178 EndZ=0
    g66: LineSegment StartX=-22.1529 StartY=-29.5609 StartZ=0 EndX=-23.0979 EndY=-29.0948 EndZ=0
    g67: LineSegment StartX=-22.1529 StartY=-29.5609 StartZ=0 EndX=-22.1529 EndY=-29.2972 EndZ=0
    g68: LineSegment StartX=-17.1501 StartY=-32.0286 StartZ=0 EndX=-17.1501 EndY=-31.7648 EndZ=0
    g69: LineSegment StartX=-16.205 StartY=-32.4947 StartZ=0 EndX=-17.1501 EndY=-32.0286 EndZ=0
    g70: LineSegment StartX=-16.205 StartY=-29.4177 StartZ=0 EndX=-16.205 EndY=-32.4947 EndZ=0
    g71: LineSegment StartX=-23.0979 StartY=-26.0178 StartZ=0 EndX=-16.205 EndY=-29.4177 EndZ=0
    g72: LineSegment StartX=-14.7346 StartY=-32.5068 StartZ=0 EndX=-16.205 EndY=-32.4947 EndZ=0
    g73: LineSegment StartX=-14.7346 StartY=-29.4298 StartZ=0 EndX=-14.7346 EndY=-32.5068 EndZ=0
    g74: LineSegment StartX=-16.205 StartY=-29.4177 StartZ=0 EndX=-14.7346 EndY=-29.4298 EndZ=0
    g75: LineSegment StartX=-10.4483 StartY=-27.72 StartZ=0 EndX=-10.4483 EndY=-27.4562 EndZ=0
    g76: LineSegment StartX=-11.8866 StartY=-28.3822 StartZ=0 EndX=-10.4483 EndY=-27.72 EndZ=0
    g77: LineSegment StartX=-11.8866 StartY=-28.3822 StartZ=0 EndX=-11.8866 EndY=-28.1185 EndZ=0
    g78: LineSegment StartX=-14.7346 StartY=-29.4298 StartZ=0 EndX=-11.8866 EndY=-28.1185 EndZ=0
    g79: LineSegment StartX=-13.7565 StartY=-32.0564 StartZ=0 EndX=-14.7346 EndY=-32.5068 EndZ=0
    g80: LineSegment StartX=-13.7565 StartY=-32.0564 StartZ=0 EndX=-13.7565 EndY=-31.7927 EndZ=0
    g81: LineSegment StartX=-8.57842 StartY=-29.6723 StartZ=0 EndX=-8.57842 EndY=-29.4086 EndZ=0
    g82: LineSegment StartX=-7.60023 StartY=-29.2219 StartZ=0 EndX=-8.57842 EndY=-29.6723 EndZ=0
    g83: LineSegment StartX=-7.60023 StartY=-26.1449 StartZ=0 EndX=-7.60023 EndY=-29.2219 EndZ=0
    g84: LineSegment StartX=-7.57492 StartY=-28.5212 StartZ=0 EndX=-7.60023 EndY=-29.2219 EndZ=0
    g85: LineSegment StartX=-12.234 StartY=-27.9471 StartZ=0 EndX=-11.8866 EndY=-28.1185 EndZ=0
    g86: ArcOfEllipse CenterX=-12.3059 CenterY=-27.9802 CenterZ=0 NormalX=0 NormalY=0 NormalZ=1 MajorRadius=0.1 MinorRadius=0.0476557 AngleXU=-3.14159 StartAngle=3.90978 EndAngle=5.48058
    g87: LineSegment StartX=-14.9728 StartY=-29.1419 StartZ=0 EndX=-12.3754 EndY=-27.946 EndZ=0
    g88: LineSegment StartX=-15.9462 StartY=-29.1339 StartZ=0 EndX=-14.9728 EndY=-29.1419 EndZ=0
    g89: LineSegment StartX=-22.4937 StartY=-25.9043 StartZ=0 EndX=-15.9462 EndY=-29.1339 EndZ=0
    g90: LineSegment StartX=-22.477 StartY=-25.4404 StartZ=0 EndX=-22.4937 EndY=-25.9043 EndZ=0
    g91: LineSegment StartX=-19.8796 StartY=-24.2445 StartZ=0 EndX=-22.477 EndY=-25.4404 EndZ=0
    g92: ArcOfEllipse CenterX=-19.9491 CenterY=-24.2102 CenterZ=0 NormalX=0 NormalY=0 NormalZ=1 MajorRadius=0.1 MinorRadius=0.0476557 AngleXU=-3.14159 StartAngle=3.14159 EndAngle=3.90978
    g93: ArcOfEllipse CenterX=-19.9491 CenterY=-24.2102 CenterZ=0 NormalX=0 NormalY=0 NormalZ=1 MajorRadius=0.1 MinorRadius=0.0476557 AngleXU=-3.14159 StartAngle=2.33898 EndAngle=3.14159
    g94: LineSegment StartX=-20.2246 StartY=-24.0058 StartZ=0 EndX=-19.8772 EndY=-24.1771 EndZ=0
    g95: LineSegment StartX=-22.0236 StartY=-29.5014 StartZ=0 EndX=-22.1529 EndY=-29.5609 EndZ=0
    g96: LineSegment StartX=-8.57842 StartY=-29.6723 StartZ=0 EndX=-8.85497 EndY=-29.5359 EndZ=0
    g97: LineSegment StartX=-8.18847 StartY=-25.8168 StartZ=0 EndX=-8.38051 EndY=-25.7221 EndZ=0
    g98: ArcOfEllipse CenterX=-10.7238 CenterY=-27.5155 CenterZ=0 NormalX=0 NormalY=0 NormalZ=1 MajorRadius=0.1 MinorRadius=0.0476557 AngleXU=-3.14159 StartAngle=0 EndAngle=0.768187
    g99: LineSegment StartX=-10.4483 StartY=-27.72 StartZ=0 EndX=-10.7957 EndY=-27.5486 EndZ=0
    g100: LineSegment StartX=-22.477 StartY=-25.7042 StartZ=0 EndX=-22.4844 EndY=-25.9089 EndZ=0
    g101: LineSegment StartX=-22.477 StartY=-25.7042 StartZ=0 EndX=-22.477 EndY=-25.4404 EndZ=0
    g102: LineSegment StartX=-22.28 StartY=-25.6135 StartZ=0 EndX=-22.477 EndY=-25.7042 EndZ=0
    g103: ArcOfEllipse CenterX=-19.9491 CenterY=-24.474 CenterZ=0 NormalX=0 NormalY=0 NormalZ=1 MajorRadius=0.1 MinorRadius=0.0476557 AngleXU=-3.14159 StartAngle=3.55586 EndAngle=3.90978
    g104: LineSegment StartX=-22.0236 StartY=-29.3715 StartZ=0 EndX=-22.0236 EndY=-30.4252 EndZ=0
    g105: ArcOfEllipse CenterX=-21.736 CenterY=-29.2391 CenterZ=0 NormalX=0 NormalY=0 NormalZ=1 MajorRadius=0.4 MinorRadius=0.252902 AngleXU=-2.02903 StartAngle=3.80411 EndAngle=5.37491
    g106: LineSegment StartX=-21.113 StartY=-30.374 StartZ=0 EndX=-21.113 EndY=-29.6149 EndZ=0
    g107: ArcOfEllipse CenterX=-21.0411 CenterY=-29.5818 CenterZ=0 NormalX=0 NormalY=0 NormalZ=1 MajorRadius=0.1 MinorRadius=0.0632255 AngleXU=1.11256 StartAngle=0.662517 EndAngle=2.23331
    g108: LineSegment StartX=-21.0411 StartY=-29.4939 StartZ=0 EndX=-21.0411 EndY=-29.2302 EndZ=0
    g109: ArcOfEllipse CenterX=-21.0411 CenterY=-29.5818 CenterZ=0 NormalX=0 NormalY=0 NormalZ=1 MajorRadius=0.4 MinorRadius=0.252902 AngleXU=-2.02903 StartAngle=3.80411 EndAngle=5.37491
    g110: LineSegment StartX=-21.3288 StartY=-29.7143 StartZ=0 EndX=-21.3288 EndY=-30.4488 EndZ=0
    g111: LineSegment StartX=-21.0411 StartY=-29.2302 StartZ=0 EndX=-21.736 EndY=-28.8874 EndZ=0
    g112: LineSegment StartX=-17.6389 StartY=-32.0876 StartZ=0 EndX=-17.6389 EndY=-31.3286 EndZ=0
    g113: ArcOfEllipse CenterX=-17.567 CenterY=-31.2955 CenterZ=0 NormalX=0 NormalY=0 NormalZ=1 MajorRadius=0.1 MinorRadius=0.0632255 AngleXU=1.11256 StartAngle=0.662517 EndAngle=2.23331
    g114: LineSegment StartX=-17.567 StartY=-31.2075 StartZ=0 EndX=-17.567 EndY=-30.9438 EndZ=0
    g115: ArcOfEllipse CenterX=-17.567 CenterY=-31.2955 CenterZ=0 NormalX=0 NormalY=0 NormalZ=1 MajorRadius=0.4 MinorRadius=0.252902 AngleXU=-2.02903 StartAngle=3.80411 EndAngle=5.37491
    g116: LineSegment StartX=-17.8546 StartY=-31.4279 StartZ=0 EndX=-17.8546 EndY=-32.1625 EndZ=0
    g117: LineSegment StartX=-18.5495 StartY=-31.0852 StartZ=0 EndX=-18.5495 EndY=-32.1388 EndZ=0
    g118: ArcOfEllipse CenterX=-18.2618 CenterY=-30.9527 CenterZ=0 NormalX=0 NormalY=0 NormalZ=1 MajorRadius=0.4 MinorRadius=0.252902 AngleXU=-2.02903 StartAngle=3.80411 EndAngle=5.37491
    g119: LineSegment StartX=-18.2618 StartY=-30.6011 StartZ=0 EndX=-17.567 EndY=-30.9438 EndZ=0
    g120: ArcOfEllipse CenterX=-10.7272 CenterY=-20.4588 CenterZ=0 NormalX=0 NormalY=0 NormalZ=1 MajorRadius=1.25 MinorRadius=0.790319 AngleXU=-2.02903 StartAngle=2.69057 EndAngle=3.14159
    g121: ArcOfEllipse CenterX=-10.7272 CenterY=-20.4588 CenterZ=0 NormalX=0 NormalY=0 NormalZ=1 MajorRadius=1.25 MinorRadius=0.790319 AngleXU=-2.02903 StartAngle=3.14159 EndAngle=5.67781
    g122: ArcOfEllipse CenterX=-10.7272 CenterY=-20.4588 CenterZ=0 NormalX=0 NormalY=0 NormalZ=1 MajorRadius=1.125 MinorRadius=0.711287 AngleXU=1.11256 StartAngle=-9e-16 EndAngle=2.72298
    g123: ArcOfEllipse CenterX=-8.53843 CenterY=-21.5384 CenterZ=0 NormalX=0 NormalY=0 NormalZ=1 MajorRadius=1.25 MinorRadius=0.790319 AngleXU=-2.02903 StartAngle=3.14159 EndAngle=6.28319
    g124: BSplineCurve PolesCount=87 KnotsCount=18 Degree=6 IsPeriodic=0
    g125: ArcOfEllipse CenterX=-44.5743 CenterY=-11.009 CenterZ=0 NormalX=0 NormalY=0 NormalZ=1 MajorRadius=2.1 MinorRadius=1.00077 AngleXU=0 StartAngle=3.14159 EndAngle=4.89489
    g126: LineSegment StartX=-44.1932 StartY=-10.6745 StartZ=0 EndX=-44.1932 EndY=-11.9932 EndZ=0
    g127: ArcOfEllipse CenterX=-44.5743 CenterY=-9.69033 CenterZ=0 NormalX=0 NormalY=0 NormalZ=1 MajorRadius=2.1 MinorRadius=1.00077 AngleXU=0 StartAngle=2.92467 EndAngle=3.14159
    g128: ArcOfEllipse CenterX=-44.5743 CenterY=-9.69033 CenterZ=0 NormalX=0 NormalY=0 NormalZ=1 MajorRadius=2.1 MinorRadius=1.00077 AngleXU=0 StartAngle=3.14159 EndAngle=4.89489
    g129: LineSegment StartX=-46.6251 StartY=-9.47494 StartZ=0 EndX=-44.9554 EndY=-8.70618 EndZ=0
    g130: LineSegment StartX=-44.1932 StartY=-11.9932 StartZ=0 EndX=-42.5235 EndY=-11.2244 EndZ=0
    g131: LineSegment StartX=-42.5235 StartY=-9.90572 StartZ=0 EndX=-42.5235 EndY=-11.2244 EndZ=0
    g132: LineSegment StartX=-44.1932 StartY=-10.6745 StartZ=0 EndX=-42.5235 EndY=-9.90572 EndZ=0
    g133: ArcOfEllipse CenterX=-44.5743 CenterY=-9.69033 CenterZ=0 NormalX=0 NormalY=0 NormalZ=1 MajorRadius=2.1 MinorRadius=1.00077 AngleXU=0 StartAngle=6.06626 EndAngle=6.28319
    g134: ArcOfEllipse CenterX=-44.5743 CenterY=-9.69033 CenterZ=0 NormalX=0 NormalY=0 NormalZ=1 MajorRadius=2.1 MinorRadius=1.00077 AngleXU=0 StartAngle=9e-16 EndAngle=1.7533
    g135: ArcOfEllipse CenterX=-45.4876 CenterY=-10.1109 CenterZ=0 NormalX=0 NormalY=0 NormalZ=1 MajorRadius=0.25 MinorRadius=0.119139 AngleXU=-3.14159 StartAngle=0 EndAngle=3.14159
    g136: ArcOfEllipse CenterX=-43.661 CenterY=-9.2698 CenterZ=0 NormalX=0 NormalY=0 NormalZ=1 MajorRadius=0.25 MinorRadius=0.119139 AngleXU=-3.14159 StartAngle=0 EndAngle=3.14159
    g137: ArcOfEllipse CenterX=-44.5743 CenterY=-11.009 CenterZ=0 NormalX=0 NormalY=0 NormalZ=1 MajorRadius=2.1 MinorRadius=1.00077 AngleXU=0 StartAngle=6.06626 EndAngle=6.28319
    g138: ArcOfEllipse CenterX=-45.4876 CenterY=-10.0229 CenterZ=0 NormalX=0 NormalY=0 NormalZ=1 MajorRadius=0.25 MinorRadius=0.119139 AngleXU=0 StartAngle=0.768187 EndAngle=3.14159
    g139: ArcOfEllipse CenterX=-45.4876 CenterY=-10.0229 CenterZ=0 NormalX=0 NormalY=0 NormalZ=1 MajorRadius=0.25 MinorRadius=0.119139 AngleXU=0 StartAngle=3.14159 EndAngle=6.28319
    g140: ArcOfEllipse CenterX=-45.4876 CenterY=-10.0229 CenterZ=0 NormalX=0 NormalY=0 NormalZ=1 MajorRadius=0.25 MinorRadius=0.119139 AngleXU=0 StartAngle=0 EndAngle=0.768187
    g141: ArcOfEllipse CenterX=-43.661 CenterY=-9.18188 CenterZ=0 NormalX=0 NormalY=0 NormalZ=1 MajorRadius=0.25 MinorRadius=0.119139 AngleXU=0 StartAngle=0.768187 EndAngle=3.14159
    g142: ArcOfEllipse CenterX=-43.661 CenterY=-9.18188 CenterZ=0 NormalX=0 NormalY=0 NormalZ=1 MajorRadius=0.25 MinorRadius=0.119139 AngleXU=0 StartAngle=3.14159 EndAngle=6.28319
    g143: ArcOfEllipse CenterX=-43.661 CenterY=-9.18188 CenterZ=0 NormalX=0 NormalY=0 NormalZ=1 MajorRadius=0.25 MinorRadius=0.119139 AngleXU=0 StartAngle=0 EndAngle=0.768187
    g144: LineSegment StartX=-44.8897 StartY=-8.77024 StartZ=0 EndX=-44.9592 EndY=-8.73597 EndZ=0
    g145: LineSegment StartX=-44.9592 StartY=-8.73597 StartZ=0 EndX=-46.4238 EndY=-9.41031 EndZ=0
    g146: LineSegment StartX=-46.4238 StartY=-9.45426 StartZ=0 EndX=-46.4238 EndY=-9.41031 EndZ=0
    g147: LineSegment StartX=-46.4238 StartY=-9.41031 StartZ=0 EndX=-46.3543 EndY=-9.44458 EndZ=0
    g148: LineSegment StartX=-46.3543 StartY=-9.48854 StartZ=0 EndX=-46.3543 EndY=-9.44458 EndZ=0
    g149: LineSegment StartX=-46.4238 StartY=-9.45426 StartZ=0 EndX=-46.3543 EndY=-9.48854 EndZ=0
    g150: LineSegment StartX=-46.3543 StartY=-9.44458 StartZ=0 EndX=-44.9616 EndY=-8.80335 EndZ=0
    g151: LineSegment StartX=-44.9616 StartY=-8.84731 StartZ=0 EndX=-44.9616 EndY=-8.80335 EndZ=0
    g152: LineSegment StartX=-46.3543 StartY=-9.48854 StartZ=0 EndX=-44.9616 EndY=-8.84731 EndZ=0
    g153: LineSegment StartX=-44.6779 StartY=-8.9433 StartZ=0 EndX=-44.9616 EndY=-8.80335 EndZ=0
    g154: LineSegment StartX=-44.724 StartY=-8.96452 StartZ=0 EndX=-44.9616 EndY=-8.84731 EndZ=0
    g155: LineSegment StartX=-44.6779 StartY=-8.9433 StartZ=0 EndX=-45.7661 EndY=-9.44435 EndZ=0
    g156: LineSegment StartX=-45.7661 StartY=-9.48831 StartZ=0 EndX=-45.7661 EndY=-9.44435 EndZ=0
    g157: LineSegment StartX=-45.7661 StartY=-9.44435 StartZ=0 EndX=-45.6967 EndY=-9.47862 EndZ=0
    g158: LineSegment StartX=-45.7661 StartY=-9.48831 StartZ=0 EndX=-45.6967 EndY=-9.52258 EndZ=0
    g159: LineSegment StartX=-45.6967 StartY=-9.47862 StartZ=0 EndX=-45.3434 EndY=-9.65284 EndZ=0
    g160: LineSegment StartX=-45.3434 StartY=-9.6968 StartZ=0 EndX=-45.3434 EndY=-9.65284 EndZ=0
    g161: LineSegment StartX=-45.6967 StartY=-9.52258 StartZ=0 EndX=-45.3434 EndY=-9.6968 EndZ=0
    g162: LineSegment StartX=-45.3434 StartY=-9.65284 StartZ=0 EndX=-45.2715 EndY=-9.61973 EndZ=0
    g163: LineSegment StartX=-45.3434 StartY=-9.6968 StartZ=0 EndX=-45.2715 EndY=-9.66368 EndZ=0
    g164: LineSegment StartX=-44.514 StartY=-9.3149 StartZ=0 EndX=-44.514 EndY=-9.27094 EndZ=0
    g165: LineSegment StartX=-44.514 StartY=-9.27094 StartZ=0 EndX=-45.2715 EndY=-9.61973 EndZ=0
    g166: LineSegment StartX=-44.514 StartY=-9.3149 StartZ=0 EndX=-45.2715 EndY=-9.66368 EndZ=0
    g167: LineSegment StartX=-44.514 StartY=-9.27094 StartZ=0 EndX=-44.2303 EndY=-9.41089 EndZ=0
    g168: LineSegment StartX=-44.514 StartY=-9.3149 StartZ=0 EndX=-44.2764 EndY=-9.43211 EndZ=0
    g169: LineSegment StartX=-44.2303 StartY=-9.41089 StartZ=0 EndX=-45.0597 EndY=-9.79279 EndZ=0
    g170: LineSegment StartX=-45.0597 StartY=-9.83674 StartZ=0 EndX=-45.0597 EndY=-9.79279 EndZ=0
    g171: LineSegment StartX=-45.0597 StartY=-9.79279 StartZ=0 EndX=-44.9902 EndY=-9.82706 EndZ=0
    g172: LineSegment StartX=-45.0597 StartY=-9.83674 StartZ=0 EndX=-44.9902 EndY=-9.87102 EndZ=0
    g173: LineSegment StartX=-44.9902 StartY=-9.82706 StartZ=0 EndX=-44.637 EndY=-10.0013 EndZ=0
    g174: LineSegment StartX=-44.637 StartY=-10.0452 StartZ=0 EndX=-44.637 EndY=-10.0013 EndZ=0
    g175: LineSegment StartX=-44.9902 StartY=-9.87102 StartZ=0 EndX=-44.637 EndY=-10.0452 EndZ=0
    g176: LineSegment StartX=-44.637 StartY=-10.0013 StartZ=0 EndX=-44.5651 EndY=-9.96817 EndZ=0
    g177: LineSegment StartX=-44.637 StartY=-10.0452 StartZ=0 EndX=-44.5651 EndY=-10.0121 EndZ=0
    g178: LineSegment StartX=-43.8076 StartY=-9.66334 StartZ=0 EndX=-43.8076 EndY=-9.61938 EndZ=0
    g179: LineSegment StartX=-43.8076 StartY=-9.61938 StartZ=0 EndX=-44.5651 EndY=-9.96817 EndZ=0
    g180: LineSegment StartX=-43.8076 StartY=-9.66334 StartZ=0 EndX=-44.5651 EndY=-10.0121 EndZ=0
    g181: LineSegment StartX=-43.5239 StartY=-9.75933 StartZ=0 EndX=-43.8076 EndY=-9.61938 EndZ=0
    g182: LineSegment StartX=-43.57 StartY=-9.78055 StartZ=0 EndX=-43.8076 EndY=-9.66334 EndZ=0
    g183: LineSegment StartX=-43.5239 StartY=-9.75933 StartZ=0 EndX=-44.6121 EndY=-10.2604 EndZ=0
    g184: LineSegment StartX=-44.6121 StartY=-10.3043 StartZ=0 EndX=-44.6121 EndY=-10.2604 EndZ=0
    g185: LineSegment StartX=-44.6121 StartY=-10.2604 StartZ=0 EndX=-44.5426 EndY=-10.2946 EndZ=0
    g186: LineSegment StartX=-44.6121 StartY=-10.3043 StartZ=0 EndX=-44.5426 EndY=-10.3386 EndZ=0
    g187: LineSegment StartX=-44.5426 StartY=-10.2946 StartZ=0 EndX=-44.1894 EndY=-10.4689 EndZ=0
    g188: LineSegment StartX=-44.1894 StartY=-10.5128 StartZ=0 EndX=-44.1894 EndY=-10.4689 EndZ=0
    g189: LineSegment StartX=-44.5426 StartY=-10.3386 StartZ=0 EndX=-44.1894 EndY=-10.5128 EndZ=0
    g190: LineSegment StartX=-44.1894 StartY=-10.4689 StartZ=0 EndX=-44.1175 EndY=-10.4358 EndZ=0
    g191: LineSegment StartX=-44.1894 StartY=-10.5128 StartZ=0 EndX=-44.1175 EndY=-10.4797 EndZ=0
    g192: LineSegment StartX=-42.7248 StartY=-9.83848 StartZ=0 EndX=-42.7248 EndY=-9.79453 EndZ=0
    g193: LineSegment StartX=-42.7248 StartY=-9.79453 StartZ=0 EndX=-44.1175 EndY=-10.4358 EndZ=0
    g194: LineSegment StartX=-42.7248 StartY=-9.83848 StartZ=0 EndX=-44.1175 EndY=-10.4797 EndZ=0
    g195: LineSegment StartX=-42.7943 StartY=-9.76025 StartZ=0 EndX=-42.7248 EndY=-9.79453 EndZ=0
    g196: LineSegment StartX=-44.187 StartY=-10.4015 StartZ=0 EndX=-42.7943 EndY=-9.76025 EndZ=0
    g197: LineSegment StartX=-44.187 StartY=-10.4015 StartZ=0 EndX=-44.4707 EndY=-10.2615 EndZ=0
    g198: LineSegment StartX=-44.4707 StartY=-10.2615 StartZ=0 EndX=-43.4544 EndY=-9.7936 EndZ=0
    g199: LineSegment StartX=-44.4246 StartY=-10.2843 StartZ=0 EndX=-43.4544 EndY=-9.83756 EndZ=0
    g200: LineSegment StartX=-43.3825 StartY=-9.80444 StartZ=0 EndX=-43.3825 EndY=-9.76049 EndZ=0
    g201: LineSegment StartX=-43.3825 StartY=-9.76049 StartZ=0 EndX=-43.4544 EndY=-9.7936 EndZ=0
    g202: LineSegment StartX=-43.3825 StartY=-9.80444 StartZ=0 EndX=-43.4544 EndY=-9.83756 EndZ=0
    g203: LineSegment StartX=-43.7357 StartY=-9.58627 StartZ=0 EndX=-43.3825 EndY=-9.76049 EndZ=0
    g204: LineSegment StartX=-43.8052 StartY=-9.55199 StartZ=0 EndX=-43.7357 EndY=-9.58627 EndZ=0
    g205: LineSegment StartX=-44.6346 StartY=-9.93389 StartZ=0 EndX=-43.8052 EndY=-9.55199 EndZ=0
    g206: LineSegment StartX=-44.6346 StartY=-9.93389 StartZ=0 EndX=-44.9183 EndY=-9.79395 EndZ=0
    g207: LineSegment StartX=-44.9183 StartY=-9.79395 StartZ=0 EndX=-44.1608 EndY=-9.44516 EndZ=0
    g208: LineSegment StartX=-44.8722 StartY=-9.81668 StartZ=0 EndX=-44.1608 EndY=-9.48912 EndZ=0
    g209: LineSegment StartX=-44.0889 StartY=-9.456 StartZ=0 EndX=-44.0889 EndY=-9.41205 EndZ=0
    g210: LineSegment StartX=-44.0889 StartY=-9.41205 StartZ=0 EndX=-44.1608 EndY=-9.44516 EndZ=0
    g211: LineSegment StartX=-44.0889 StartY=-9.456 StartZ=0 EndX=-44.1608 EndY=-9.48912 EndZ=0
    g212: LineSegment StartX=-44.4421 StartY=-9.23783 StartZ=0 EndX=-44.0889 EndY=-9.41205 EndZ=0
    g213: LineSegment StartX=-44.5116 StartY=-9.20355 StartZ=0 EndX=-44.4421 EndY=-9.23783 EndZ=0
    g214: LineSegment StartX=-45.341 StartY=-9.58546 StartZ=0 EndX=-44.5116 EndY=-9.20355 EndZ=0
    g215: LineSegment StartX=-45.341 StartY=-9.58546 StartZ=0 EndX=-45.6247 EndY=-9.44551 EndZ=0
    g216: LineSegment StartX=-45.6247 StartY=-9.44551 StartZ=0 EndX=-44.6084 EndY=-8.97757 EndZ=0
    g217: LineSegment StartX=-45.5786 StartY=-9.46824 StartZ=0 EndX=-44.6084 EndY=-9.02153 EndZ=0
    g218: LineSegment StartX=-44.5365 StartY=-8.98841 StartZ=0 EndX=-44.5365 EndY=-8.94446 EndZ=0
    g219: LineSegment StartX=-44.5365 StartY=-8.94446 StartZ=0 EndX=-44.6084 EndY=-8.97757 EndZ=0
    g220: LineSegment StartX=-44.5365 StartY=-8.98841 StartZ=0 EndX=-44.6084 EndY=-9.02153 EndZ=0
    g221: LineSegment StartX=-44.8897 StartY=-8.77024 StartZ=0 EndX=-44.5365 EndY=-8.94446 EndZ=0
    g222: ArcOfEllipse CenterX=-26.3772 CenterY=-20.2262 CenterZ=0 NormalX=0 NormalY=0 NormalZ=1 MajorRadius=3.21 MinorRadius=1.52975 AngleXU=0 StartAngle=3.14159 EndAngle=6.28319
    g223: ArcOfEllipse CenterX=-26.3772 CenterY=-18.6437 CenterZ=0 NormalX=0 NormalY=0 NormalZ=1 MajorRadius=3.21 MinorRadius=1.52975 AngleXU=0 StartAngle=1.4772 EndAngle=3.14159
    g224: ArcOfEllipse CenterX=-26.3772 CenterY=-18.6437 CenterZ=0 NormalX=0 NormalY=0 NormalZ=1 MajorRadius=3.21 MinorRadius=1.52975 AngleXU=0 StartAngle=3.14159 EndAngle=6.28319
    g225: ArcOfEllipse CenterX=-26.3772 CenterY=-18.6437 CenterZ=0 NormalX=0 NormalY=0 NormalZ=1 MajorRadius=3.21 MinorRadius=1.52975 AngleXU=0 StartAngle=0 EndAngle=0.0591766
    g226: LineSegment StartX=-24.1027 StartY=-18.5242 StartZ=0 EndX=-26.0482 EndY=-17.5646 EndZ=0
    g227: LineSegment StartX=-25.5977 StartY=-17.7868 StartZ=0 EndX=-25.5977 EndY=-17.3571 EndZ=0
    g228: LineSegment StartX=-26.0482 StartY=-17.5646 StartZ=0 EndX=-25.5977 EndY=-17.3571 EndZ=0
    g229: LineSegment StartX=-25.5977 StartY=-17.3571 StartZ=0 EndX=-26.0771 EndY=-17.1207 EndZ=0
    g230: LineSegment StartX=-23.1728 StartY=-18.5532 StartZ=0 EndX=-23.6522 EndY=-18.3168 EndZ=0
    g231: LineSegment StartX=-23.6522 StartY=-18.3168 StartZ=0 EndX=-24.1027 EndY=-18.5242 EndZ=0
    g232: LineSegment StartX=-27.6504 StartY=-17.6727 StartZ=0 EndX=-27.6504 EndY=-18.4117 EndZ=0
    g233: LineSegment StartX=-28.3696 StartY=-18.0039 StartZ=0 EndX=-27.6504 EndY=-17.6727 EndZ=0
    g234: LineSegment StartX=-24.3847 StartY=-19.2836 StartZ=0 EndX=-25.1039 EndY=-19.6147 EndZ=0
    g235: BSplineCurve PolesCount=3 KnotsCount=2 Degree=2 IsPeriodic=0
    g236: LineSegment StartX=-27.6504 StartY=-17.6727 StartZ=0 EndX=-27.0736 EndY=-17.9573 EndZ=0
    g237: LineSegment StartX=-24.9615 StartY=-18.9991 StartZ=0 EndX=-24.3847 EndY=-19.2836 EndZ=0
    g238: BSplineCurve PolesCount=3 KnotsCount=2 Degree=2 IsPeriodic=0
    g239: LineSegment StartX=-25.6702 StartY=-18.8948 StartZ=0 EndX=-25.6702 EndY=-19.3354 EndZ=0
    g240: LineSegment StartX=-26.365 StartY=-19.231 StartZ=0 EndX=-26.365 EndY=-18.5521 EndZ=0
    g241: BSplineCurve PolesCount=3 KnotsCount=2 Degree=2 IsPeriodic=0
    g242: LineSegment StartX=-25.1039 StartY=-19.6147 StartZ=0 EndX=-25.6807 EndY=-19.3302 EndZ=0
    g243: LineSegment StartX=-27.7928 StartY=-18.2884 StartZ=0 EndX=-28.3696 EndY=-18.0039 EndZ=0
    g244: BSplineCurve PolesCount=3 KnotsCount=2 Degree=2 IsPeriodic=0
    g245: LineSegment StartX=-27.0842 StartY=-18.8832 StartZ=0 EndX=-27.0842 EndY=-19.3146 EndZ=0
    g246: LineSegment StartX=-25.7148 StartY=-19.3261 StartZ=0 EndX=-25.6702 EndY=-19.3056 EndZ=0
    g247: BSplineCurve PolesCount=3 KnotsCount=2 Degree=2 IsPeriodic=0
    g248: LineSegment StartX=-24.8791 StartY=-18.2853 StartZ=0 EndX=-24.9367 EndY=-18.3118 EndZ=0
    g249: BSplineCurve PolesCount=3 KnotsCount=2 Degree=2 IsPeriodic=0
    g250: LineSegment StartX=-25.5739 StartY=-17.9425 StartZ=0 EndX=-25.5739 EndY=-18.823 EndZ=0
    g251: LineSegment StartX=-25.6315 StartY=-17.9691 StartZ=0 EndX=-25.5739 EndY=-17.9425 EndZ=0
    g252: LineSegment StartX=-25.5739 StartY=-17.9425 StartZ=0 EndX=-24.8791 EndY=-18.2853 EndZ=0
    g253: LineSegment StartX=-27.1804 StartY=-19.3449 StartZ=0 EndX=-27.8752 EndY=-19.0022 EndZ=0
    g254: BSplineCurve PolesCount=3 KnotsCount=2 Degree=2 IsPeriodic=0
    g255: LineSegment StartX=-27.8752 StartY=-19.0022 StartZ=0 EndX=-27.8176 EndY=-18.9756 EndZ=0
    g256: BSplineCurve PolesCount=3 KnotsCount=2 Degree=2 IsPeriodic=0
    g257: LineSegment StartX=-27.1228 StartY=-19.3183 StartZ=0 EndX=-27.1804 EndY=-19.3449 EndZ=0
    g258: ArcOfEllipse CenterX=-26.3772 CenterY=-18.6437 CenterZ=0 NormalX=0 NormalY=0 NormalZ=1 MajorRadius=1.6 MinorRadius=0.762492 AngleXU=-3.14159 StartAngle=1.08601 EndAngle=2.02116
    g259: ArcOfEllipse CenterX=-26.3772 CenterY=-18.6437 CenterZ=0 NormalX=0 NormalY=0 NormalZ=1 MajorRadius=1.6 MinorRadius=0.762492 AngleXU=-3.14159 StartAngle=5.7984 EndAngle=6.73355
    g260: ArcOfEllipse CenterX=-26.3772 CenterY=-18.6437 CenterZ=0 NormalX=0 NormalY=0 NormalZ=1 MajorRadius=1.6 MinorRadius=0.762492 AngleXU=-3.14159 StartAngle=4.2276 EndAngle=5.16275
    g261: ArcOfEllipse CenterX=-26.3772 CenterY=-18.6437 CenterZ=0 NormalX=0 NormalY=0 NormalZ=1 MajorRadius=1.6 MinorRadius=0.762492 AngleXU=-3.14159 StartAngle=2.65681 EndAngle=3.59196
    g262: LineSegment StartX=-28.604 StartY=-26.2173 StartZ=0 EndX=-28.673 EndY=-26.3756 EndZ=0
    g263: LineSegment StartX=-28.604 StartY=-26.0415 StartZ=0 EndX=-28.604 EndY=-26.2173 EndZ=0
    g264: LineSegment StartX=-28.1262 StartY=-26.453 StartZ=0 EndX=-28.604 EndY=-26.2173 EndZ=0
    g265: LineSegment StartX=-28.0482 StartY=-26.3157 StartZ=0 EndX=-28.0482 EndY=-26.4372 EndZ=0
    g266: LineSegment StartX=-27.222 StartY=-26.4489 StartZ=0 EndX=-27.5097 EndY=-26.5813 EndZ=0
    g267: LineSegment StartX=-27.5097 StartY=-26.5813 StartZ=0 EndX=-28.0482 EndY=-26.3157 EndZ=0
    g268: LineSegment StartX=-23.2599 StartY=-25.4995 StartZ=0 EndX=-23.2599 EndY=-25.454 EndZ=0
    g269: LineSegment StartX=-23.1536 StartY=-25.6455 StartZ=0 EndX=-23.2599 EndY=-25.4995 EndZ=0
    g270: LineSegment StartX=-23.0824 StartY=-25.5871 StartZ=0 EndX=-23.2599 EndY=-25.4995 EndZ=0
    g271: LineSegment StartX=-23.0808 StartY=-25.5423 StartZ=0 EndX=-24.477 EndY=-24.8536 EndZ=0
    g272: LineSegment StartX=-25.415 StartY=-24.391 StartZ=0 EndX=-25.1273 EndY=-24.2585 EndZ=0
    g273: LineSegment StartX=-25.6827 StartY=-24.2589 StartZ=0 EndX=-25.415 EndY=-24.391 EndZ=0
    g274: ArcOfEllipse CenterX=-22.3407 CenterY=-24.0206 CenterZ=0 NormalX=0 NormalY=0 NormalZ=1 MajorRadius=0.7 MinorRadius=0.442579 AngleXU=1.11256 StartAngle=0.662517 EndAngle=2.23331
    g275: LineSegment StartX=-22.8441 StartY=-25.2119 StartZ=0 EndX=-22.8441 EndY=-24.2524 EndZ=0
    g276: LineSegment StartX=-24.477 StartY=-24.8536 StartZ=0 EndX=-24.477 EndY=-23.7401 EndZ=0
    g277: ArcOfEllipse CenterX=-22.1969 CenterY=-24.1302 CenterZ=0 NormalX=0 NormalY=0 NormalZ=1 MajorRadius=0.5 MinorRadius=0.316128 AngleXU=-2.02903 StartAngle=3.80411 EndAngle=5.37491
    g278: LineSegment StartX=-25.415 StartY=-24.391 StartZ=0 EndX=-25.415 EndY=-24.1705 EndZ=0
    g279: ArcOfEllipse CenterX=-21.6936 CenterY=-21.5248 CenterZ=0 NormalX=0 NormalY=0 NormalZ=1 MajorRadius=0.4 MinorRadius=0.252902 AngleXU=1.11256 StartAngle=9e-16 EndAngle=0.116077
    g280: ArcOfEllipse CenterX=-21.6936 CenterY=-21.5248 CenterZ=0 NormalX=0 NormalY=0 NormalZ=1 MajorRadius=0.4 MinorRadius=0.252902 AngleXU=1.11256 StartAngle=5.37491 EndAngle=6.28319
    g281: LineSegment StartX=-21.4059 StartY=-22.9748 StartZ=0 EndX=-21.4059 EndY=-21.3924 EndZ=0
    g282: LineSegment StartX=-21.6936 StartY=-23.1073 StartZ=0 EndX=-22.3738 EndY=-22.7717 EndZ=0
    g283: LineSegment StartX=-21.6936 StartY=-23.1073 StartZ=0 EndX=-21.6936 EndY=-22.4585 EndZ=0
    g284: LineSegment StartX=-21.5441 StartY=-22.3897 StartZ=0 EndX=-25.3557 EndY=-24.1447 EndZ=0
    g285: ArcOfEllipse CenterX=-26.3979 CenterY=-23.6306 CenterZ=0 NormalX=0 NormalY=0 NormalZ=1 MajorRadius=1.5 MinorRadius=0.714836 AngleXU=0 StartAngle=3.90978 EndAngle=5.48058
    g286: LineSegment StartX=-27.4767 StartY=-24.1273 StartZ=0 EndX=-29.8947 EndY=-22.9346 EndZ=0
    g287: ArcOfEllipse CenterX=-28.8159 CenterY=-22.4379 CenterZ=0 NormalX=0 NormalY=0 NormalZ=1 MajorRadius=1.5 MinorRadius=0.714836 AngleXU=0 StartAngle=3.14159 EndAngle=3.90978
    g288: LineSegment StartX=-29.5872 StartY=-19.733 StartZ=0 EndX=-29.8582 EndY=-19.8578 EndZ=0
    g289: ArcOfEllipse CenterX=-28.8159 CenterY=-20.3719 CenterZ=0 NormalX=0 NormalY=0 NormalZ=1 MajorRadius=1.5 MinorRadius=0.714836 AngleXU=0 StartAngle=2.33898 EndAngle=3.14159
    g290: ArcOfEllipse CenterX=-28.8159 CenterY=-20.3719 CenterZ=0 NormalX=0 NormalY=0 NormalZ=1 MajorRadius=1.5 MinorRadius=0.714836 AngleXU=0 StartAngle=3.14159 EndAngle=3.90978
    g291: LineSegment StartX=-28.6857 StartY=-21.4649 StartZ=0 EndX=-27.4767 EndY=-22.0613 EndZ=0
    g292: LineSegment StartX=-29.8947 StartY=-20.8686 StartZ=0 EndX=-28.6857 EndY=-21.4649 EndZ=0
    g293: ArcOfEllipse CenterX=-26.3979 CenterY=-21.5646 CenterZ=0 NormalX=0 NormalY=0 NormalZ=1 MajorRadius=1.5 MinorRadius=0.714836 AngleXU=0 StartAngle=3.90978 EndAngle=5.48058
    g294: LineSegment StartX=-21.5441 StartY=-22.3897 StartZ=0 EndX=-21.5441 EndY=-20.3237 EndZ=0
    g295: LineSegment StartX=-25.3557 StartY=-22.0787 StartZ=0 EndX=-21.5441 EndY=-20.3237 EndZ=0
    g296: LineSegment StartX=-21.5441 StartY=-20.3237 StartZ=0 EndX=-23.1672 EndY=-19.5231 EndZ=0
    g297: ArcOfEllipse CenterX=-26.3772 CenterY=-20.402 CenterZ=0 NormalX=0 NormalY=0 NormalZ=1 MajorRadius=3.21 MinorRadius=1.52975 AngleXU=-3.14159 StartAngle=0 EndAngle=0.768187
    g298: ArcOfEllipse CenterX=-26.3772 CenterY=-20.402 CenterZ=0 NormalX=0 NormalY=0 NormalZ=1 MajorRadius=3.21 MinorRadius=1.52975 AngleXU=-3.14159 StartAngle=0.768187 EndAngle=3.14159
    g299: ArcOfEllipse CenterX=-26.3772 CenterY=-20.2262 CenterZ=0 NormalX=0 NormalY=0 NormalZ=1 MajorRadius=3.21 MinorRadius=1.52975 AngleXU=0 StartAngle=3.14159 EndAngle=6.28319
    g300: BSplineCurve PolesCount=18 KnotsCount=9 Degree=3 IsPeriodic=0
    g301: LineSegment StartX=-28.743 StartY=-23.6872 StartZ=0 EndX=-27.9092 EndY=-24.0985 EndZ=0
    g302: LineSegment StartX=-28.743 StartY=-25.4455 StartZ=0 EndX=-28.743 EndY=-23.6872 EndZ=0
    g303: BSplineCurve PolesCount=18 KnotsCount=9 Degree=3 IsPeriodic=0
    g304: LineSegment StartX=-27.9092 StartY=-24.0985 StartZ=0 EndX=-27.9092 EndY=-25.8568 EndZ=0
    g305: LineSegment StartX=-29.1425 StartY=-23.3056 StartZ=0 EndX=-29.1425 EndY=-25.7759 EndZ=0
    g306: LineSegment StartX=-27.9092 StartY=-25.8568 StartZ=0 EndX=-28.743 EndY=-25.4455 EndZ=0
    g307: LineSegment StartX=-27.5097 StartY=-24.111 StartZ=0 EndX=-27.5097 EndY=-26.5813 EndZ=0
    g308: LineSegment StartX=-28.604 StartY=-26.0415 StartZ=0 EndX=-29.1425 EndY=-25.7759 EndZ=0
    g309: LineSegment StartX=-27.222 StartY=-24.2279 StartZ=0 EndX=-27.222 EndY=-26.4489 EndZ=0
    g310: LineSegment StartX=-25.1273 StartY=-24.0395 StartZ=0 EndX=-25.1273 EndY=-24.2585 EndZ=0
    g311: ArcOfEllipse CenterX=-21.6936 CenterY=-23.1073 CenterZ=0 NormalX=0 NormalY=0 NormalZ=1 MajorRadius=0.4 MinorRadius=0.252902 AngleXU=1.11256 StartAngle=3.80411 EndAngle=5.37491
    g312: LineSegment StartX=-22.1969 StartY=-23.6907 StartZ=0 EndX=-21.6936 EndY=-23.4589 EndZ=0
    g313: LineSegment StartX=-22.5565 StartY=-24.2958 StartZ=0 EndX=-22.5565 EndY=-25.0794 EndZ=0
    g314: LineSegment StartX=-22.3407 StartY=-23.4052 StartZ=0 EndX=-21.6936 EndY=-23.1073 EndZ=0
    g315: ArcOfEllipse CenterX=-41.2396 CenterY=-13.8798 CenterZ=0 NormalX=0 NormalY=0 NormalZ=1 MajorRadius=1.5 MinorRadius=0.948383 AngleXU=-2.02903 StartAngle=5.37491 EndAngle=5.87952
    g316: BSplineCurve PolesCount=30 KnotsCount=5 Degree=8 IsPeriodic=0
    g317: ArcOfEllipse CenterX=-41.2396 CenterY=-13.8798 CenterZ=0 NormalX=0 NormalY=0 NormalZ=1 MajorRadius=1.5 MinorRadius=0.948383 AngleXU=-2.02903 StartAngle=2.79465 EndAngle=3.48854
    g318: ArcOfEllipse CenterX=-41.2396 CenterY=-13.8798 CenterZ=0 NormalX=0 NormalY=0 NormalZ=1 MajorRadius=1.5 MinorRadius=0.948383 AngleXU=-2.02903 StartAngle=3.48854 EndAngle=5.37491
    g319: BSplineCurve PolesCount=44 KnotsCount=7 Degree=8 IsPeriodic=0
    g320: LineSegment StartX=-20.2089 StartY=-21.7778 StartZ=0 EndX=-20.2089 EndY=-22.7408 EndZ=0
    g321: LineSegment StartX=-21.4059 StartY=-21.7056 StartZ=0 EndX=-20.9815 EndY=-21.9149 EndZ=0
    g322: ArcOfEllipse CenterX=-21.4256 CenterY=-20.7837 CenterZ=0 NormalX=0 NormalY=0 NormalZ=1 MajorRadius=2.415 MinorRadius=1.15089 AngleXU=0 StartAngle=4.89734 EndAngle=6.28319
    g323: LineSegment StartX=-23.7828 StartY=-18.3769 StartZ=0 EndX=-23.7828 EndY=-16.3133 EndZ=0
    g324: LineSegment StartX=-23.7828 StartY=-16.3133 StartZ=0 EndX=-20.9815 EndY=-17.6951 EndZ=0
    g325: LineSegment StartX=-20.9815 StartY=-21.9149 StartZ=0 EndX=-20.9815 EndY=-17.6951 EndZ=0
    g326: ArcOfEllipse CenterX=-21.4256 CenterY=-16.5638 CenterZ=0 NormalX=0 NormalY=0 NormalZ=1 MajorRadius=2.415 MinorRadius=1.15089 AngleXU=0 StartAngle=4.89734 EndAngle=6.28319
    g327: ArcOfEllipse CenterX=-21.4256 CenterY=-16.5638 CenterZ=0 NormalX=0 NormalY=0 NormalZ=1 MajorRadius=2.415 MinorRadius=1.15089 AngleXU=0 StartAngle=0 EndAngle=2.92222
    g328: LineSegment StartX=-20.8466 StartY=-21.901 StartZ=0 EndX=-20.8466 EndY=-23.5966 EndZ=0
    g329: LineSegment StartX=-20.2398 StartY=-21.7863 StartZ=0 EndX=-20.2398 EndY=-23.5966 EndZ=0
    g330: LineSegment StartX=-20.5131 StartY=-21.8492 StartZ=0 EndX=-20.5131 EndY=-23.6697 EndZ=0
    g331: ArcOfEllipse CenterX=-40.4306 CenterY=-15.3073 CenterZ=0 NormalX=0 NormalY=0 NormalZ=1 MajorRadius=1.36 MinorRadius=0.830766 AngleXU=-1.1393 StartAngle=0 EndAngle=2.4957
    g332: ArcOfEllipse CenterX=-40.4306 CenterY=-15.3073 CenterZ=0 NormalX=0 NormalY=0 NormalZ=1 MajorRadius=1.36 MinorRadius=0.830766 AngleXU=-1.1393 StartAngle=6.16184 EndAngle=6.28319
    g333: ArcOfEllipse CenterX=-40.4306 CenterY=-15.3073 CenterZ=0 NormalX=0 NormalY=0 NormalZ=1 MajorRadius=1.36 MinorRadius=0.830766 AngleXU=-1.1393 StartAngle=3.14159 EndAngle=3.26293
    g334: ArcOfEllipse CenterX=-40.4306 CenterY=-15.3073 CenterZ=0 NormalX=0 NormalY=0 NormalZ=1 MajorRadius=1.36 MinorRadius=0.830766 AngleXU=-1.1393 StartAngle=2.4957 EndAngle=3.14159
    g335: ArcOfEllipse CenterX=-39.4957 CenterY=-14.8769 CenterZ=0 NormalX=0 NormalY=0 NormalZ=1 MajorRadius=1.36 MinorRadius=0.830766 AngleXU=-1.1393 StartAngle=0 EndAngle=2.4957
    g336: ArcOfEllipse CenterX=-39.4957 CenterY=-14.8769 CenterZ=0 NormalX=0 NormalY=0 NormalZ=1 MajorRadius=1.36 MinorRadius=0.830766 AngleXU=-1.1393 StartAngle=2.4957 EndAngle=3.14159
    g337: ArcOfEllipse CenterX=-40.4306 CenterY=-15.3073 CenterZ=0 NormalX=0 NormalY=0 NormalZ=1 MajorRadius=1.35 MinorRadius=0.824657 AngleXU=-1.1393 StartAngle=0 EndAngle=2.4957
    g338: ArcOfEllipse CenterX=-40.4306 CenterY=-15.3073 CenterZ=0 NormalX=0 NormalY=0 NormalZ=1 MajorRadius=1.35 MinorRadius=0.824657 AngleXU=-1.1393 StartAngle=2.4957 EndAngle=3.14159
    g339: ArcOfEllipse CenterX=-40.9916 CenterY=-15.5656 CenterZ=0 NormalX=0 NormalY=0 NormalZ=1 MajorRadius=1.35 MinorRadius=0.824657 AngleXU=-1.1393 StartAngle=0 EndAngle=2.4957
    g340: ArcOfEllipse CenterX=-40.9916 CenterY=-15.5656 CenterZ=0 NormalX=0 NormalY=0 NormalZ=1 MajorRadius=1.35 MinorRadius=0.824657 AngleXU=-1.1393 StartAngle=5.0132 EndAngle=6.28319
    g341: ArcOfEllipse CenterX=-40.9916 CenterY=-15.5656 CenterZ=0 NormalX=0 NormalY=0 NormalZ=1 MajorRadius=1.35 MinorRadius=0.824657 AngleXU=-1.1393 StartAngle=3.14159 EndAngle=4.41158
    g342: ArcOfEllipse CenterX=-40.9916 CenterY=-15.5656 CenterZ=0 NormalX=0 NormalY=0 NormalZ=1 MajorRadius=1.35 MinorRadius=0.824657 AngleXU=-1.1393 StartAngle=2.4957 EndAngle=3.14159
    g343: ArcOfEllipse CenterX=-37.2519 CenterY=-13.8437 CenterZ=0 NormalX=0 NormalY=0 NormalZ=1 MajorRadius=1.35 MinorRadius=0.824657 AngleXU=-1.1393 StartAngle=0 EndAngle=2.4957
    g344: ArcOfEllipse CenterX=-37.2519 CenterY=-13.8437 CenterZ=0 NormalX=0 NormalY=0 NormalZ=1 MajorRadius=1.35 MinorRadius=0.824657 AngleXU=-1.1393 StartAngle=2.4957 EndAngle=3.14159
    g345: ArcOfEllipse CenterX=-40.9916 CenterY=-15.5656 CenterZ=0 NormalX=0 NormalY=0 NormalZ=1 MajorRadius=0.4 MinorRadius=0.244343 AngleXU=-1.1393 StartAngle=0 EndAngle=3.14159
    g346: ArcOfEllipse CenterX=-39.9745 CenterY=-8.43307 CenterZ=0 NormalX=0 NormalY=0 NormalZ=1 MajorRadius=1.25 MinorRadius=0.790319 AngleXU=1.11256 StartAngle=0 EndAngle=2.23331
    g347: ArcOfEllipse CenterX=-39.9745 CenterY=-8.43307 CenterZ=0 NormalX=0 NormalY=0 NormalZ=1 MajorRadius=1.25 MinorRadius=0.790319 AngleXU=1.11256 StartAngle=2.23331 EndAngle=3.14159
    g348: BSplineCurve PolesCount=92 KnotsCount=19 Degree=6 IsPeriodic=0
    g349: ArcOfEllipse CenterX=-42.1632 CenterY=-7.35348 CenterZ=0 NormalX=0 NormalY=0 NormalZ=1 MajorRadius=1.125 MinorRadius=0.711287 AngleXU=-2.02903 StartAngle=5.37491 EndAngle=6.28319
    g350: ArcOfEllipse CenterX=-42.1632 CenterY=-7.35348 CenterZ=0 NormalX=0 NormalY=0 NormalZ=1 MajorRadius=1.125 MinorRadius=0.711287 AngleXU=-2.02903 StartAngle=3.14159 EndAngle=5.37491
    g351: ArcOfEllipse CenterX=-42.1632 CenterY=-7.35348 CenterZ=0 NormalX=0 NormalY=0 NormalZ=1 MajorRadius=1.25 MinorRadius=0.790319 AngleXU=1.11256 StartAngle=0 EndAngle=2.23331
    g352: ArcOfEllipse CenterX=-42.1632 CenterY=-7.35348 CenterZ=0 NormalX=0 NormalY=0 NormalZ=1 MajorRadius=1.25 MinorRadius=0.790319 AngleXU=1.11256 StartAngle=5.83216 EndAngle=6.28319
    g353: ArcOfEllipse CenterX=-42.1632 CenterY=-7.35348 CenterZ=0 NormalX=0 NormalY=0 NormalZ=1 MajorRadius=1.25 MinorRadius=0.790319 AngleXU=1.11256 StartAngle=3.14159 EndAngle=3.59262
    g354: ArcOfEllipse CenterX=-42.1632 CenterY=-7.35348 CenterZ=0 NormalX=0 NormalY=0 NormalZ=1 MajorRadius=1.25 MinorRadius=0.790319 AngleXU=1.11256 StartAngle=2.23331 EndAngle=3.14159
    g355: LineSegment StartX=-55.2873 StartY=-13.6316 StartZ=0 EndX=-55.2873 EndY=-12.827 EndZ=0
    g356: ArcOfEllipse CenterX=-55.2154 CenterY=-12.7939 CenterZ=0 NormalX=0 NormalY=0 NormalZ=1 MajorRadius=0.1 MinorRadius=0.0632255 AngleXU=1.11256 StartAngle=0.662517 EndAngle=2.23331
    g357: LineSegment StartX=-55.2154 StartY=-12.706 StartZ=0 EndX=-55.2154 EndY=-12.4423 EndZ=0
    g358: ArcOfEllipse CenterX=-55.2154 CenterY=-12.7939 CenterZ=0 NormalX=0 NormalY=0 NormalZ=1 MajorRadius=0.4 MinorRadius=0.252902 AngleXU=-2.02903 StartAngle=3.80411 EndAngle=5.37491
    g359: LineSegment StartX=-55.5031 StartY=-12.9264 StartZ=0 EndX=-55.5031 EndY=-13.6771 EndZ=0
    g360: LineSegment StartX=-56.1979 StartY=-12.5836 StartZ=0 EndX=-56.1979 EndY=-13.5804 EndZ=0
    g361: ArcOfEllipse CenterX=-55.9102 CenterY=-12.4512 CenterZ=0 NormalX=0 NormalY=0 NormalZ=1 MajorRadius=0.4 MinorRadius=0.252902 AngleXU=-2.02903 StartAngle=3.80411 EndAngle=5.37491
    g362: LineSegment StartX=-55.9102 StartY=-12.0995 StartZ=0 EndX=-55.2154 EndY=-12.4423 EndZ=0
    g363: ArcOfEllipse CenterX=-53.0822 CenterY=-10.0128 CenterZ=0 NormalX=0 NormalY=0 NormalZ=1 MajorRadius=0.8 MinorRadius=0.381246 AngleXU=0 StartAngle=3.14159 EndAngle=5.48058
    g364: ArcOfEllipse CenterX=-58.6409 CenterY=-7.27097 CenterZ=0 NormalX=0 NormalY=0 NormalZ=1 MajorRadius=0.8 MinorRadius=0.381246 AngleXU=0 StartAngle=3.14159 EndAngle=5.48058
    g365: ArcOfEllipse CenterX=-47.3289 CenterY=-7.36376 CenterZ=0 NormalX=0 NormalY=0 NormalZ=1 MajorRadius=0.8 MinorRadius=0.381246 AngleXU=0 StartAngle=3.14159 EndAngle=5.48058
    g366: ArcOfEllipse CenterX=-52.9849 CenterY=-7.4932 CenterZ=0 NormalX=0 NormalY=0 NormalZ=1 MajorRadius=3.7 MinorRadius=1.76326 AngleXU=0 StartAngle=2.8113 EndAngle=3.09171
    g367: ArcOfEllipse CenterX=-52.9849 CenterY=-7.31737 CenterZ=0 NormalX=0 NormalY=0 NormalZ=1 MajorRadius=3.7 MinorRadius=1.76326 AngleXU=0 StartAngle=2.8113 EndAngle=3.14159
    g368: ArcOfEllipse CenterX=-52.9849 CenterY=-7.31737 CenterZ=0 NormalX=0 NormalY=0 NormalZ=1 MajorRadius=3.7 MinorRadius=1.76326 AngleXU=0 StartAngle=3.14159 EndAngle=5.48058
    g369: ArcOfEllipse CenterX=-52.9849 CenterY=-7.4932 CenterZ=0 NormalX=0 NormalY=0 NormalZ=1 MajorRadius=3.7 MinorRadius=1.76326 AngleXU=0 StartAngle=0.0498796 EndAngle=0.330297
    g370: ArcOfEllipse CenterX=-52.9849 CenterY=-7.31737 CenterZ=0 NormalX=0 NormalY=0 NormalZ=1 MajorRadius=3.7 MinorRadius=1.76326 AngleXU=0 StartAngle=5.48058 EndAngle=6.28319
    g371: ArcOfEllipse CenterX=-52.9849 CenterY=-7.31737 CenterZ=0 NormalX=0 NormalY=0 NormalZ=1 MajorRadius=3.7 MinorRadius=1.76326 AngleXU=0 StartAngle=0 EndAngle=0.330297
    g372: ArcOfEllipse CenterX=-47.3289 CenterY=-7.36376 CenterZ=0 NormalX=0 NormalY=0 NormalZ=1 MajorRadius=0.8 MinorRadius=0.381246 AngleXU=0 StartAngle=5.48058 EndAngle=6.28319
    g373: ArcOfEllipse CenterX=-58.6409 CenterY=-7.27097 CenterZ=0 NormalX=0 NormalY=0 NormalZ=1 MajorRadius=0.8 MinorRadius=0.381246 AngleXU=0 StartAngle=5.48058 EndAngle=6.28319
    g374: ArcOfEllipse CenterX=-53.0822 CenterY=-10.0128 CenterZ=0 NormalX=0 NormalY=0 NormalZ=1 MajorRadius=0.8 MinorRadius=0.381246 AngleXU=0 StartAngle=5.48058 EndAngle=6.28319
    g375: LineSegment StartX=-56.4849 StartY=-5.4831 StartZ=0 EndX=-59.9269 EndY=-7.06791 EndZ=0
    g376: LineSegment StartX=-59.9269 StartY=-7.06791 StartZ=0 EndX=-59.9408 EndY=-7.45282 EndZ=0
    g377: LineSegment StartX=-59.9408 StartY=-7.45282 StartZ=0 EndX=-53.5083 EndY=-10.6256 EndZ=0
    g378: LineSegment StartX=-53.5083 StartY=-10.6256 StartZ=0 EndX=-52.7006 EndY=-10.6323 EndZ=0
    g379: LineSegment StartX=-52.7006 StartY=-10.6323 StartZ=0 EndX=-46.0429 EndY=-7.56683 EndZ=0
    g380: LineSegment StartX=-46.0429 StartY=-7.56683 StartZ=0 EndX=-46.029 EndY=-7.18191 EndZ=0
    g381: LineSegment StartX=-46.029 StartY=-7.18191 StartZ=0 EndX=-49.4849 EndY=-5.47728 EndZ=0
    g382: LineSegment StartX=-46.038 StartY=-7.60923 StartZ=0 EndX=-46.029 EndY=-7.35774 EndZ=0
    g383: LineSegment StartX=-49.8144 StartY=-9.47917 StartZ=0 EndX=-48.4722 EndY=-8.8612 EndZ=0
    g384: LineSegment StartX=-59.9408 StartY=-7.45282 StartZ=0 EndX=-59.9408 EndY=-7.50208 EndZ=0
    g385: LineSegment StartX=-53.5083 StartY=-10.6256 StartZ=0 EndX=-53.5083 EndY=-10.6331 EndZ=0
    g386: LineSegment StartX=-52.7006 StartY=-10.6323 StartZ=0 EndX=-52.7006 EndY=-10.6397 EndZ=0
    g387: LineSegment StartX=-46.0429 StartY=-7.56683 StartZ=0 EndX=-46.0429 EndY=-7.61144 EndZ=0
    g388: LineSegment StartX=-46.029 StartY=-7.18191 StartZ=0 EndX=-46.029 EndY=-7.35774 EndZ=0
    g389: ArcOfEllipse CenterX=-58.6409 CenterY=-7.00723 CenterZ=0 NormalX=0 NormalY=0 NormalZ=1 MajorRadius=0.8 MinorRadius=0.381246 AngleXU=-3.14159 StartAngle=3.14159 EndAngle=5.48058
    g390: ArcOfEllipse CenterX=-58.6409 CenterY=-7.00723 CenterZ=0 NormalX=0 NormalY=0 NormalZ=1 MajorRadius=0.8 MinorRadius=0.381246 AngleXU=-3.14159 StartAngle=2.33898 EndAngle=3.14159
    g391: ArcOfEllipse CenterX=-47.3289 CenterY=-7.10002 CenterZ=0 NormalX=0 NormalY=0 NormalZ=1 MajorRadius=0.8 MinorRadius=0.381246 AngleXU=-3.14159 StartAngle=3.90978 EndAngle=5.48058
    g392: ArcOfEllipse CenterX=-47.3289 CenterY=-7.10002 CenterZ=0 NormalX=0 NormalY=0 NormalZ=1 MajorRadius=0.8 MinorRadius=0.381246 AngleXU=-3.14159 StartAngle=3.14159 EndAngle=3.90978
    g393: ArcOfEllipse CenterX=-47.3289 CenterY=-7.10002 CenterZ=0 NormalX=0 NormalY=0 NormalZ=1 MajorRadius=0.8 MinorRadius=0.381246 AngleXU=-3.14159 StartAngle=2.33898 EndAngle=3.14159
    g394: ArcOfEllipse CenterX=-53.0822 CenterY=-9.74904 CenterZ=0 NormalX=0 NormalY=0 NormalZ=1 MajorRadius=0.8 MinorRadius=0.381246 AngleXU=0 StartAngle=5.48058 EndAngle=6.28319
    g395: ArcOfEllipse CenterX=-53.0822 CenterY=-9.74904 CenterZ=0 NormalX=0 NormalY=0 NormalZ=1 MajorRadius=0.8 MinorRadius=0.381246 AngleXU=0 StartAngle=0 EndAngle=2.33898
    g396: ArcOfEllipse CenterX=-52.9849 CenterY=-7.4932 CenterZ=0 NormalX=0 NormalY=0 NormalZ=1 MajorRadius=3.5 MinorRadius=1.66795 AngleXU=0 StartAngle=5.75398 EndAngle=6.28319
    g397: ArcOfEllipse CenterX=-52.9849 CenterY=-7.4932 CenterZ=0 NormalX=0 NormalY=0 NormalZ=1 MajorRadius=3.5 MinorRadius=1.66795 AngleXU=0 StartAngle=3.14159 EndAngle=3.6708
    g398: ArcOfEllipse CenterX=-47.3289 CenterY=-7.10002 CenterZ=0 NormalX=0 NormalY=0 NormalZ=1 MajorRadius=0.8 MinorRadius=0.381246 AngleXU=-3.14159 StartAngle=0 EndAngle=2.33898
    g399: ArcOfEllipse CenterX=-47.3289 CenterY=-7.10002 CenterZ=0 NormalX=0 NormalY=0 NormalZ=1 MajorRadius=0.8 MinorRadius=0.381246 AngleXU=-3.14159 StartAngle=5.48058 EndAngle=6.28319
    ... +792 more geometry lines
FEATURE [Sketcher::SketchObject] Sketch066
  ArcFitTolerance = 1e-06
  FullyConstrained = false
  MakeInternals = false
  sketch-geometry (9603):
    g0: LineSegment StartX=19.1468 StartY=-10.3376 StartZ=0 EndX=19.6616 EndY=-10.3296 EndZ=0
    g1: LineSegment StartX=21.4603 StartY=-8.14082 StartZ=0 EndX=22.8119 EndY=-8.11987 EndZ=0
    g2: LineSegment StartX=21.4603 StartY=-8.14082 StartZ=0 EndX=18.5618 EndY=-6.71111 EndZ=0
    g3: ArcOfEllipse CenterX=14.7472 CenterY=-9.12662 CenterZ=0 NormalX=0 NormalY=0 NormalZ=1 MajorRadius=0.4572 MinorRadius=0.289067 AngleXU=-2.02903 StartAngle=5.02584 EndAngle=6.28319
    g4: LineSegment StartX=17.519 StartY=-10.4366 StartZ=0 EndX=17.4138 EndY=-10.3847 EndZ=0
    g5: LineSegment StartX=17.519 StartY=-10.4366 StartZ=0 EndX=20.1546 EndY=-10.3958 EndZ=0
    g6: LineSegment StartX=19.7026 StartY=-10.1728 StartZ=0 EndX=20.1546 EndY=-10.3958 EndZ=0
    g7: LineSegment StartX=18.3798 StartY=-2.92346 StartZ=0 EndX=18.6501 EndY=-2.91927 EndZ=0
    g8: ArcOfEllipse CenterX=18.6888 CenterY=-2.91868 CenterZ=0 NormalX=0 NormalY=0 NormalZ=1 MajorRadius=0.0572 MinorRadius=0.036165 AngleXU=-2.02903 StartAngle=3.45504 EndAngle=5.02584
    g9: LineSegment StartX=18.7028 StartY=-2.86494 StartZ=0 EndX=18.9345 EndY=-2.86135 EndZ=0
    g10: LineSegment StartX=19.0329 StartY=-2.4856 StartZ=0 EndX=18.9345 EndY=-2.86135 EndZ=0
    g11: LineSegment StartX=18.8012 StartY=-2.48919 StartZ=0 EndX=19.0329 EndY=-2.4856 EndZ=0
    g12: ArcOfEllipse CenterX=18.6888 CenterY=-2.91868 CenterZ=0 NormalX=0 NormalY=0 NormalZ=1 MajorRadius=0.4572 MinorRadius=0.289067 AngleXU=-2.02903 StartAngle=3.45504 EndAngle=5.02584
    g13: LineSegment StartX=20.5909 StartY=-4.82241 StartZ=0 EndX=20.6844 EndY=-4.46544 EndZ=0
    g14: LineSegment StartX=20.6844 StartY=-4.46544 StartZ=0 EndX=21.2385 EndY=-4.45686 EndZ=0
    g15: LineSegment StartX=21.4402 StartY=-3.68657 StartZ=0 EndX=20.8861 EndY=-3.69516 EndZ=0
    g16: LineSegment StartX=20.8861 StartY=-3.69516 StartZ=0 EndX=21.0319 EndY=-3.13829 EndZ=0
    g17: LineSegment StartX=19.1532 StartY=-3.16741 StartZ=0 EndX=21.0319 EndY=-3.13829 EndZ=0
    g18: LineSegment StartX=17.2627 StartY=-10.3871 StartZ=0 EndX=19.1415 EndY=-10.358 EndZ=0
    g19: LineSegment StartX=19.1415 StartY=-10.358 StartZ=0 EndX=19.2873 EndY=-9.8011 EndZ=0
    g20: LineSegment StartX=19.2873 StartY=-9.8011 StartZ=0 EndX=19.8414 EndY=-9.79252 EndZ=0
    g21: LineSegment StartX=20.0431 StartY=-9.02223 StartZ=0 EndX=19.489 EndY=-9.03082 EndZ=0
    g22: LineSegment StartX=19.489 StartY=-9.03082 StartZ=0 EndX=19.5824 EndY=-8.67385 EndZ=0
    g23: LineSegment StartX=18.0416 StartY=-8.69773 StartZ=0 EndX=19.5824 EndY=-8.67385 EndZ=0
    g24: LineSegment StartX=19.0501 StartY=-4.84629 StartZ=0 EndX=18.0416 EndY=-8.69773 EndZ=0
    g25: LineSegment StartX=20.5909 StartY=-4.82241 StartZ=0 EndX=19.0501 EndY=-4.84629 EndZ=0
    g26: LineSegment StartX=19.1143 StartY=-1.18489 StartZ=0 EndX=16.4787 EndY=-1.22574 EndZ=0
    g27: LineSegment StartX=16.4787 StartY=-1.22574 StartZ=0 EndX=16.3803 EndY=-1.60149 EndZ=0
    g28: LineSegment StartX=19.7944 StartY=-9.82235 StartZ=0 EndX=19.2796 EndY=-9.83033 EndZ=0
    g29: LineSegment StartX=19.7944 StartY=-9.82235 StartZ=0 EndX=19.7372 EndY=-9.79413 EndZ=0
    g30: LineSegment StartX=16.3803 StartY=-1.60149 StartZ=0 EndX=16.4656 EndY=-1.64358 EndZ=0
    g31: LineSegment StartX=16.4787 StartY=-1.22574 StartZ=0 EndX=16.9817 EndY=-1.47387 EndZ=0
    g32: LineSegment StartX=18.0788 StartY=-8.55576 StartZ=0 EndX=19.3045 EndY=-8.53676 EndZ=0
    g33: LineSegment StartX=19.5477 StartY=-8.65672 StartZ=0 EndX=19.5824 EndY=-8.67385 EndZ=0
    g34: LineSegment StartX=19.3045 StartY=-8.53676 StartZ=0 EndX=19.5477 EndY=-8.65672 EndZ=0
    g35: LineSegment StartX=19.4376 StartY=-3.10949 StartZ=0 EndX=18.9345 EndY=-2.86135 EndZ=0
    g36: LineSegment StartX=19.5359 StartY=-2.73374 StartZ=0 EndX=19.4376 EndY=-3.10949 EndZ=0
    g37: LineSegment StartX=19.5359 StartY=-2.73374 StartZ=0 EndX=19.0329 EndY=-2.4856 EndZ=0
    g38: ArcOfEllipse CenterX=16.7983 CenterY=-10.1384 CenterZ=0 NormalX=0 NormalY=0 NormalZ=1 MajorRadius=0.4572 MinorRadius=0.289067 AngleXU=-2.02903 StartAngle=5.02584 EndAngle=6.28319
    g39: ArcOfEllipse CenterX=16.7983 CenterY=-10.1384 CenterZ=0 NormalX=0 NormalY=0 NormalZ=1 MajorRadius=0.4572 MinorRadius=0.289067 AngleXU=-2.02903 StartAngle=0 EndAngle=0.313451
    g40: LineSegment StartX=16.6859 StartY=-10.5678 StartZ=0 EndX=16.9175 EndY=-10.5642 EndZ=0
    g41: LineSegment StartX=16.9175 StartY=-10.5642 StartZ=0 EndX=16.9747 EndY=-10.3461 EndZ=0
    g42: LineSegment StartX=19.1143 StartY=-1.18489 StartZ=0 EndX=19.7945 EndY=-1.52042 EndZ=0
    g43: LineSegment StartX=16.7501 StartY=-1.47746 StartZ=0 EndX=16.9817 EndY=-1.47387 EndZ=0
    g44: LineSegment StartX=22.1716 StartY=-2.69289 StartZ=0 EndX=19.5359 EndY=-2.73374 EndZ=0
    g45: LineSegment StartX=21.4913 StartY=-2.35736 StartZ=0 EndX=22.1716 EndY=-2.69289 EndZ=0
    g46: ArcOfEllipse CenterX=21.2266 CenterY=-2.22679 CenterZ=0 NormalX=0 NormalY=0 NormalZ=1 MajorRadius=0.381 MinorRadius=0.0910178 AngleXU=-0.256096 StartAngle=2.43255 EndAngle=3.14159
    g47: ArcOfEllipse CenterX=21.2266 CenterY=-2.22679 CenterZ=0 NormalX=0 NormalY=0 NormalZ=1 MajorRadius=0.381 MinorRadius=0.0910178 AngleXU=-0.256096 StartAngle=3.14159 EndAngle=5.57414
    g48: LineSegment StartX=20.9606 StartY=-2.09559 StartZ=0 EndX=20.9619 EndY=-2.09621 EndZ=0
    g49: LineSegment StartX=20.9606 StartY=-2.09559 StartZ=0 EndX=21.2036 EndY=-2.1031 EndZ=0
    g50: LineSegment StartX=21.1154 StartY=-1.7251 StartZ=0 EndX=20.3253 EndY=-1.7822 EndZ=0
    g51: LineSegment StartX=20.324 StartY=-1.78158 StartZ=0 EndX=20.3253 EndY=-1.7822 EndZ=0
    g52: ArcOfEllipse CenterX=20.0593 CenterY=-1.651 CenterZ=0 NormalX=0 NormalY=0 NormalZ=1 MajorRadius=0.381 MinorRadius=0.0910178 AngleXU=-0.256096 StartAngle=2.43255 EndAngle=3.14159
    g53: ArcOfEllipse CenterX=20.0593 CenterY=-1.651 CenterZ=0 NormalX=0 NormalY=0 NormalZ=1 MajorRadius=0.381 MinorRadius=0.0910178 AngleXU=-0.256096 StartAngle=3.14159 EndAngle=5.57414
    g54: LineSegment StartX=19.7945 StartY=-1.52042 StartZ=0 EndX=19.7645 EndY=-1.63508 EndZ=0
    g55: ArcOfEllipse CenterX=19.5635 CenterY=-9.65543 CenterZ=0 NormalX=0 NormalY=0 NormalZ=1 MajorRadius=0.4 MinorRadius=0.0955568 AngleXU=-0.256096 StartAngle=5.57414 EndAngle=6.28319
    g56: ArcOfEllipse CenterX=19.7652 CenterY=-8.88514 CenterZ=0 NormalX=0 NormalY=0 NormalZ=1 MajorRadius=0.4 MinorRadius=0.0955568 AngleXU=2.8855 StartAngle=3.14159 EndAngle=3.98608
    g57: ArcOfEllipse CenterX=19.7652 CenterY=-8.88514 CenterZ=0 NormalX=0 NormalY=0 NormalZ=1 MajorRadius=0.4 MinorRadius=0.0955568 AngleXU=2.8855 StartAngle=2.43255 EndAngle=3.14159
    g58: LineSegment StartX=17.4206 StartY=-10.8124 StartZ=0 EndX=20.0562 EndY=-10.7715 EndZ=0
    g59: LineSegment StartX=17.4206 StartY=-10.8124 StartZ=0 EndX=16.9175 EndY=-10.5642 EndZ=0
    g60: LineSegment StartX=14.3633 StartY=-9.30438 StartZ=0 EndX=14.4217 EndY=-9.33315 EndZ=0
    g61: LineSegment StartX=21.0319 StartY=-3.13829 StartZ=0 EndX=20.9267 EndY=-3.08641 EndZ=0
    g62: LineSegment StartX=21.8293 StartY=-6.73176 StartZ=0 EndX=23.1809 EndY=-6.71081 EndZ=0
    g63: LineSegment StartX=23.3039 StartY=-6.24112 StartZ=0 EndX=23.1809 EndY=-6.71081 EndZ=0
    g64: LineSegment StartX=21.9523 StartY=-6.26207 StartZ=0 EndX=23.3039 EndY=-6.24112 EndZ=0
    g65: LineSegment StartX=21.9523 StartY=-6.26207 StartZ=0 EndX=21.8293 EndY=-6.73176 EndZ=0
    g66: ArcOfEllipse CenterX=21.1623 CenterY=-3.54948 CenterZ=0 NormalX=0 NormalY=0 NormalZ=1 MajorRadius=0.4 MinorRadius=0.0955568 AngleXU=2.8855 StartAngle=3.14159 EndAngle=3.98608
    g67: ArcOfEllipse CenterX=21.1623 CenterY=-3.54948 CenterZ=0 NormalX=0 NormalY=0 NormalZ=1 MajorRadius=0.4 MinorRadius=0.0955568 AngleXU=2.8855 StartAngle=2.43255 EndAngle=3.14159
    g68: ArcOfEllipse CenterX=20.9606 CenterY=-4.31977 CenterZ=0 NormalX=0 NormalY=0 NormalZ=1 MajorRadius=0.4 MinorRadius=0.0955568 AngleXU=-0.256096 StartAngle=5.57414 EndAngle=6.28319
    g69: LineSegment StartX=19.081 StartY=-4.84581 StartZ=0 EndX=21.9523 EndY=-6.26207 EndZ=0
    g70: LineSegment StartX=20.4326 StartY=-4.82486 StartZ=0 EndX=23.3039 EndY=-6.24112 EndZ=0
    g71: ArcOfEllipse CenterX=16.9848 CenterY=-10.25 CenterZ=0 NormalX=0 NormalY=0 NormalZ=1 MajorRadius=0.4 MinorRadius=0.0955568 AngleXU=2.8855 StartAngle=0.861754 EndAngle=2.43255
    g72: ArcOfEllipse CenterX=18.8752 CenterY=-3.03032 CenterZ=0 NormalX=0 NormalY=0 NormalZ=1 MajorRadius=0.4 MinorRadius=0.0955568 AngleXU=2.8855 StartAngle=0.861754 EndAngle=2.43255
    g73: LineSegment StartX=18.1403 StartY=-8.32091 StartZ=0 EndX=19.366 EndY=-8.30192 EndZ=0
    g74: LineSegment StartX=21.4178 StartY=-3.62246 StartZ=0 EndX=20.903 EndY=-3.63044 EndZ=0
    g75: LineSegment StartX=16.4894 StartY=-10.1431 StartZ=0 EndX=16.7145 EndY=-10.2542 EndZ=0
    g76: LineSegment StartX=18.8752 StartY=-3.03032 StartZ=0 EndX=19.2648 EndY=-3.02428 EndZ=0
    g77: LineSegment StartX=21.1841 StartY=-4.51487 StartZ=0 EndX=20.6694 EndY=-4.52285 EndZ=0
    g78: LineSegment StartX=21.1841 StartY=-4.51487 StartZ=0 EndX=21.0717 EndY=-4.45944 EndZ=0
    g79: LineSegment StartX=20.0281 StartY=-8.92994 StartZ=0 EndX=20.3749 EndY=-7.60542 EndZ=0
    g80: LineSegment StartX=21.0263 StartY=-5.11769 StartZ=0 EndX=21.1841 EndY=-4.51487 EndZ=0
    g81: LineSegment StartX=19.6616 StartY=-10.3296 StartZ=0 EndX=19.7944 EndY=-9.82235 EndZ=0
    g82: LineSegment StartX=21.475 StartY=-3.07791 StartZ=0 EndX=21.5506 EndY=-3.1152 EndZ=0
    g83: LineSegment StartX=21.4178 StartY=-3.62246 StartZ=0 EndX=21.5506 EndY=-3.1152 EndZ=0
    g84: LineSegment StartX=18.3798 StartY=-2.92346 StartZ=0 EndX=18.6049 EndY=-3.03451 EndZ=0
    g85: LineSegment StartX=18.6501 StartY=-2.91927 StartZ=0 EndX=18.8752 EndY=-3.03032 EndZ=0
    g86: LineSegment StartX=21.5833 StartY=-7.67113 StartZ=0 EndX=21.4603 EndY=-8.14082 EndZ=0
    g87: LineSegment StartX=21.3589 StartY=-7.03008 StartZ=0 EndX=21.5833 EndY=-7.67113 EndZ=0
    g88: LineSegment StartX=21.8293 StartY=-6.73176 StartZ=0 EndX=21.3589 EndY=-7.03008 EndZ=0
    g89: LineSegment StartX=20.0281 StartY=-8.92994 StartZ=0 EndX=19.5133 EndY=-8.93792 EndZ=0
    g90: ArcOfEllipse CenterX=16.6376 CenterY=-1.90695 CenterZ=0 NormalX=0 NormalY=0 NormalZ=1 MajorRadius=0.4572 MinorRadius=0.289067 AngleXU=-2.02903 StartAngle=3.45504 EndAngle=5.02584
    g91: LineSegment StartX=21.5506 StartY=-3.1152 StartZ=0 EndX=21.0023 EndY=-3.1237 EndZ=0
    g92: LineSegment StartX=16.4573 StartY=-1.65381 StartZ=0 EndX=16.0959 EndY=-1.65941 EndZ=0
    g93: LineSegment StartX=18.6852 StartY=-2.87023 StartZ=0 EndX=19.0056 EndY=-3.0283 EndZ=0
    g94: LineSegment StartX=22.1716 StartY=-2.69289 StartZ=0 EndX=22.0732 EndY=-3.06864 EndZ=0
    g95: LineSegment StartX=22.0732 StartY=-3.06864 StartZ=0 EndX=19.4376 EndY=-3.10949 EndZ=0
    g96: LineSegment StartX=23.1809 StartY=-6.71081 StartZ=0 EndX=22.7105 EndY=-7.00913 EndZ=0
    g97: LineSegment StartX=22.7105 StartY=-7.00913 StartZ=0 EndX=22.9349 EndY=-7.65019 EndZ=0
    g98: LineSegment StartX=22.9349 StartY=-7.65019 StartZ=0 EndX=22.8119 EndY=-8.11987 EndZ=0
    g99: LineSegment StartX=16.1035 StartY=-1.80069 StartZ=0 EndX=16.3286 EndY=-1.91174 EndZ=0
    g100: LineSegment StartX=14.2131 StartY=-9.02037 StartZ=0 EndX=14.4382 EndY=-9.13141 EndZ=0
    g101: ArcOfEllipse CenterX=16.3738 CenterY=-1.7965 CenterZ=0 NormalX=0 NormalY=0 NormalZ=1 MajorRadius=0.4 MinorRadius=0.0955568 AngleXU=-0.256096 StartAngle=2.43255 EndAngle=3.14159
    g102: ArcOfEllipse CenterX=16.3738 CenterY=-1.7965 CenterZ=0 NormalX=0 NormalY=0 NormalZ=1 MajorRadius=0.4 MinorRadius=0.0955568 AngleXU=-0.256096 StartAngle=3.14159 EndAngle=4.00335
    g103: ArcOfEllipse CenterX=14.4834 CenterY=-9.01618 CenterZ=0 NormalX=0 NormalY=0 NormalZ=1 MajorRadius=0.4 MinorRadius=0.0955568 AngleXU=-0.256096 StartAngle=3.14159 EndAngle=4.00335
    g104: LineSegment StartX=14.3633 StartY=-9.30438 StartZ=0 EndX=14.412 EndY=-9.11849 EndZ=0
    g105: LineSegment StartX=21.3589 StartY=-7.03008 StartZ=0 EndX=22.7105 EndY=-7.00913 EndZ=0
    g106: LineSegment StartX=21.5833 StartY=-7.67113 StartZ=0 EndX=22.9349 EndY=-7.65019 EndZ=0
    g107: LineSegment StartX=17.4206 StartY=-10.8124 StartZ=0 EndX=17.519 EndY=-10.4366 EndZ=0
    g108: LineSegment StartX=20.0562 StartY=-10.7715 StartZ=0 EndX=20.1546 EndY=-10.3958 EndZ=0
    g109: LineSegment StartX=20.9619 StartY=-2.09621 StartZ=0 EndX=20.9318 EndY=-2.21087 EndZ=0
    g110: LineSegment StartX=20.5515 StartY=-4.82302 StartZ=0 EndX=20.5375 EndY=-4.8766 EndZ=0
    g111: LineSegment StartX=19.8861 StartY=-7.36433 StartZ=0 EndX=19.5477 EndY=-8.65672 EndZ=0
    g112: LineSegment StartX=19.6429 StartY=-7.24437 StartZ=0 EndX=19.366 EndY=-8.30192 EndZ=0
    g113: LineSegment StartX=-22.2234 StartY=25.9642 StartZ=0 EndX=-22.4829 EndY=24.9732 EndZ=0
    g114: LineSegment StartX=-22.6998 StartY=24.1448 StartZ=0 EndX=-22.7189 EndY=24.0716 EndZ=0
    g115: LineSegment StartX=-21.663 StartY=23.263 StartZ=0 EndX=-21.5198 EndY=23.1923 EndZ=0
    g116: LineSegment StartX=-14.1861 StartY=20.4483 StartZ=0 EndX=-13.9472 EndY=20.5998 EndZ=0
    g117: LineSegment StartX=-13.9472 StartY=20.5998 StartZ=0 EndX=-13.4473 EndY=22.5087 EndZ=0
    g118: LineSegment StartX=-13.4473 StartY=22.5087 StartZ=0 EndX=-13.5614 EndY=22.8343 EndZ=0
    g119: LineSegment StartX=-13.5614 StartY=22.8343 StartZ=0 EndX=-14.9733 EndY=23.5307 EndZ=0
    g120: LineSegment StartX=-15.2637 StartY=23.5262 StartZ=0 EndX=-15.3262 EndY=23.7048 EndZ=0
    g121: LineSegment StartX=-15.3262 StartY=23.7048 StartZ=0 EndX=-15.36 EndY=23.7215 EndZ=0
    g122: LineSegment StartX=-20.2618 StartY=26.1393 StartZ=0 EndX=-20.2679 EndY=26.1423 EndZ=0
    g123: LineSegment StartX=-19.8981 StartY=22.3925 StartZ=0 EndX=-19.7549 EndY=22.3218 EndZ=0
    g124: LineSegment StartX=-18.1333 StartY=21.5219 StartZ=0 EndX=-17.6675 EndY=21.2922 EndZ=0
    g125: LineSegment StartX=-17.6675 StartY=21.2922 StartZ=0 EndX=-17.4286 EndY=21.4438 EndZ=0
    g126: LineSegment StartX=-17.4286 StartY=21.4438 StartZ=0 EndX=-17.3146 EndY=21.1181 EndZ=0
    g127: LineSegment StartX=-17.3146 StartY=21.1181 StartZ=0 EndX=-15.9027 EndY=20.4217 EndZ=0
    g128: LineSegment StartX=-15.9027 StartY=20.4217 StartZ=0 EndX=-15.6637 EndY=20.5732 EndZ=0
    g129: LineSegment StartX=-15.6637 StartY=20.5732 StartZ=0 EndX=-15.1639 EndY=22.4821 EndZ=0
    g130: LineSegment StartX=-15.1639 StartY=22.4821 StartZ=0 EndX=-15.2779 EndY=22.8077 EndZ=0
    g131: LineSegment StartX=-15.2779 StartY=22.8077 StartZ=0 EndX=-16.6898 EndY=23.5041 EndZ=0
    g132: LineSegment StartX=-16.6898 StartY=23.5041 StartZ=0 EndX=-16.9287 EndY=23.3526 EndZ=0
    g133: LineSegment StartX=-16.9287 StartY=23.3526 StartZ=0 EndX=-17.0428 EndY=23.6782 EndZ=0
    g134: LineSegment StartX=-17.0428 StartY=23.6782 StartZ=0 EndX=-18.4547 EndY=24.3747 EndZ=0
    g135: LineSegment StartX=-18.4547 StartY=24.3747 StartZ=0 EndX=-18.6936 EndY=24.2231 EndZ=0
    g136: LineSegment StartX=-18.6936 StartY=24.2231 StartZ=0 EndX=-18.8076 EndY=24.5488 EndZ=0
    g137: LineSegment StartX=-18.8076 StartY=24.5488 StartZ=0 EndX=-20.2195 EndY=25.2452 EndZ=0
    g138: LineSegment StartX=-20.2195 StartY=25.2452 StartZ=0 EndX=-20.4585 EndY=25.0936 EndZ=0
    g139: LineSegment StartX=-20.4585 StartY=25.0936 StartZ=0 EndX=-20.5725 EndY=25.4193 EndZ=0
    g140: LineSegment StartX=-20.5725 StartY=25.4193 StartZ=0 EndX=-21.9844 EndY=26.1157 EndZ=0
    g141: LineSegment StartX=-21.9844 StartY=26.1157 StartZ=0 EndX=-22.2234 EndY=25.9642 EndZ=0
    g142: LineSegment StartX=-17.76 StartY=23.0244 StartZ=0 EndX=-18.2047 EndY=23.2437 EndZ=0
    g143: LineSegment StartX=-17.76 StartY=23.0244 StartZ=0 EndX=-17.9175 EndY=22.4232 EndZ=0
    g144: LineSegment StartX=-15.9952 StartY=22.1538 StartZ=0 EndX=-16.4399 EndY=22.3732 EndZ=0
    g145: LineSegment StartX=-15.9952 StartY=22.1538 StartZ=0 EndX=-16.1526 EndY=21.5526 EndZ=0
    g146: LineSegment StartX=-21.2898 StartY=24.7654 StartZ=0 EndX=-21.7345 EndY=24.9848 EndZ=0
    g147: LineSegment StartX=-21.2898 StartY=24.7654 StartZ=0 EndX=-21.4472 EndY=24.1642 EndZ=0
    g148: LineSegment StartX=-19.5249 StartY=23.8949 StartZ=0 EndX=-19.9696 EndY=24.1142 EndZ=0
    g149: LineSegment StartX=-19.5249 StartY=23.8949 StartZ=0 EndX=-19.6823 EndY=23.2937 EndZ=0
    g150: LineSegment StartX=-20.2679 StartY=26.1423 StartZ=0 EndX=-21.9844 EndY=26.1157 EndZ=0
    g151: LineSegment StartX=-19.7904 StartY=25.4314 StartZ=0 EndX=-20.5725 EndY=25.4193 EndZ=0
    g152: LineSegment StartX=-19.4395 StartY=25.2573 StartZ=0 EndX=-20.2195 EndY=25.2452 EndZ=0
    g153: LineSegment StartX=-17.7537 StartY=24.5651 StartZ=0 EndX=-18.8076 EndY=24.5488 EndZ=0
    g154: LineSegment StartX=-17.3771 StartY=21.2967 StartZ=0 EndX=-17.6675 EndY=21.2922 EndZ=0
    g155: LineSegment StartX=-17.4007 StartY=24.391 StartZ=0 EndX=-18.4547 EndY=24.3747 EndZ=0
    g156: LineSegment StartX=-15.3262 StartY=23.7048 StartZ=0 EndX=-15.3936 EndY=23.7038 EndZ=0
    g157: LineSegment StartX=-16.2628 StartY=23.6903 StartZ=0 EndX=-17.0428 EndY=23.6782 EndZ=0
    g158: LineSegment StartX=-14.1861 StartY=20.4483 StartZ=0 EndX=-15.9027 EndY=20.4217 EndZ=0
    g159: LineSegment StartX=-14.9733 StartY=23.5307 StartZ=0 EndX=-16.6898 EndY=23.5041 EndZ=0
    g160: LineSegment StartX=-13.9472 StartY=20.5998 StartZ=0 EndX=-15.6637 EndY=20.5732 EndZ=0
    g161: LineSegment StartX=-13.5614 StartY=22.8343 StartZ=0 EndX=-15.2779 EndY=22.8077 EndZ=0
    g162: LineSegment StartX=-13.4473 StartY=22.5087 StartZ=0 EndX=-15.1639 EndY=22.4821 EndZ=0
    g163: LineSegment StartX=-18.2047 StartY=23.2437 StartZ=0 EndX=-22.1514 EndY=23.1825 EndZ=0
    g164: LineSegment StartX=-22.3088 StartY=22.5813 StartZ=0 EndX=-22.1514 EndY=23.1825 EndZ=0
    g165: LineSegment StartX=-17.9175 StartY=22.4232 StartZ=0 EndX=-21.8641 EndY=22.362 EndZ=0
    g166: LineSegment StartX=-21.8641 StartY=22.362 StartZ=0 EndX=-22.3088 EndY=22.5813 EndZ=0
    g167: LineSegment StartX=-17.76 StartY=23.0244 StartZ=0 EndX=-21.7067 EndY=22.9632 EndZ=0
    g168: LineSegment StartX=-21.8641 StartY=22.362 StartZ=0 EndX=-21.7067 EndY=22.9632 EndZ=0
    g169: LineSegment StartX=-21.7067 StartY=22.9632 StartZ=0 EndX=-22.1514 EndY=23.1825 EndZ=0
    g170: LineSegment StartX=-15.9952 StartY=22.1538 StartZ=0 EndX=-19.9418 EndY=22.0927 EndZ=0
    g171: LineSegment StartX=-16.4399 StartY=22.3732 StartZ=0 EndX=-20.3865 EndY=22.312 EndZ=0
    g172: LineSegment StartX=-19.9418 StartY=22.0927 StartZ=0 EndX=-20.3865 EndY=22.312 EndZ=0
    g173: LineSegment StartX=-20.5439 StartY=21.7108 StartZ=0 EndX=-20.3865 EndY=22.312 EndZ=0
    g174: LineSegment StartX=-16.1526 StartY=21.5526 StartZ=0 EndX=-20.0993 EndY=21.4915 EndZ=0
    g175: LineSegment StartX=-20.0993 StartY=21.4915 StartZ=0 EndX=-20.5439 EndY=21.7108 EndZ=0
    g176: LineSegment StartX=-20.0993 StartY=21.4915 StartZ=0 EndX=-19.9418 EndY=22.0927 EndZ=0
    g177: LineSegment StartX=-21.2898 StartY=24.7654 StartZ=0 EndX=-25.2365 EndY=24.7043 EndZ=0
    g178: LineSegment StartX=-21.7345 StartY=24.9848 StartZ=0 EndX=-25.6812 EndY=24.9236 EndZ=0
    g179: LineSegment StartX=-25.2365 StartY=24.7043 StartZ=0 EndX=-25.6812 EndY=24.9236 EndZ=0
    g180: LineSegment StartX=-25.8386 StartY=24.3224 StartZ=0 EndX=-25.6812 EndY=24.9236 EndZ=0
    g181: LineSegment StartX=-21.4472 StartY=24.1642 StartZ=0 EndX=-25.3939 EndY=24.1031 EndZ=0
    g182: LineSegment StartX=-25.3939 StartY=24.1031 StartZ=0 EndX=-25.8386 EndY=24.3224 EndZ=0
    g183: LineSegment StartX=-25.3939 StartY=24.1031 StartZ=0 EndX=-25.2365 EndY=24.7043 EndZ=0
    g184: LineSegment StartX=-19.9696 StartY=24.1142 StartZ=0 EndX=-23.9163 EndY=24.0531 EndZ=0
    g185: LineSegment StartX=-24.0737 StartY=23.4519 StartZ=0 EndX=-23.9163 EndY=24.0531 EndZ=0
    g186: LineSegment StartX=-19.6823 StartY=23.2937 StartZ=0 EndX=-23.629 EndY=23.2325 EndZ=0
    g187: LineSegment StartX=-23.629 StartY=23.2325 StartZ=0 EndX=-24.0737 EndY=23.4519 EndZ=0
    g188: LineSegment StartX=-19.5249 StartY=23.8949 StartZ=0 EndX=-23.4716 EndY=23.8337 EndZ=0
    g189: LineSegment StartX=-23.629 StartY=23.2325 StartZ=0 EndX=-23.4716 EndY=23.8337 EndZ=0
    g190: LineSegment StartX=-23.4716 StartY=23.8337 StartZ=0 EndX=-23.9163 EndY=24.0531 EndZ=0
    g191: LineSegment StartX=-22.3088 StartY=22.5813 StartZ=0 EndX=-22.2664 EndY=22.6751 EndZ=0
    g192: LineSegment StartX=-22.1514 StartY=23.1825 StartZ=0 EndX=-22.1877 EndY=22.9757 EndZ=0
    g193: LineSegment StartX=-22.2664 StartY=22.6751 StartZ=0 EndX=-22.1877 EndY=22.9757 EndZ=0
    g194: LineSegment StartX=-21.8641 StartY=22.362 StartZ=0 EndX=-22.0441 EndY=22.5655 EndZ=0
    g195: LineSegment StartX=-22.0441 StartY=22.5655 StartZ=0 EndX=-22.2664 EndY=22.6751 EndZ=0
    g196: LineSegment StartX=-21.7067 StartY=22.9632 StartZ=0 EndX=-21.9654 EndY=22.8661 EndZ=0
    g197: LineSegment StartX=-22.0441 StartY=22.5655 StartZ=0 EndX=-21.9654 EndY=22.8661 EndZ=0
    g198: LineSegment StartX=-21.9654 StartY=22.8661 StartZ=0 EndX=-22.1877 EndY=22.9757 EndZ=0
    g199: LineSegment StartX=-19.9418 StartY=22.0927 StartZ=0 EndX=-20.2005 EndY=21.9955 EndZ=0
    g200: LineSegment StartX=-20.3865 StartY=22.312 StartZ=0 EndX=-20.4228 EndY=22.1052 EndZ=0
    g201: LineSegment StartX=-20.2005 StartY=21.9955 StartZ=0 EndX=-20.4228 EndY=22.1052 EndZ=0
    g202: LineSegment StartX=-20.5439 StartY=21.7108 StartZ=0 EndX=-20.5015 EndY=21.8046 EndZ=0
    g203: LineSegment StartX=-20.5015 StartY=21.8046 StartZ=0 EndX=-20.4228 EndY=22.1052 EndZ=0
    g204: LineSegment StartX=-20.0993 StartY=21.4915 StartZ=0 EndX=-20.2792 EndY=21.6949 EndZ=0
    g205: LineSegment StartX=-20.2792 StartY=21.6949 StartZ=0 EndX=-20.5015 EndY=21.8046 EndZ=0
    g206: LineSegment StartX=-20.2792 StartY=21.6949 StartZ=0 EndX=-20.2005 EndY=21.9955 EndZ=0
    g207: LineSegment StartX=-25.2365 StartY=24.7043 StartZ=0 EndX=-25.4951 EndY=24.6071 EndZ=0
    g208: LineSegment StartX=-25.6812 StartY=24.9236 StartZ=0 EndX=-25.7175 EndY=24.7168 EndZ=0
    g209: LineSegment StartX=-25.4951 StartY=24.6071 StartZ=0 EndX=-25.7175 EndY=24.7168 EndZ=0
    g210: LineSegment StartX=-25.8386 StartY=24.3224 StartZ=0 EndX=-25.7962 EndY=24.4162 EndZ=0
    g211: LineSegment StartX=-25.7962 StartY=24.4162 StartZ=0 EndX=-25.7175 EndY=24.7168 EndZ=0
    g212: LineSegment StartX=-25.3939 StartY=24.1031 StartZ=0 EndX=-25.5738 EndY=24.3065 EndZ=0
    g213: LineSegment StartX=-25.5738 StartY=24.3065 StartZ=0 EndX=-25.7962 EndY=24.4162 EndZ=0
    g214: LineSegment StartX=-25.5738 StartY=24.3065 StartZ=0 EndX=-25.4951 EndY=24.6071 EndZ=0
    g215: LineSegment StartX=-24.0737 StartY=23.4519 StartZ=0 EndX=-24.0313 EndY=23.5457 EndZ=0
    g216: LineSegment StartX=-23.9163 StartY=24.0531 StartZ=0 EndX=-23.9526 EndY=23.8463 EndZ=0
    g217: LineSegment StartX=-24.0313 StartY=23.5457 StartZ=0 EndX=-23.9526 EndY=23.8463 EndZ=0
    g218: LineSegment StartX=-23.629 StartY=23.2325 StartZ=0 EndX=-23.809 EndY=23.436 EndZ=0
    g219: LineSegment StartX=-23.809 StartY=23.436 StartZ=0 EndX=-24.0313 EndY=23.5457 EndZ=0
    g220: LineSegment StartX=-23.4716 StartY=23.8337 StartZ=0 EndX=-23.7302 EndY=23.7366 EndZ=0
    g221: LineSegment StartX=-23.809 StartY=23.436 StartZ=0 EndX=-23.7302 EndY=23.7366 EndZ=0
    g222: LineSegment StartX=-23.7302 StartY=23.7366 StartZ=0 EndX=-23.9526 EndY=23.8463 EndZ=0
    g223: ArcOfEllipse CenterX=11.3648 CenterY=18.171 CenterZ=0 NormalX=0 NormalY=0 NormalZ=1 MajorRadius=1.25 MinorRadius=0.790319 AngleXU=-2.02903 StartAngle=3.45504 EndAngle=6.28319
    g224: ArcOfEllipse CenterX=11.3648 CenterY=18.171 CenterZ=0 NormalX=0 NormalY=0 NormalZ=1 MajorRadius=1.25 MinorRadius=0.790319 AngleXU=-2.02903 StartAngle=0 EndAngle=0.451027
    g225: ArcOfEllipse CenterX=11.3648 CenterY=18.171 CenterZ=0 NormalX=0 NormalY=0 NormalZ=1 MajorRadius=1.25 MinorRadius=0.790319 AngleXU=-2.02903 StartAngle=2.69057 EndAngle=3.14159
    g226: ArcOfEllipse CenterX=11.3648 CenterY=18.171 CenterZ=0 NormalX=0 NormalY=0 NormalZ=1 MajorRadius=1.25 MinorRadius=0.790319 AngleXU=-2.02903 StartAngle=3.14159 EndAngle=3.45504
    g227: ArcOfEllipse CenterX=11.3648 CenterY=18.171 CenterZ=0 NormalX=0 NormalY=0 NormalZ=1 MajorRadius=1.125 MinorRadius=0.711287 AngleXU=1.11256 StartAngle=0 EndAngle=0.313451
    g228: ArcOfEllipse CenterX=11.3648 CenterY=18.171 CenterZ=0 NormalX=0 NormalY=0 NormalZ=1 MajorRadius=1.125 MinorRadius=0.711287 AngleXU=1.11256 StartAngle=0.313451 EndAngle=3.14159
    g229: ArcOfEllipse CenterX=13.5535 CenterY=17.0914 CenterZ=0 NormalX=0 NormalY=0 NormalZ=1 MajorRadius=1.25 MinorRadius=0.790319 AngleXU=-2.02903 StartAngle=3.50975 EndAngle=6.28319
    g230: BSplineCurve PolesCount=92 KnotsCount=19 Degree=6 IsPeriodic=0
    g231: ArcOfEllipse CenterX=20.7536 CenterY=4.13745 CenterZ=0 NormalX=0 NormalY=0 NormalZ=1 MajorRadius=1.36 MinorRadius=0.324893 AngleXU=-0.256096 StartAngle=4.00335 EndAngle=6.28319
    g232: ArcOfEllipse CenterX=20.7536 CenterY=4.13745 CenterZ=0 NormalX=0 NormalY=0 NormalZ=1 MajorRadius=1.36 MinorRadius=0.324893 AngleXU=-0.256096 StartAngle=3.14159 EndAngle=4.00335
    g233: ArcOfEllipse CenterX=21.0733 CenterY=5.35864 CenterZ=0 NormalX=0 NormalY=0 NormalZ=1 MajorRadius=1.36 MinorRadius=0.324893 AngleXU=-0.256096 StartAngle=4.00335 EndAngle=6.28319
    g234: ArcOfEllipse CenterX=21.0733 CenterY=5.35864 CenterZ=0 NormalX=0 NormalY=0 NormalZ=1 MajorRadius=1.36 MinorRadius=0.324893 AngleXU=-0.256096 StartAngle=0 EndAngle=0.121342
    g235: ArcOfEllipse CenterX=21.0733 CenterY=5.35864 CenterZ=0 NormalX=0 NormalY=0 NormalZ=1 MajorRadius=1.36 MinorRadius=0.324893 AngleXU=-0.256096 StartAngle=3.02025 EndAngle=3.14159
    g236: ArcOfEllipse CenterX=21.0733 CenterY=5.35864 CenterZ=0 NormalX=0 NormalY=0 NormalZ=1 MajorRadius=1.36 MinorRadius=0.324893 AngleXU=-0.256096 StartAngle=3.14159 EndAngle=4.00335
    g237: ArcOfEllipse CenterX=21.0733 CenterY=5.35864 CenterZ=0 NormalX=0 NormalY=0 NormalZ=1 MajorRadius=1.35 MinorRadius=0.322504 AngleXU=-0.256096 StartAngle=4.00335 EndAngle=6.28319
    g238: ArcOfEllipse CenterX=21.0733 CenterY=5.35864 CenterZ=0 NormalX=0 NormalY=0 NormalZ=1 MajorRadius=1.35 MinorRadius=0.322504 AngleXU=-0.256096 StartAngle=3.14159 EndAngle=4.00335
    g239: ArcOfEllipse CenterX=20.5617 CenterY=3.40474 CenterZ=0 NormalX=0 NormalY=0 NormalZ=1 MajorRadius=1.35 MinorRadius=0.322504 AngleXU=-0.256096 StartAngle=4.00335 EndAngle=6.28319
    g240: ArcOfEllipse CenterX=20.5617 CenterY=3.40474 CenterZ=0 NormalX=0 NormalY=0 NormalZ=1 MajorRadius=1.35 MinorRadius=0.322504 AngleXU=-0.256096 StartAngle=3.14159 EndAngle=4.00335
    g241: ArcOfEllipse CenterX=21.8408 CenterY=8.2895 CenterZ=0 NormalX=0 NormalY=0 NormalZ=1 MajorRadius=1.35 MinorRadius=0.322504 AngleXU=-0.256096 StartAngle=4.00335 EndAngle=6.28319
    g242: ArcOfEllipse CenterX=21.8408 CenterY=8.2895 CenterZ=0 NormalX=0 NormalY=0 NormalZ=1 MajorRadius=1.35 MinorRadius=0.322504 AngleXU=-0.256096 StartAngle=0 EndAngle=1.26998
    g243: ArcOfEllipse CenterX=21.8408 CenterY=8.2895 CenterZ=0 NormalX=0 NormalY=0 NormalZ=1 MajorRadius=1.35 MinorRadius=0.322504 AngleXU=-0.256096 StartAngle=1.87161 EndAngle=3.14159
    g244: ArcOfEllipse CenterX=21.8408 CenterY=8.2895 CenterZ=0 NormalX=0 NormalY=0 NormalZ=1 MajorRadius=1.35 MinorRadius=0.322504 AngleXU=-0.256096 StartAngle=3.14159 EndAngle=4.00335
    g245: ArcOfEllipse CenterX=21.8408 CenterY=8.2895 CenterZ=0 NormalX=0 NormalY=0 NormalZ=1 MajorRadius=0.4 MinorRadius=0.0955568 AngleXU=-0.256096 StartAngle=3.14159 EndAngle=6.28319
    g246: LineSegment StartX=2.61981 StartY=-19.2817 StartZ=0 EndX=3.02768 EndY=-17.724 EndZ=0
    g247: LineSegment StartX=2.28104 StartY=-16.9106 StartZ=0 EndX=1.54252 EndY=-16.5463 EndZ=0
    g248: LineSegment StartX=3.25905 StartY=-16.5197 StartZ=0 EndX=1.54252 EndY=-16.5463 EndZ=0
    g249: LineSegment StartX=3.99758 StartY=-16.884 StartZ=0 EndX=3.25905 EndY=-16.5197 EndZ=0
    g250: LineSegment StartX=2.96861 StartY=-16.5242 StartZ=0 EndX=2.90608 EndY=-16.3456 EndZ=0
    g251: LineSegment StartX=2.90608 StartY=-16.3456 StartZ=0 EndX=1.49418 EndY=-15.6492 EndZ=0
    g252: LineSegment StartX=1.20373 StartY=-15.6537 StartZ=0 EndX=1.1412 EndY=-15.4751 EndZ=0
    g253: LineSegment StartX=1.1412 StartY=-15.4751 StartZ=0 EndX=-0.270696 EndY=-14.7787 EndZ=0
    g254: LineSegment StartX=-0.561142 StartY=-14.7832 StartZ=0 EndX=-0.623671 EndY=-14.6046 EndZ=0
    g255: LineSegment StartX=-0.623671 StartY=-14.6046 StartZ=0 EndX=-2.03557 EndY=-13.9081 EndZ=0
    g256: LineSegment StartX=-2.32602 StartY=-13.9126 StartZ=0 EndX=-2.38855 EndY=-13.734 EndZ=0
    g257: LineSegment StartX=-2.38855 StartY=-13.734 StartZ=0 EndX=-3.80045 EndY=-13.0376 EndZ=0
    g258: LineSegment StartX=-4.09089 StartY=-13.0421 StartZ=0 EndX=-4.15342 EndY=-12.8635 EndZ=0
    g259: LineSegment StartX=-4.15342 StartY=-12.8635 StartZ=0 EndX=-5.56532 EndY=-12.1671 EndZ=0
    g260: LineSegment StartX=-5.85576 StartY=-12.1716 StartZ=0 EndX=-5.91829 EndY=-11.993 EndZ=0
    g261: LineSegment StartX=-5.91829 StartY=-11.993 StartZ=0 EndX=-7.33019 EndY=-11.2966 EndZ=0
    g262: LineSegment StartX=-7.62064 StartY=-11.3011 StartZ=0 EndX=-7.68317 EndY=-11.1225 EndZ=0
    g263: LineSegment StartX=-7.68317 StartY=-11.1225 StartZ=0 EndX=-9.09507 EndY=-10.426 EndZ=0
    g264: LineSegment StartX=-9.38551 StartY=-10.4305 StartZ=0 EndX=-9.44804 EndY=-10.2519 EndZ=0
    g265: LineSegment StartX=-9.44804 StartY=-10.2519 StartZ=0 EndX=-10.8599 EndY=-9.55552 EndZ=0
    g266: LineSegment StartX=-11.1504 StartY=-9.56002 StartZ=0 EndX=-11.2129 EndY=-9.38141 EndZ=0
    g267: LineSegment StartX=-11.2129 StartY=-9.38141 StartZ=0 EndX=-12.6248 EndY=-8.68499 EndZ=0
    g268: LineSegment StartX=1.54252 StartY=-16.5463 StartZ=0 EndX=1.30356 EndY=-16.6979 EndZ=0
    g269: LineSegment StartX=1.30356 StartY=-16.6979 StartZ=0 EndX=1.18954 EndY=-16.3722 EndZ=0
    g270: LineSegment StartX=1.18954 StartY=-16.3722 StartZ=0 EndX=-0.222355 EndY=-15.6758 EndZ=0
    g271: LineSegment StartX=-0.222355 StartY=-15.6758 StartZ=0 EndX=-0.461319 EndY=-15.8273 EndZ=0
    g272: LineSegment StartX=-0.461319 StartY=-15.8273 StartZ=0 EndX=-0.57533 EndY=-15.5017 EndZ=0
    g273: LineSegment StartX=-0.57533 StartY=-15.5017 StartZ=0 EndX=-1.98723 EndY=-14.8053 EndZ=0
    g274: LineSegment StartX=-1.98723 StartY=-14.8053 StartZ=0 EndX=-2.22619 EndY=-14.9568 EndZ=0
    g275: LineSegment StartX=-2.22619 StartY=-14.9568 StartZ=0 EndX=-2.3402 EndY=-14.6312 EndZ=0
    g276: LineSegment StartX=-2.3402 StartY=-14.6312 StartZ=0 EndX=-3.7521 EndY=-13.9347 EndZ=0
    g277: LineSegment StartX=-3.7521 StartY=-13.9347 StartZ=0 EndX=-3.99107 EndY=-14.0863 EndZ=0
    g278: LineSegment StartX=-3.99107 StartY=-14.0863 StartZ=0 EndX=-4.10508 EndY=-13.7606 EndZ=0
    g279: LineSegment StartX=-4.10508 StartY=-13.7606 StartZ=0 EndX=-5.51698 EndY=-13.0642 EndZ=0
    g280: LineSegment StartX=-5.51698 StartY=-13.0642 StartZ=0 EndX=-5.75594 EndY=-13.2158 EndZ=0
    g281: LineSegment StartX=-5.75594 StartY=-13.2158 StartZ=0 EndX=-5.86995 EndY=-12.8901 EndZ=0
    g282: LineSegment StartX=-5.86995 StartY=-12.8901 StartZ=0 EndX=-7.28185 EndY=-12.1937 EndZ=0
    g283: LineSegment StartX=-7.28185 StartY=-12.1937 StartZ=0 EndX=-7.52082 EndY=-12.3452 EndZ=0
    g284: LineSegment StartX=-7.52082 StartY=-12.3452 StartZ=0 EndX=-7.63483 EndY=-12.0196 EndZ=0
    g285: LineSegment StartX=-7.63483 StartY=-12.0196 StartZ=0 EndX=-9.04673 EndY=-11.3232 EndZ=0
    g286: LineSegment StartX=-9.04673 StartY=-11.3232 StartZ=0 EndX=-9.28569 EndY=-11.4747 EndZ=0
    g287: LineSegment StartX=-9.28569 StartY=-11.4747 StartZ=0 EndX=-9.3997 EndY=-11.1491 EndZ=0
    g288: LineSegment StartX=-9.3997 StartY=-11.1491 StartZ=0 EndX=-10.8116 EndY=-10.4526 EndZ=0
    g289: LineSegment StartX=-10.8116 StartY=-10.4526 StartZ=0 EndX=-11.0506 EndY=-10.6042 EndZ=0
    g290: LineSegment StartX=-11.0506 StartY=-10.6042 StartZ=0 EndX=-11.1646 EndY=-10.2785 EndZ=0
    g291: LineSegment StartX=-11.1646 StartY=-10.2785 StartZ=0 EndX=-12.5765 EndY=-9.58212 EndZ=0
    g292: LineSegment StartX=-12.5765 StartY=-9.58212 StartZ=0 EndX=-12.8154 EndY=-9.73367 EndZ=0
    g293: LineSegment StartX=-12.8154 StartY=-9.73367 StartZ=0 EndX=-12.9295 EndY=-9.40802 EndZ=0
    g294: LineSegment StartX=-12.9295 StartY=-9.40802 StartZ=0 EndX=-14.3413 EndY=-8.7116 EndZ=0
    g295: LineSegment StartX=-14.3413 StartY=-8.7116 StartZ=0 EndX=-14.5803 EndY=-8.86315 EndZ=0
    g296: LineSegment StartX=-14.5803 StartY=-8.86315 StartZ=0 EndX=-14.8398 EndY=-9.85414 EndZ=0
    g297: LineSegment StartX=-15.0567 StartY=-10.6825 StartZ=0 EndX=-15.0759 EndY=-10.7557 EndZ=0
    g298: LineSegment StartX=-14.02 StartY=-11.5643 StartZ=0 EndX=-13.8767 EndY=-11.635 EndZ=0
    g299: LineSegment StartX=-12.2551 StartY=-12.4348 StartZ=0 EndX=-12.1118 EndY=-12.5055 EndZ=0
    g300: LineSegment StartX=-10.4902 StartY=-13.3054 StartZ=0 EndX=-10.347 EndY=-13.376 EndZ=0
    g301: LineSegment StartX=-8.72533 StartY=-14.1759 StartZ=0 EndX=-8.58208 EndY=-14.2465 EndZ=0
    g302: LineSegment StartX=-6.96045 StartY=-15.0464 StartZ=0 EndX=-6.8172 EndY=-15.1171 EndZ=0
    g303: LineSegment StartX=-5.19558 StartY=-15.9169 StartZ=0 EndX=-5.05233 EndY=-15.9876 EndZ=0
    g304: LineSegment StartX=-3.43071 StartY=-16.7875 StartZ=0 EndX=-3.28746 EndY=-16.8581 EndZ=0
    g305: LineSegment StartX=-1.66583 StartY=-17.658 StartZ=0 EndX=-1.52258 EndY=-17.7286 EndZ=0
    g306: LineSegment StartX=0.0990424 StartY=-18.5285 StartZ=0 EndX=0.564778 EndY=-18.7582 EndZ=0
    g307: LineSegment StartX=0.564778 StartY=-18.7582 StartZ=0 EndX=0.803742 EndY=-18.6067 EndZ=0
    g308: LineSegment StartX=0.803742 StartY=-18.6067 StartZ=0 EndX=0.917753 EndY=-18.9323 EndZ=0
    g309: LineSegment StartX=0.917753 StartY=-18.9323 StartZ=0 EndX=1.65628 EndY=-19.2966 EndZ=0
    g310: LineSegment StartX=-7.03192 StartY=-13.3246 StartZ=0 EndX=-6.58723 EndY=-13.544 EndZ=0
    g311: LineSegment StartX=-6.74465 StartY=-14.1452 StartZ=0 EndX=-6.58723 EndY=-13.544 EndZ=0
    g312: LineSegment StartX=-5.26705 StartY=-14.1952 StartZ=0 EndX=-4.82235 EndY=-14.4145 EndZ=0
    g313: LineSegment StartX=-4.97978 StartY=-15.0157 StartZ=0 EndX=-4.82235 EndY=-14.4145 EndZ=0
    g314: LineSegment StartX=-3.50217 StartY=-15.0657 StartZ=0 EndX=-3.05748 EndY=-15.285 EndZ=0
    g315: LineSegment StartX=-3.2149 StartY=-15.8862 StartZ=0 EndX=-3.05748 EndY=-15.285 EndZ=0
    g316: LineSegment StartX=-10.5617 StartY=-11.5836 StartZ=0 EndX=-10.117 EndY=-11.8029 EndZ=0
    g317: LineSegment StartX=-10.2744 StartY=-12.4041 StartZ=0 EndX=-10.117 EndY=-11.8029 EndZ=0
    g318: LineSegment StartX=-8.7968 StartY=-12.4541 StartZ=0 EndX=-8.3521 EndY=-12.6735 EndZ=0
    g319: LineSegment StartX=-8.50952 StartY=-13.2747 StartZ=0 EndX=-8.3521 EndY=-12.6735 EndZ=0
    g320: LineSegment StartX=-14.0914 StartY=-9.84254 StartZ=0 EndX=-13.6467 EndY=-10.0619 EndZ=0
    g321: LineSegment StartX=-13.8041 StartY=-10.6631 StartZ=0 EndX=-13.6467 EndY=-10.0619 EndZ=0
    g322: LineSegment StartX=-12.3265 StartY=-10.7131 StartZ=0 EndX=-11.8819 EndY=-10.9324 EndZ=0
    g323: LineSegment StartX=-12.0393 StartY=-11.5336 StartZ=0 EndX=-11.8819 EndY=-10.9324 EndZ=0
    g324: LineSegment StartX=1.79245 StartY=-17.6773 StartZ=0 EndX=2.23714 EndY=-17.8966 EndZ=0
    g325: LineSegment StartX=2.07972 StartY=-18.4978 StartZ=0 EndX=2.23714 EndY=-17.8966 EndZ=0
    g326: LineSegment StartX=0.0275757 StartY=-16.8067 StartZ=0 EndX=0.472268 EndY=-17.0261 EndZ=0
    g327: LineSegment StartX=0.314847 StartY=-17.6273 StartZ=0 EndX=0.472268 EndY=-17.0261 EndZ=0
    g328: LineSegment StartX=-1.7373 StartY=-15.9362 StartZ=0 EndX=-1.29261 EndY=-16.1556 EndZ=0
    g329: LineSegment StartX=-1.45003 StartY=-16.7568 StartZ=0 EndX=-1.29261 EndY=-16.1556 EndZ=0
    g330: LineSegment StartX=2.90608 StartY=-16.3456 StartZ=0 EndX=1.18954 EndY=-16.3722 EndZ=0
    g331: LineSegment StartX=1.49418 StartY=-15.6492 StartZ=0 EndX=-0.222355 EndY=-15.6758 EndZ=0
    g332: LineSegment StartX=0.855223 StartY=-18.7537 StartZ=0 EndX=0.564778 EndY=-18.7582 EndZ=0
    g333: LineSegment StartX=1.1412 StartY=-15.4751 StartZ=0 EndX=-0.57533 EndY=-15.5017 EndZ=0
    g334: LineSegment StartX=-0.270696 StartY=-14.7787 StartZ=0 EndX=-1.98723 EndY=-14.8053 EndZ=0
    g335: LineSegment StartX=-0.623671 StartY=-14.6046 StartZ=0 EndX=-2.3402 EndY=-14.6312 EndZ=0
    g336: LineSegment StartX=-2.03557 StartY=-13.9081 StartZ=0 EndX=-3.7521 EndY=-13.9347 EndZ=0
    g337: LineSegment StartX=-2.38855 StartY=-13.734 StartZ=0 EndX=-4.10508 EndY=-13.7606 EndZ=0
    g338: LineSegment StartX=-3.80045 StartY=-13.0376 StartZ=0 EndX=-5.51698 EndY=-13.0642 EndZ=0
    g339: LineSegment StartX=-4.15342 StartY=-12.8635 StartZ=0 EndX=-5.86995 EndY=-12.8901 EndZ=0
    g340: LineSegment StartX=-5.56532 StartY=-12.1671 StartZ=0 EndX=-7.28185 EndY=-12.1937 EndZ=0
    g341: LineSegment StartX=-5.91829 StartY=-11.993 StartZ=0 EndX=-7.63483 EndY=-12.0196 EndZ=0
    g342: LineSegment StartX=-7.33019 StartY=-11.2966 StartZ=0 EndX=-9.04673 EndY=-11.3232 EndZ=0
    g343: LineSegment StartX=-7.68317 StartY=-11.1225 StartZ=0 EndX=-9.3997 EndY=-11.1491 EndZ=0
    g344: LineSegment StartX=-9.09507 StartY=-10.426 StartZ=0 EndX=-10.8116 EndY=-10.4526 EndZ=0
    g345: LineSegment StartX=-9.44804 StartY=-10.2519 StartZ=0 EndX=-11.1646 EndY=-10.2785 EndZ=0
    g346: LineSegment StartX=-10.8599 StartY=-9.55552 StartZ=0 EndX=-12.5765 EndY=-9.58212 EndZ=0
    g347: LineSegment StartX=-11.2129 StartY=-9.38141 StartZ=0 EndX=-12.9295 EndY=-9.40802 EndZ=0
    g348: LineSegment StartX=-12.6248 StartY=-8.68499 StartZ=0 EndX=-14.3413 EndY=-8.7116 EndZ=0
    g349: LineSegment StartX=-6.74465 StartY=-14.1452 StartZ=0 EndX=-10.6913 EndY=-14.2064 EndZ=0
    g350: LineSegment StartX=-11.136 StartY=-13.987 StartZ=0 EndX=-10.6913 EndY=-14.2064 EndZ=0
    g351: LineSegment StartX=-6.58723 StartY=-13.544 StartZ=0 EndX=-10.5339 EndY=-13.6052 EndZ=0
    g352: LineSegment StartX=-10.5339 StartY=-13.6052 StartZ=0 EndX=-10.6913 EndY=-14.2064 EndZ=0
    g353: LineSegment StartX=-7.03192 StartY=-13.3246 StartZ=0 EndX=-10.9786 EndY=-13.3858 EndZ=0
    g354: LineSegment StartX=-10.9786 StartY=-13.3858 StartZ=0 EndX=-10.5339 EndY=-13.6052 EndZ=0
    g355: LineSegment StartX=-10.9786 StartY=-13.3858 StartZ=0 EndX=-11.136 EndY=-13.987 EndZ=0
    g356: LineSegment StartX=-4.97978 StartY=-15.0157 StartZ=0 EndX=-8.92645 EndY=-15.0769 EndZ=0
    g357: LineSegment StartX=-9.37114 StartY=-14.8575 StartZ=0 EndX=-8.92645 EndY=-15.0769 EndZ=0
    g358: LineSegment StartX=-4.82235 StartY=-14.4145 StartZ=0 EndX=-8.76903 EndY=-14.4757 EndZ=0
    g359: LineSegment StartX=-8.76903 StartY=-14.4757 StartZ=0 EndX=-8.92645 EndY=-15.0769 EndZ=0
    g360: LineSegment StartX=-5.26705 StartY=-14.1952 StartZ=0 EndX=-9.21372 EndY=-14.2563 EndZ=0
    g361: LineSegment StartX=-9.21372 StartY=-14.2563 StartZ=0 EndX=-8.76903 EndY=-14.4757 EndZ=0
    g362: LineSegment StartX=-9.21372 StartY=-14.2563 StartZ=0 EndX=-9.37114 EndY=-14.8575 EndZ=0
    g363: LineSegment StartX=-3.2149 StartY=-15.8862 StartZ=0 EndX=-7.16158 EndY=-15.9474 EndZ=0
    g364: LineSegment StartX=-7.60627 StartY=-15.7281 StartZ=0 EndX=-7.16158 EndY=-15.9474 EndZ=0
    g365: LineSegment StartX=-3.05748 StartY=-15.285 StartZ=0 EndX=-7.00415 EndY=-15.3462 EndZ=0
    g366: LineSegment StartX=-7.00415 StartY=-15.3462 StartZ=0 EndX=-7.16158 EndY=-15.9474 EndZ=0
    g367: LineSegment StartX=-3.50217 StartY=-15.0657 StartZ=0 EndX=-7.44885 EndY=-15.1269 EndZ=0
    g368: LineSegment StartX=-7.44885 StartY=-15.1269 StartZ=0 EndX=-7.00415 EndY=-15.3462 EndZ=0
    g369: LineSegment StartX=-7.44885 StartY=-15.1269 StartZ=0 EndX=-7.60627 EndY=-15.7281 EndZ=0
    g370: LineSegment StartX=-10.5617 StartY=-11.5836 StartZ=0 EndX=-14.5083 EndY=-11.6448 EndZ=0
    g371: LineSegment StartX=-14.5083 StartY=-11.6448 StartZ=0 EndX=-14.6658 EndY=-12.246 EndZ=0
    g372: LineSegment StartX=-10.2744 StartY=-12.4041 StartZ=0 EndX=-14.2211 EndY=-12.4653 EndZ=0
    g373: LineSegment StartX=-14.6658 StartY=-12.246 StartZ=0 EndX=-14.2211 EndY=-12.4653 EndZ=0
    g374: LineSegment StartX=-10.117 StartY=-11.8029 StartZ=0 EndX=-14.0637 EndY=-11.8641 EndZ=0
    g375: LineSegment StartX=-14.0637 StartY=-11.8641 StartZ=0 EndX=-14.2211 EndY=-12.4653 EndZ=0
    g376: LineSegment StartX=-14.5083 StartY=-11.6448 StartZ=0 EndX=-14.0637 EndY=-11.8641 EndZ=0
    g377: LineSegment StartX=-8.50952 StartY=-13.2747 StartZ=0 EndX=-12.4562 EndY=-13.3358 EndZ=0
    g378: LineSegment StartX=-12.9009 StartY=-13.1165 StartZ=0 EndX=-12.4562 EndY=-13.3358 EndZ=0
    g379: LineSegment StartX=-8.3521 StartY=-12.6735 StartZ=0 EndX=-12.2988 EndY=-12.7346 EndZ=0
    g380: LineSegment StartX=-12.2988 StartY=-12.7346 StartZ=0 EndX=-12.4562 EndY=-13.3358 EndZ=0
    g381: LineSegment StartX=-8.7968 StartY=-12.4541 StartZ=0 EndX=-12.7435 EndY=-12.5153 EndZ=0
    g382: LineSegment StartX=-12.7435 StartY=-12.5153 StartZ=0 EndX=-12.2988 EndY=-12.7346 EndZ=0
    g383: LineSegment StartX=-12.7435 StartY=-12.5153 StartZ=0 EndX=-12.9009 EndY=-13.1165 EndZ=0
    g384: LineSegment StartX=-13.8041 StartY=-10.6631 StartZ=0 EndX=-17.7508 EndY=-10.7243 EndZ=0
    g385: LineSegment StartX=-18.1955 StartY=-10.5049 StartZ=0 EndX=-17.7508 EndY=-10.7243 EndZ=0
    g386: LineSegment StartX=-13.6467 StartY=-10.0619 StartZ=0 EndX=-17.5934 EndY=-10.1231 EndZ=0
    g387: LineSegment StartX=-17.5934 StartY=-10.1231 StartZ=0 EndX=-17.7508 EndY=-10.7243 EndZ=0
    g388: LineSegment StartX=-14.0914 StartY=-9.84254 StartZ=0 EndX=-18.0381 EndY=-9.90371 EndZ=0
    g389: LineSegment StartX=-18.0381 StartY=-9.90371 StartZ=0 EndX=-17.5934 EndY=-10.1231 EndZ=0
    g390: LineSegment StartX=-18.0381 StartY=-9.90371 StartZ=0 EndX=-18.1955 EndY=-10.5049 EndZ=0
    g391: LineSegment StartX=-12.3265 StartY=-10.7131 StartZ=0 EndX=-16.2732 EndY=-10.7742 EndZ=0
    g392: LineSegment StartX=-16.2732 StartY=-10.7742 StartZ=0 EndX=-16.4306 EndY=-11.3754 EndZ=0
    g393: LineSegment StartX=-12.0393 StartY=-11.5336 StartZ=0 EndX=-15.9859 EndY=-11.5948 EndZ=0
    g394: LineSegment StartX=-16.4306 StartY=-11.3754 StartZ=0 EndX=-15.9859 EndY=-11.5948 EndZ=0
    g395: LineSegment StartX=-11.8819 StartY=-10.9324 StartZ=0 EndX=-15.8285 EndY=-10.9936 EndZ=0
    g396: LineSegment StartX=-15.8285 StartY=-10.9936 StartZ=0 EndX=-15.9859 EndY=-11.5948 EndZ=0
    g397: LineSegment StartX=-16.2732 StartY=-10.7742 StartZ=0 EndX=-15.8285 EndY=-10.9936 EndZ=0
    g398: LineSegment StartX=1.79245 StartY=-17.6773 StartZ=0 EndX=-2.15422 EndY=-17.7384 EndZ=0
    g399: LineSegment StartX=-2.15422 StartY=-17.7384 StartZ=0 EndX=-2.31165 EndY=-18.3396 EndZ=0
    ... +9203 more geometry lines
FEATURE [TechDraw::DrawViewImage] ActiveView
  Height = 102.4
  ImageFile = <userpath>/.cache/FreeCAD/Cache/FreeCAD_Doc_52440b77-6a3d-481c-94c6-4dcdad8efe14_99b95c_167259/PageActiveViewR4nLeh.png
  LockPosition = false
  Rotation = 0
  ScaleType = 2
  Width = 128
  X = 148.5
  Y = 105
FEATURE [TechDraw::DrawPage] Page
  KeepUpdated = true
  NextBalloonIndex = 1
  ProjectionType = 1
  Template = -> Template
  Views = -> [ActiveView]
